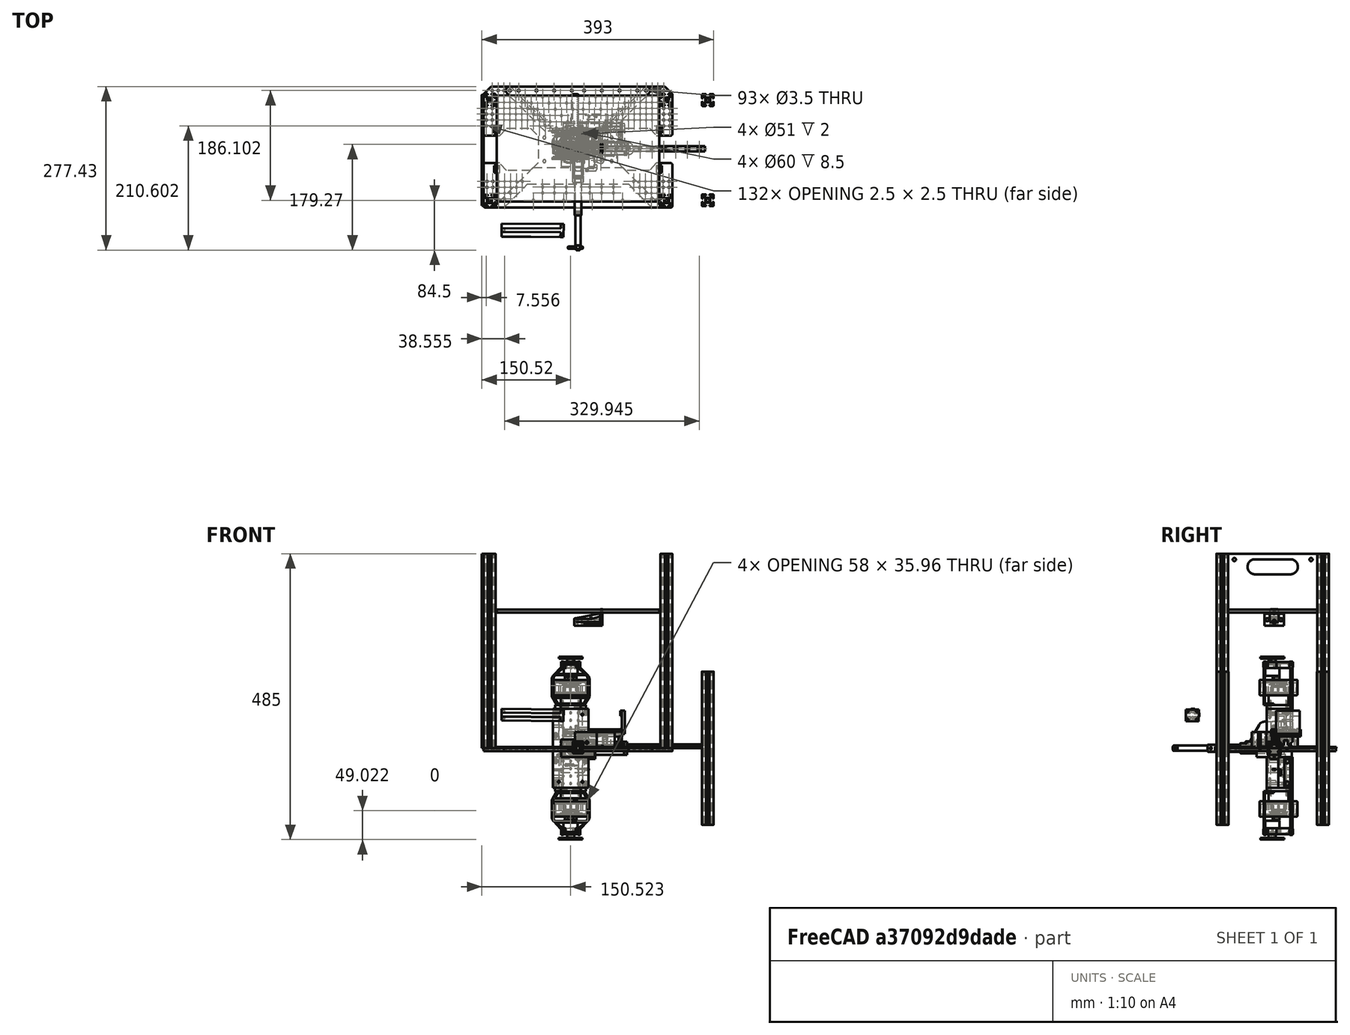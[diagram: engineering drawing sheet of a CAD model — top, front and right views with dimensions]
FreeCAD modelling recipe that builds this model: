
FCSTD DOCUMENT  (FreeCAD 1.0R39319 (Git))
Label: NutSorter
License: All rights reserved
LicenseURL: https://en.wikipedia.org/wiki/All_rights_reserved
objects: Sketcher::SketchObject×84, Part::Feature×80, PartDesign::Pocket×42, PartDesign::Pad×39, App::Part×34, PartDesign::Body×28, App::FeaturePython×27, Part::FeaturePython×11, App::Link×7, PartDesign::Mirrored×6, Assembly::JointGroup×4, PartDesign::FeatureBase×4, Assembly::AssemblyObject×4, PartDesign::Revolution×3, PartDesign::PolarPattern×3, PartDesign::Chamfer×2, PartDesign::LinearPattern×1, Spreadsheet::Sheet×1, PartDesign::MultiTransform×1, PartDesign::AdditiveLoft×1, +2 more types
note: 581 computed .brp shape members not serialized (recipe doc carries the construction recipe); baked Part::Feature solids carry a one-line shape summary decoded from their .brp

FEATURE [Part::FeaturePython] InvoluteRack  # WARN: FeaturePython — macro-defined, semantics opaque (R4)
  AttacherType = Attacher::AttachEngine3D
  add_endings = true
  clearance = 0.25
  double_helix = false
  head = 0
  head_fillet = 0
  height = 3
  helix_angle = 0
  module = 1
  num_teeth = 30
  pressure_angle = 20
  properties_from_tool = false
  root_fillet = 0
  simplified = false
  thickness = 9.5
  transverse_pitch = 3.14159
  version = 1.3.0
FEATURE [Part::FeaturePython] InvoluteGear  # WARN: FeaturePython — macro-defined, semantics opaque (R4)
  AttacherType = Attacher::AttachEngine3D
  addendum_diameter = 26
  angular_backlash = 0
  axle_hole = false
  axle_holesize = 10
  backlash = 0
  clearance = 0.25
  double_helix = false
  head = 0
  head_fillet = 0
  height = 5.5
  helix_angle = 0
  module = 1
  num_teeth = 24
  numpoints = 20
  offset_hole = false
  offset_holeoffset = 10
  offset_holesize = 10
  pitch_diameter = 24
  pressure_angle = 20
  properties_from_tool = false
  reversed_backlash = false
  root_diameter = 21.5
  root_fillet = 0
  shift = 0
  simple = false
  transverse_pitch = 3.14159
  traverse_module = 1
  undercut = false
  version = 1.3.0
  expr: angular_backlash = backlash / pitch_diameter * 360 ° / pi
FEATURE [Part::Feature] Part__Feature008002002006397  label="chariot_MGN9-H"
  Placement = pos=(0,0,0) rot=(0.707107,0.707107,0;3.14159rad)
  shape: bbox 8.005 x 20.01 x 40.67 mm, 245 faces, 9 solids (baked)
FEATURE [Sketcher::SketchObject] Sketch031
  ArcFitTolerance = 0
  AttachmentSupport = -> [YZ_Plane013]
  FullyConstrained = true
  MakeInternals = false
  MapMode = 5
  Placement = pos=(0,0,0) rot=(0.57735,0.57735,0.57735;2.0944rad)
  sketch-geometry (4):
    g0: LineSegment StartX=-4.5 StartY=0 StartZ=0 EndX=4.5 EndY=0 EndZ=0
    g1: LineSegment StartX=4.5 StartY=0 StartZ=0 EndX=4.5 EndY=6.5 EndZ=0
    g2: LineSegment StartX=4.5 StartY=6.5 StartZ=0 EndX=-4.5 EndY=6.5 EndZ=0
    g3: LineSegment StartX=-4.5 StartY=6.5 StartZ=0 EndX=-4.5 EndY=0 EndZ=0
  constraints (11):
    c: Coincident(g0,g1)
    c: Coincident(g1,g2)
    c: Coincident(g2,g3)
    c: Coincident(g3,g0)
    c: Horizontal(g0)
    c: Horizontal(g2)
    c: Vertical(g1)
    c: Vertical(g3)
    c: Symmetric(g0,g0,g-1)
    c: DistanceX(g0,g0) = 9  'width'
    c: DistanceY(g1,g1) = 6.5  'height'
FEATURE [PartDesign::Pad] Pad012
  Direction = (1,0,0)
  Length = 215
  Length2 = 10
  Placement = pos=(0,0,0) rot=(0.57735,0.57735,0.57735;2.0944rad)
  Profile = -> Sketch031
  ReferenceAxis = -> Sketch031 [N_Axis]
  Suppressed = false
  Type = 0
  expr: Length = Spreadsheet001.length
FEATURE [Sketcher::SketchObject] Sketch032
  ArcFitTolerance = 0
  AttachmentSupport = -> [YZ_Plane013]
  FullyConstrained = true
  MakeInternals = false
  MapMode = 5
  Placement = pos=(0,0,0) rot=(0.57735,-0.57735,-0.57735;2.0944rad)
  expr: Constraints[13] = 6.5 - 1.8
  expr: Constraints[14] = <<Sketch031>>.Constraints.width / 2 + 0.1 mm
  sketch-geometry (10):
    g0: ArcOfCircle CenterX=-4.6 CenterY=4.7 CenterZ=0 NormalX=0 NormalY=0 NormalZ=1 AngleXU=0 Radius=1 StartAngle=0.25268 EndAngle=6.03051
    g1: LineSegment StartX=-3.63175 StartY=4.95 StartZ=0 EndX=-3.13175 EndY=4.95 EndZ=0
    g2: LineSegment StartX=-3.13175 StartY=4.95 StartZ=0 EndX=-3.13175 EndY=4.45 EndZ=0
    g3: LineSegment StartX=-3.13175 StartY=4.45 StartZ=0 EndX=-3.63175 EndY=4.45 EndZ=0
    g4: LineSegment [constr] StartX=-4.6 StartY=4.7 StartZ=0 EndX=-3.13175 EndY=4.7 EndZ=0
    g5: ArcOfCircle CenterX=4.6 CenterY=4.7 CenterZ=0 NormalX=0 NormalY=0 NormalZ=1 AngleXU=0 Radius=1 StartAngle=3.39427 EndAngle=9.1721
    g6: LineSegment StartX=3.63175 StartY=4.95 StartZ=0 EndX=3.13175 EndY=4.95 EndZ=0
    g7: LineSegment StartX=3.13175 StartY=4.95 StartZ=0 EndX=3.13175 EndY=4.45 EndZ=0
    g8: LineSegment StartX=3.13175 StartY=4.45 StartZ=0 EndX=3.63175 EndY=4.45 EndZ=0
    g9: LineSegment [constr] StartX=4.6 StartY=4.7 StartZ=0 EndX=3.13175 EndY=4.7 EndZ=0
  constraints (29):
    c: Horizontal(g1)
    c: Coincident(g2,g1)
    c: Vertical(g2)
    c: Coincident(g3,g2)
    c: Horizontal(g3)
    c: Coincident(g4,g0)
    c: Horizontal(g4)
    c: Symmetric(g2,g1,g4)
    c: Coincident(g0,g3)
    c: Coincident(g0,g1)
    c: DistanceY(g2,g2) = 0.5
    c: DistanceX(g1,g1) = 0.5
    c: Diameter(g0) = 2
    c: DistanceY(g-1,g0) = 4.7
    c: DistanceX(g0,g-1) = 4.6
    c: Horizontal(g6)
    c: Coincident(g7,g6)
    c: Vertical(g7)
    c: Coincident(g8,g7)
    c: Horizontal(g8)
    c: Coincident(g9,g5)
    c: Horizontal(g9)
    c: Symmetric(g7,g6,g9)
    c: Coincident(g5,g8)
    c: Coincident(g5,g6)
    c: Diameter(g5) = 2
    c: Symmetric(g4,g9,g-2)
    c: Equal(g2,g7)
    c: Equal(g1,g6)
FEATURE [PartDesign::Pocket] Pocket015  label="Balls cut"
  BaseFeature = -> Pad012
  Direction = (1,0,0)
  Length = 5
  Length2 = 5
  Placement = pos=(0,0,0) rot=(0.57735,0.57735,0.57735;2.0944rad)
  Profile = -> Sketch032
  ReferenceAxis = -> Sketch032 [N_Axis]
  Suppressed = false
  Type = 1
FEATURE [Sketcher::SketchObject] Sketch033
  ArcFitTolerance = 0
  AttachmentOffset = pos=(5.5,0,0) rot=(0,0,1;1.5708rad)
  AttachmentSupport = -> [XY_Plane013]
  FullyConstrained = true
  MakeInternals = false
  MapMode = 5
  Placement = pos=(5.5,0,0) rot=(0,0,1;1.5708rad)
  expr: .AttachmentOffset.Base.x = Spreadsheet001.offset
  sketch-geometry (1):
    g0: Circle CenterX=0 CenterY=0 CenterZ=0 NormalX=0 NormalY=0 NormalZ=1 AngleXU=0 Radius=1.75
  constraints (2):
    c: Coincident(g0,g-1)
    c: Diameter(g0) = 3.5
FEATURE [PartDesign::Pocket] Pocket016  label="Screw hole"
  BaseFeature = -> Pocket015
  Direction = (0,0,-1)
  Length = 5
  Length2 = 5
  Midplane = true
  Placement = pos=(0,0,0) rot=(0.57735,0.57735,0.57735;2.0944rad)
  Profile = -> Sketch033
  ReferenceAxis = -> Sketch033 [N_Axis]
  Suppressed = false
  Type = 1
FEATURE [Sketcher::SketchObject] Sketch034
  ArcFitTolerance = 0
  AttachmentOffset = pos=(5.5,0,6.5) rot=(0,0,1;1.5708rad)
  AttachmentSupport = -> [XY_Plane013]
  FullyConstrained = true
  MakeInternals = false
  MapMode = 5
  Placement = pos=(5.5,0,6.5) rot=(0,0,1;1.5708rad)
  expr: .AttachmentOffset.Base.x = Spreadsheet001.offset
  expr: .AttachmentOffset.Base.z = Sketch031.Constraints.height
  sketch-geometry (1):
    g0: Circle CenterX=0 CenterY=0 CenterZ=0 NormalX=0 NormalY=0 NormalZ=1 AngleXU=0 Radius=3
  constraints (2):
    c: Coincident(g0,g-1)
    c: Diameter(g0) = 6
FEATURE [PartDesign::Pocket] Pocket017  label="Screw head cut"
  BaseFeature = -> Pocket016
  Direction = (0,0,-1)
  Length = 3.5
  Length2 = 5
  Placement = pos=(0,0,0) rot=(0.57735,0.57735,0.57735;2.0944rad)
  Profile = -> Sketch034
  ReferenceAxis = -> Sketch034 [N_Axis]
  Suppressed = false
  Type = 0
FEATURE [PartDesign::Chamfer] Chamfer001  label="Chamfer"
  Angle = 45
  Base = -> Pocket017 [Edge47]
  BaseFeature = -> Pocket017
  ChamferType = 0
  FlipDirection = false
  Placement = pos=(0,0,0) rot=(0.57735,0.57735,0.57735;2.0944rad)
  Size = 0.2
  Size2 = 1
  SupportTransform = false
  Suppressed = false
  UseAllEdges = false
FEATURE [PartDesign::LinearPattern] LinearPattern001  label="LinearPattern"
  BaseFeature = -> Chamfer001
  Direction = -> Sketch033 [V_Axis]
  Length = 200
  Mode = 0
  Occurrences = 11
  Offset = 20
  Originals = -> [Pocket016,Pocket017,Chamfer001]
  Placement = pos=(0,0,0) rot=(0.57735,0.57735,0.57735;2.0944rad)
  Reversed = true
  Suppressed = false
  TransformMode = 0
  expr: Length = Spreadsheet001.distance
  expr: Occurrences = Spreadsheet001.holes_number
FEATURE [PartDesign::Body] Body011  label="Hiwin rail MGN9R"
  AllowCompound = false
  Group = -> [Sketch031,Pad012,Sketch032,Pocket015,Sketch033,Pocket016,Sketch034,Pocket017,Chamfer001,LinearPattern001]
  Origin = -> Origin013
  Tip = -> LinearPattern001
FEATURE [Spreadsheet::Sheet] Spreadsheet001  label="Spreadsheet_MGN9"
  cells = A1='Length rail; B1='Длина рельсы, мм; C1(length)=215; A2='Holes distance; B2='Расстояние между отверстиями; C2(holes_distance)=20; A3='Holes number; B3='Количество отверстий; C3(holes_number)==floor((length - min_offset * 2) / holes_distance) + 2; A4='Distance end holes; B4='Расстояние между центрами крайних отверстий; C4(distance)==holes_distance * (holes_number - 1); A5='Offset 1st hole; B5='Позиция 1го отверстия; C5(offset)=5.5; A6='Min offset 1st hole; B6='Минимальное расстояние от края до центра 1го отверстия; C6(min_offset)=9
FEATURE [App::Part] Part002002  label="Hiwin MGN9"
  Group = -> [Body011,Spreadsheet001]
  Origin = -> Origin014
  Placement = pos=(0,0,220) rot=(0,1,0;1.5708rad)
FEATURE [Assembly::JointGroup] Joints001
FEATURE [Part::Feature] Part__Feature008002002006398  label="L16_50MM_BODY_A"
  Placement = pos=(0,-51,0) rot=(0,0,1;0rad)
  shape: bbox 20.08 x 117.7 x 20.17 mm, 719 faces (baked)
FEATURE [Part::Feature] Part__Feature008002002006399  label="L16_50MM_LIFT_A"
  Placement = pos=(0,-101,0) rot=(0,0,1;0rad)
  shape: bbox 10.2 x 71.63 x 9.971 mm, 40 faces (baked)
  expr: .Placement.Base.y = -51 mm - VarSet.Position_verrin
FEATURE [Sketcher::SketchObject] Sketch036
  ArcFitTolerance = 1e-06
  AttachmentSupport = -> [YZ_Plane017]
  FullyConstrained = true
  MakeInternals = false
  MapMode = 5
  Placement = pos=(0,0,0) rot=(0.57735,0.57735,0.57735;2.0944rad)
  sketch-geometry (4):
    g0: LineSegment StartX=-11 StartY=11 StartZ=0 EndX=-11 EndY=-11 EndZ=0
    g1: LineSegment StartX=-11 StartY=-11 StartZ=0 EndX=11 EndY=-11 EndZ=0
    g2: LineSegment StartX=11 StartY=-11 StartZ=0 EndX=11 EndY=11 EndZ=0
    g3: LineSegment StartX=11 StartY=11 StartZ=0 EndX=-11 EndY=11 EndZ=0
  constraints (11):
    c: Coincident(g0,g1)
    c: Coincident(g1,g2)
    c: Coincident(g2,g3)
    c: Coincident(g3,g0)
    c: Vertical(g0)
    c: Vertical(g2)
    c: Horizontal(g1)
    c: Horizontal(g3)
    c: Symmetric(g2,g0,g-1)
    c: DistanceX(g3,g3) = 22
    c: DistanceY(g0,g0) = 22
FEATURE [Sketcher::SketchObject] Sketch037
  ArcFitTolerance = 1e-06
  AttachmentOffset = pos=(0,0,74) rot=(0,0,1;0rad)
  AttachmentSupport = -> [YZ_Plane017]
  FullyConstrained = true
  MakeInternals = false
  MapMode = 5
  Placement = pos=(74,0,0) rot=(0.57735,0.57735,0.57735;2.0944rad)
  sketch-geometry (4):
    g0: LineSegment StartX=-4 StartY=11 StartZ=0 EndX=-4 EndY=-11 EndZ=0
    g1: LineSegment StartX=-4 StartY=-11 StartZ=0 EndX=4 EndY=-11 EndZ=0
    g2: LineSegment StartX=4 StartY=-11 StartZ=0 EndX=4 EndY=11 EndZ=0
    g3: LineSegment StartX=4 StartY=11 StartZ=0 EndX=-4 EndY=11 EndZ=0
  constraints (11):
    c: Coincident(g0,g1)
    c: Coincident(g1,g2)
    c: Coincident(g2,g3)
    c: Coincident(g3,g0)
    c: Vertical(g0)
    c: Vertical(g2)
    c: Horizontal(g1)
    c: Horizontal(g3)
    c: Symmetric(g2,g0,g-1)
    c: DistanceY(g2,g2) = 22
    c: Distance(g1,g1) = 8
FEATURE [Sketcher::SketchObject] Sketch038
  ArcFitTolerance = 1e-06
  AttachmentSupport = -> [YZ_Plane017]
  FullyConstrained = true
  MakeInternals = false
  MapMode = 5
  Placement = pos=(0,0,0) rot=(0.57735,0.57735,0.57735;2.0944rad)
  sketch-geometry (1):
    g0: Circle CenterX=7.5 CenterY=-8 CenterZ=0 NormalX=0 NormalY=0 NormalZ=1 AngleXU=0 Radius=1.75
  constraints (3):
    c: Diameter(g0) = 3.5
    c: DistanceX(g-1,g0) = 7.5
    c: DistanceY(g0,g-1) = 8
FEATURE [PartDesign::Pad] Pad013
  Direction = (1,0,0)
  Length = 6.5
  Length2 = 10
  Placement = pos=(0,0,0) rot=(1,1,1;2.0944rad)
  Profile = -> Sketch036
  ReferenceAxis = -> Sketch036 [N_Axis]
  Suppressed = false
  Type = 0
FEATURE [PartDesign::Pocket] Pocket018
  BaseFeature = -> Pad013
  Direction = (-1,0,0)
  Length = 5
  Length2 = 5
  Midplane = true
  Placement = pos=(0,0,0) rot=(1,1,1;2.0944rad)
  Profile = -> Sketch038
  ReferenceAxis = -> Sketch038 [N_Axis]
  Suppressed = false
  Type = 1
FEATURE [PartDesign::Mirrored] Mirrored002
  MirrorPlane = -> Sketch038 [V_Axis]
  Placement = pos=(0,0,0) rot=(1,1,1;2.0944rad)
  Suppressed = false
  TransformMode = 0
FEATURE [PartDesign::Mirrored] Mirrored003
  MirrorPlane = -> Sketch038 [H_Axis]
  Placement = pos=(0,0,0) rot=(1,1,1;2.0944rad)
  Suppressed = false
  TransformMode = 0
FEATURE [PartDesign::MultiTransform] MultiTransform
  BaseFeature = -> Pocket018
  Originals = -> [Pocket018]
  Placement = pos=(0,0,0) rot=(1,1,1;2.0944rad)
  Suppressed = false
  TransformMode = 0
  Transformations = -> [Mirrored002,Mirrored003]
FEATURE [Sketcher::SketchObject] Sketch040
  ArcFitTolerance = 1e-06
  AttachmentOffset = pos=(0,0,6.5) rot=(0,0,1;0rad)
  AttachmentSupport = -> [YZ_Plane017]
  FullyConstrained = true
  MakeInternals = false
  MapMode = 5
  Placement = pos=(6.5,0,0) rot=(0.57735,0.57735,0.57735;2.0944rad)
  sketch-geometry (4):
    g0: LineSegment StartX=-4 StartY=11 StartZ=0 EndX=-4 EndY=-11 EndZ=0
    g1: LineSegment StartX=-4 StartY=-11 StartZ=0 EndX=4 EndY=-11 EndZ=0
    g2: LineSegment StartX=4 StartY=-11 StartZ=0 EndX=4 EndY=11 EndZ=0
    g3: LineSegment StartX=4 StartY=11 StartZ=0 EndX=-4 EndY=11 EndZ=0
  constraints (11):
    c: Coincident(g0,g1)
    c: Coincident(g1,g2)
    c: Coincident(g2,g3)
    c: Coincident(g3,g0)
    c: Vertical(g0)
    c: Vertical(g2)
    c: Horizontal(g1)
    c: Horizontal(g3)
    c: Symmetric(g2,g0,g-1)
    c: DistanceX(g3,g3) = 8
    c: DistanceY(g2,g2) = 22
FEATURE [PartDesign::AdditiveLoft] AdditiveLoft
  BaseFeature = -> MultiTransform
  Closed = false
  Placement = pos=(0,0,0) rot=(1,1,1;2.0944rad)
  Profile = -> Sketch037
  Ruled = false
  Sections = -> [Sketch040]
  Suppressed = false
FEATURE [Sketcher::SketchObject] Sketch041
  ArcFitTolerance = 1e-06
  AttachmentOffset = pos=(0,1,0) rot=(0,0,1;0rad)
  AttachmentSupport = -> [AdditiveLoft]
  FullyConstrained = true
  MakeInternals = false
  MapMode = 5
  Placement = pos=(74,0,1) rot=(0.57735,0.57735,0.57735;2.0944rad)
  sketch-geometry (8):
    g0: LineSegment StartX=-11 StartY=10 StartZ=0 EndX=-11 EndY=-10 EndZ=0
    g1: LineSegment StartX=-11 StartY=-10 StartZ=0 EndX=11 EndY=-10 EndZ=0
    g2: LineSegment StartX=11 StartY=-10 StartZ=0 EndX=11 EndY=10 EndZ=0
    g3: LineSegment StartX=11 StartY=10 StartZ=0 EndX=-11 EndY=10 EndZ=0
    g4: Circle CenterX=8 CenterY=-7 CenterZ=0 NormalX=0 NormalY=0 NormalZ=1 AngleXU=0 Radius=1.75
    g5: Circle CenterX=-8 CenterY=-7 CenterZ=0 NormalX=0 NormalY=0 NormalZ=1 AngleXU=0 Radius=1.75
    g6: Circle CenterX=8 CenterY=7 CenterZ=0 NormalX=0 NormalY=0 NormalZ=1 AngleXU=0 Radius=1.75
    g7: Circle CenterX=-8 CenterY=7 CenterZ=0 NormalX=0 NormalY=0 NormalZ=1 AngleXU=0 Radius=1.75
  constraints (21):
    c: Coincident(g0,g1)
    c: Coincident(g1,g2)
    c: Coincident(g2,g3)
    c: Coincident(g3,g0)
    c: Vertical(g0)
    c: Vertical(g2)
    c: Horizontal(g1)
    c: Distance(g1,g1) = 22
    c: Symmetric(g0,g1,g-1)
    c: Horizontal(g3)
    c: DistanceY(g2,g2) = 20
    c: Diameter(g4) = 3.5
    c: Diameter(g5) = 3.5
    c: Diameter(g6) = 3.5
    c: Diameter(g7) = 3.5
    c: Symmetric(g7,g4,g-1)
    c: Symmetric(g5,g6,g-1)
    c: Horizontal(g6,g7)
    c: Vertical(g7,g5)
    c: DistanceX(g7,g-1) = 8
    c: DistanceY(g-1,g7) = 7
FEATURE [PartDesign::Pad] Pad014
  BaseFeature = -> AdditiveLoft
  Direction = (1,0,0)
  Length = 5
  Length2 = 10
  Placement = pos=(0,0,0) rot=(1,1,1;2.0944rad)
  Profile = -> Sketch041
  ReferenceAxis = -> Sketch041 [N_Axis]
  Suppressed = false
  Type = 0
FEATURE [Sketcher::SketchObject] Sketch042
  ArcFitTolerance = 1e-06
  AttachmentSupport = -> [XY_Plane019]
  FullyConstrained = true
  MakeInternals = false
  MapMode = 5
  Placement = pos=(0,0,0) rot=(0,1,0;3.14159rad)
  expr: Constraints[36] = 20 mm + VarSet.jeu
  expr: Constraints[37] = 40 mm + VarSet.jeu
  expr: Constraints[72] = 18 mm + VarSet.jeu
  expr: Constraints[73] = 20 mm + VarSet.jeu
  expr: Constraints[86] = 9 mm + VarSet.jeu
  expr: Constraints[87] = 6.5 mm + VarSet.jeu
  sketch-geometry (52):
    g0: LineSegment StartX=-28.5 StartY=-38 StartZ=0 EndX=1.8 EndY=-38 EndZ=0
    g1: LineSegment StartX=4.8 StartY=-35 StartZ=0 EndX=4.8 EndY=10 EndZ=0
    g2: ArcOfCircle CenterX=1.8 CenterY=-35 CenterZ=0 NormalX=0 NormalY=0 NormalZ=1 AngleXU=0 Radius=3 StartAngle=4.71239 EndAngle=6.28319
    g3: ArcOfCircle CenterX=1.8 CenterY=10 CenterZ=0 NormalX=0 NormalY=0 NormalZ=1 AngleXU=0 Radius=3 StartAngle=0 EndAngle=1.5708
    g4: GeomPoint [constr] X=4.8 Y=-38 Z=0
    g5: LineSegment StartX=-59.5 StartY=-13 StartZ=0 EndX=-34.5 EndY=-13 EndZ=0
    g6: LineSegment StartX=1.8 StartY=13 StartZ=0 EndX=-59.5 EndY=13 EndZ=0
    g7: ArcOfCircle CenterX=-59.5 CenterY=10 CenterZ=0 NormalX=0 NormalY=0 NormalZ=1 AngleXU=0 Radius=3 StartAngle=1.5708 EndAngle=3.14159
    g8: ArcOfCircle CenterX=-59.5 CenterY=-10 CenterZ=0 NormalX=0 NormalY=0 NormalZ=1 AngleXU=0 Radius=3 StartAngle=3.14159 EndAngle=4.71239
    g9: LineSegment StartX=-54.575 StartY=-10.075 StartZ=0 EndX=-16.425 EndY=-10.075 EndZ=0
    g10: LineSegment StartX=-15.425 StartY=-9.075 StartZ=0 EndX=-15.425 EndY=9.075 EndZ=0
    g11: LineSegment StartX=-16.425 StartY=10.075 StartZ=0 EndX=-54.575 EndY=10.075 EndZ=0
    g12: ArcOfCircle CenterX=-54.575 CenterY=9.075 CenterZ=0 NormalX=0 NormalY=0 NormalZ=1 AngleXU=0 Radius=1 StartAngle=1.5708 EndAngle=3.14159
    g13: ArcOfCircle CenterX=-54.575 CenterY=-9.075 CenterZ=0 NormalX=0 NormalY=0 NormalZ=1 AngleXU=0 Radius=1 StartAngle=3.14159 EndAngle=4.71239
    g14: ArcOfCircle CenterX=-16.425 CenterY=-9.075 CenterZ=0 NormalX=0 NormalY=0 NormalZ=1 AngleXU=0 Radius=1 StartAngle=4.71239 EndAngle=6.28319
    g15: ArcOfCircle CenterX=-16.425 CenterY=9.075 CenterZ=0 NormalX=0 NormalY=0 NormalZ=1 AngleXU=0 Radius=1 StartAngle=0 EndAngle=1.5708
    g16: GeomPoint [constr] X=-55.575 Y=10.075 Z=0
    g17: GeomPoint [constr] X=-15.425 Y=-10.075 Z=0
    g18: GeomPoint X=-35.5 Y=0 Z=0
    g19: ArcOfCircle CenterX=-34.5 CenterY=-16 CenterZ=0 NormalX=0 NormalY=0 NormalZ=1 AngleXU=0 Radius=3 StartAngle=0 EndAngle=1.5708
    g20: LineSegment StartX=-31.5 StartY=-16 StartZ=0 EndX=-31.5 EndY=-22.5 EndZ=0
    g21: ArcOfCircle CenterX=-28.5 CenterY=-35 CenterZ=0 NormalX=0 NormalY=0 NormalZ=1 AngleXU=0 Radius=3 StartAngle=3.14159 EndAngle=4.71239
    g22: GeomPoint [constr] X=-31.5 Y=-38 Z=0
    g23: GeomPoint X=-16.5 Y=-25 Z=0
    g24: LineSegment StartX=-26.575 StartY=-17.125 StartZ=0 EndX=-26.575 EndY=-22.5 EndZ=0
    g25: LineSegment StartX=-25.375 StartY=-34.075 StartZ=0 EndX=-7.625 EndY=-34.075 EndZ=0
    g26: LineSegment StartX=-6.425 StartY=-32.875 StartZ=0 EndX=-6.425 EndY=-17.125 EndZ=0
    g27: LineSegment StartX=-7.625 StartY=-15.925 StartZ=0 EndX=-25.375 EndY=-15.925 EndZ=0
    g28: ArcOfCircle CenterX=-25.375 CenterY=-17.125 CenterZ=0 NormalX=0 NormalY=0 NormalZ=1 AngleXU=0 Radius=1.2 StartAngle=1.5708 EndAngle=3.14159
    g29: ArcOfCircle CenterX=-25.375 CenterY=-32.875 CenterZ=0 NormalX=0 NormalY=0 NormalZ=1 AngleXU=0 Radius=1.2 StartAngle=3.14159 EndAngle=4.71239
    g30: ArcOfCircle CenterX=-7.625 CenterY=-32.875 CenterZ=0 NormalX=0 NormalY=0 NormalZ=1 AngleXU=0 Radius=1.2 StartAngle=4.71239 EndAngle=6.28319
    g31: ArcOfCircle CenterX=-7.625 CenterY=-17.125 CenterZ=0 NormalX=0 NormalY=0 NormalZ=1 AngleXU=0 Radius=1.2 StartAngle=-9e-16 EndAngle=1.5708
    g32: GeomPoint [constr] X=-26.575 Y=-15.925 Z=0
    g33: GeomPoint [constr] X=-6.425 Y=-34.075 Z=0
    g34: LineSegment StartX=-6.575 StartY=4.575 StartZ=0 EndX=-6.575 EndY=-4.575 EndZ=0
    g35: LineSegment StartX=-6.575 StartY=-4.575 StartZ=0 EndX=0.075 EndY=-4.575 EndZ=0
    g36: LineSegment StartX=0.075 StartY=-4.575 StartZ=0 EndX=0.075 EndY=4.575 EndZ=0
    g37: LineSegment StartX=0.075 StartY=4.575 StartZ=0 EndX=-6.575 EndY=4.575 EndZ=0
    g38: GeomPoint X=-3.25 Y=0 Z=0
    g39: LineSegment StartX=-26.575 StartY=-22.5 StartZ=0 EndX=-31.5 EndY=-22.5 EndZ=0
    g40: LineSegment StartX=-31.5 StartY=-27.5 StartZ=0 EndX=-26.575 EndY=-27.5 EndZ=0
    g41: LineSegment StartX=-26.575 StartY=-27.5 StartZ=0 EndX=-26.575 EndY=-32.875 EndZ=0
    g42: LineSegment StartX=-31.5 StartY=-27.5 StartZ=0 EndX=-31.5 EndY=-35 EndZ=0
    g43: LineSegment [constr] StartX=-16.5 StartY=-25 StartZ=0 EndX=-31.5 EndY=-25 EndZ=0
    g44: LineSegment StartX=-62.5 StartY=4 StartZ=0 EndX=-55.575 EndY=4 EndZ=0
    g45: LineSegment StartX=-62.5 StartY=-4 StartZ=0 EndX=-55.575 EndY=-4 EndZ=0
    g46: LineSegment StartX=-55.575 StartY=-4 StartZ=0 EndX=-55.575 EndY=-9.075 EndZ=0
    g47: LineSegment StartX=-62.5 StartY=-4 StartZ=0 EndX=-62.5 EndY=-10 EndZ=0
    g48: LineSegment StartX=-62.5 StartY=10 StartZ=0 EndX=-62.5 EndY=4 EndZ=0
    g49: LineSegment StartX=-55.575 StartY=9.075 StartZ=0 EndX=-55.575 EndY=4 EndZ=0
    g50: Circle CenterX=-10.5 CenterY=6 CenterZ=0 NormalX=0 NormalY=0 NormalZ=1 AngleXU=0 Radius=1.75
    g51: Circle CenterX=-10.5 CenterY=-6 CenterZ=0 NormalX=0 NormalY=0 NormalZ=1 AngleXU=0 Radius=1.75
  constraints (130):
    c: Tangent(g0,g2) = -1.5708
    c: Tangent(g1,g2) = -1.5708
    c: Tangent(g1,g3) = -1.5708
    c: Vertical(g1)
    c: Horizontal(g0)
    c: Equal(g2,g3)
    c: PointOnObject(g4,g0)
    c: PointOnObject(g4,g1)
    c: DistanceX(g-1,g1) = 4.8
    c: Tangent(g5,g8) = -1.5708
    c: Tangent(g6,g7) = -1.5708
    c: Horizontal(g5)
    c: Horizontal(g6)
    c: Equal(g7,g8)
    c: DistanceY(g5,g6) = 26
    c: Symmetric(g7,g47,g-1)
    c: Radius(g7) = 3
    c: Tangent(g3,g6) = -1.5708
    c: Tangent(g9,g13) = -1.5708
    c: Tangent(g9,g14) = -1.5708
    c: Tangent(g10,g14) = -1.5708
    c: Tangent(g10,g15) = -1.5708
    c: Tangent(g11,g15) = -1.5708
    c: Tangent(g11,g12) = -1.5708
    c: Vertical(g10)
    c: Horizontal(g9)
    c: Horizontal(g11)
    c: Equal(g12,g13)
    c: Equal(g13,g14)
    c: Equal(g14,g15)
    c: PointOnObject(g16,g11)
    c: PointOnObject(g17,g9)
    c: PointOnObject(g17,g10)
    c: Radius(g13) = 1
    c: PointOnObject(g18,g-1)
    c: Symmetric(g16,g17,g18)
    c: DistanceY(g9,g11) = 20.15
    c: DistanceX(g12,g10) = 40.15
    c: DistanceX(g18,g-1) = 35.5
    c: DistanceX(g7,g18) = 27
    c: Vertical(g20)
    c: PointOnObject(g22,g42)
    c: PointOnObject(g22,g0)
    c: Tangent(g0,g21) = -1.5708
    c: Tangent(g19,g5) = 1.5708
    c: Tangent(g20,g19) = 1.5708
    c: DistanceY(g23,g-1) = 25
    c: DistanceX(g23,g-1) = 16.5
    c: DistanceX(g19,g23) = 15
    c: DistanceY(g0,g23) = 13
    c: Equal(g21,g19)
    c: Equal(g19,g2)
    c: Equal(g3,g7)
    c: Tangent(g24,g28) = -1.5708
    c: Tangent(g25,g29) = -1.5708
    c: Tangent(g25,g30) = -1.5708
    c: Tangent(g26,g30) = -1.5708
    c: Tangent(g26,g31) = -1.5708
    c: Tangent(g27,g31) = -1.5708
    c: Tangent(g27,g28) = -1.5708
    c: Vertical(g24)
    c: Vertical(g26)
    c: Horizontal(g25)
    c: Horizontal(g27)
    c: Equal(g28,g29)
    c: Equal(g29,g30)
    c: Equal(g30,g31)
    c: PointOnObject(g32,g24)
    c: PointOnObject(g32,g27)
    c: PointOnObject(g33,g25)
    c: PointOnObject(g33,g26)
    c: Symmetric(g33,g32,g23)
    c: DistanceY(g25,g27) = 18.15
    c: DistanceX(g24,g26) = 20.15
    c: Radius(g31) = 1.2
    c: Coincident(g34,g35)
    c: Coincident(g35,g36)
    c: Coincident(g36,g37)
    c: Coincident(g37,g34)
    c: Vertical(g34)
    c: Vertical(g36)
    c: Horizontal(g35)
    c: Horizontal(g37)
    c: PointOnObject(g38,g-1)
    c: Symmetric(g36,g34,g38)
    c: DistanceX(g38,g-1) = 3.25
    c: DistanceY(g34,g34) = 9.15
    c: DistanceX(g37,g37) = 6.65
    c: Horizontal(g39)
    c: Horizontal(g40)
    c: PointOnObject(g40,g41)
    c: PointOnObject(g40,g42)
    c: Coincident(g24,g39)
    c: PointOnObject(g41,g40)
    c: Coincident(g20,g39)
    c: PointOnObject(g42,g40)
    c: Coincident(g43,g23)
    c: Horizontal(g43)
    c: Symmetric(g20,g40,g43)
    c: Vertical(g24,g40)
    c: Vertical(g40,g20)
    c: DistanceY(g40,g24) = 5
    c: Vertical(g41)
    c: Tangent(g41,g29) = -1.5708
    c: Tangent(g42,g21) = -1.5708
    c: Vertical(g42)
    c: Horizontal(g44)
    c: PointOnObject(g45,g47)
    c: Horizontal(g45)
    c: PointOnObject(g45,g46)
    c: PointOnObject(g46,g45)
    c: PointOnObject(g47,g45)
    c: Coincident(g48,g44)
    c: Vertical(g48)
    c: Tangent(g7,g48) = -1.5708
    c: Tangent(g47,g8) = -1.5708
    c: Tangent(g46,g13) = -1.5708
    c: Vertical(g46)
    c: Vertical(g47)
    c: Coincident(g49,g44)
    c: Vertical(g49)
    c: Tangent(g49,g12) = -1.5708
    c: Symmetric(g44,g45,g-1)
    c: Vertical(g16,g12)
    c: DistanceY(g45,g44) = 8
    c: Symmetric(g50,g51,g-1)
    c: DistanceX(g18,g51) = 25
    c: DistanceY(g18,g50) = 6
    c: Equal(g50,g51)
    c: Diameter(g50) = 3.5
FEATURE [PartDesign::Pad] Pad015
  Direction = (0,0,-1)
  Length = 27.5
  Length2 = 10
  Profile = -> Sketch042
  ReferenceAxis = -> Sketch042 [N_Axis]
  Reversed = true
  Suppressed = false
  Type = 0
FEATURE [Sketcher::SketchObject] Sketch043
  ArcFitTolerance = 1e-06
  AttachmentSupport = -> [XZ_Plane017]
  FullyConstrained = true
  MakeInternals = false
  MapMode = 5
  Placement = pos=(0,0,0) rot=(1,0,0;1.5708rad)
  sketch-geometry (4):
    g0: ArcOfCircle CenterX=6.5 CenterY=0 CenterZ=0 NormalX=0 NormalY=0 NormalZ=1 AngleXU=0 Radius=5 StartAngle=4.71239 EndAngle=7.85398
    g1: LineSegment StartX=6.5 StartY=5 StartZ=0 EndX=0 EndY=5 EndZ=0
    g2: LineSegment StartX=0 StartY=5 StartZ=0 EndX=0 EndY=-5 EndZ=0
    g3: LineSegment StartX=0 StartY=-5 StartZ=0 EndX=6.5 EndY=-5 EndZ=0
  constraints (11):
    c: PointOnObject(g0,g-1)
    c: Coincident(g1,g2)
    c: Coincident(g2,g3)
    c: Horizontal(g1)
    c: Horizontal(g3)
    c: Vertical(g2)
    c: PointOnObject(g2,g-2)
    c: Tangent(g0,g3) = -1.5708
    c: Tangent(g1,g0) = -1.5708
    c: DistanceX(g1,g1) = 6.5
    c: DistanceY(g2,g2) = 10
FEATURE [PartDesign::Pad] Pad016
  BaseFeature = -> Pad014
  Direction = (0,-1,2e-16)
  Length = 22
  Length2 = 10
  Midplane = true
  Placement = pos=(0,0,0) rot=(1,1,1;2.0944rad)
  Profile = -> Sketch043
  ReferenceAxis = -> Sketch043 [N_Axis]
  Suppressed = false
  Type = 0
FEATURE [Part::FeaturePython] ThreadedRod  label="M4x25-Tige filetée"  # WARN: FeaturePython — macro-defined, semantics opaque (R4)
  Diameter = 6
  DiameterCustom = 6
  Invert = false
  LeftHanded = false
  Length = 25
  MatchOuter = false
  OffsetAngle = 0
  PitchCustom = 1
  Placement = pos=(8,-168,0) rot=(0,1,0;1.5708rad)
  Thread = false
  Type = 4
  expr: .Placement.Base.y = -118 mm - VarSet.Position_verrin
FEATURE [App::Part] L16_50MM_SW_ASM
  Group = -> [Part__Feature008002002006398,Part__Feature008002002006399,ThreadedRod]
  Origin = -> Origin018
  Placement = pos=(15,-25,9.5) rot=(0.57735,-0.57735,0.57735;4.18879rad)
FEATURE [Sketcher::SketchObject] Sketch044
  ArcFitTolerance = 1e-06
  AttachmentSupport = -> [XZ_Plane017]
  FullyConstrained = true
  MakeInternals = false
  MapMode = 5
  Placement = pos=(0,0,0) rot=(1,0,0;1.5708rad)
  sketch-geometry (1):
    g0: Circle CenterX=5 CenterY=0 CenterZ=0 NormalX=0 NormalY=0 NormalZ=1 AngleXU=0 Radius=2.25
  constraints (3):
    c: Diameter(g0) = 4.5
    c: PointOnObject(g0,g-1)
    c: Distance(g0,g-2) = 5
FEATURE [PartDesign::Pocket] Pocket019
  BaseFeature = -> Pad016
  Direction = (0,1,-2e-16)
  Length = 5
  Length2 = 5
  Midplane = true
  Placement = pos=(0,0,0) rot=(1,1,1;2.0944rad)
  Profile = -> Sketch044
  ReferenceAxis = -> Sketch044 [N_Axis]
  Suppressed = false
  Type = 1
FEATURE [Part::FeaturePython] Screw001  label="M3x10-Vis"  # WARN: FeaturePython — macro-defined, semantics opaque (R4)
  Diameter = 4
  Invert = false
  LeftHanded = false
  Length = 10
  LengthCustom = 10
  MatchOuter = false
  OffsetAngle = 0
  Placement = pos=(11,-7.5,8) rot=(0,-1,0;4.71239rad)
  Thread = false
  Type = 75
FEATURE [PartDesign::Pad] Pad018
  BaseFeature = -> Pocket019
  Direction = (3e-16,-1e-15,-1)
  Length = 2
  Length2 = 10
  Placement = pos=(0,0,0) rot=(1,1,1;2.0944rad)
  Profile = -> Pocket019 [Face32]
  Suppressed = false
  Type = 0
FEATURE [Sketcher::SketchObject] Sketch045
  ArcFitTolerance = 1e-06
  AttachmentSupport = -> [XZ_Plane017]
  ExternalGeometry = -> [Sketch041,Pad018]
  FullyConstrained = true
  MakeInternals = false
  MapMode = 5
  Placement = pos=(0,0,0) rot=(1,0,0;1.5708rad)
  sketch-geometry (4):
    g0: LineSegment StartX=9 StartY=2.5 StartZ=0 EndX=9 EndY=-2.5 EndZ=0
    g1: LineSegment StartX=9 StartY=-2.5 StartZ=0 EndX=74 EndY=-2.5 EndZ=0
    g2: LineSegment StartX=74 StartY=-2.5 StartZ=0 EndX=74 EndY=2.5 EndZ=0
    g3: LineSegment StartX=74 StartY=2.5 StartZ=0 EndX=9 EndY=2.5 EndZ=0
  constraints (11):
    c: Coincident(g0,g1)
    c: Coincident(g1,g2)
    c: Coincident(g2,g3)
    c: Coincident(g3,g0)
    c: Vertical(g0)
    c: Horizontal(g1)
    c: Horizontal(g3)
    c: Vertical(g2,g-3)
    c: Symmetric(g2,g1,g-1)
    c: DistanceY(g0,g0) = 5
    c: DistanceX(g-1,g0) = 9
FEATURE [PartDesign::Pad] Pad017
  BaseFeature = -> Pad018
  Direction = (0,-1,2e-16)
  Length = 22
  Length2 = 10
  Midplane = true
  Placement = pos=(0,0,0) rot=(1,1,1;2.0944rad)
  Profile = -> Sketch045
  ReferenceAxis = -> Sketch045 [N_Axis]
  Suppressed = false
  Type = 0
FEATURE [App::VarSet] VarSet
  Position_verrin = 50
  jeu = 0.15
FEATURE [Part::Feature] Part__Feature008002002006400  label="Lever 25T001"
  Placement = pos=(0,0,0) rot=(-1,0,0;1.5708rad)
  shape: bbox 18.84 x 33.03 x 6.019 mm, 125 faces (baked)
FEATURE [Part::Feature] Part__Feature008002002006401  label="Axis Servo001"
  Placement = pos=(0,0,0) rot=(-1,0,0;1.5708rad)
  shape: bbox 5 x 5 x 8 mm, 5 faces (baked)
FEATURE [Part::Feature] Part__Feature008002002006402  label="Servo DS3218MG001"
  Placement = pos=(0,0,0) rot=(-1,0,0;1.5708rad)
  shape: bbox 55 x 20 x 41 mm, 772 faces (baked)
FEATURE [Part::FeaturePython] Screw004  label="M2x5-Vis"  # WARN: FeaturePython — macro-defined, semantics opaque (R4)
  BaseObject = -> Body014 [Edge6]
  Diameter = 2
  Invert = true
  LeftHanded = false
  Length = 10
  LengthCustom = 5
  MatchOuter = false
  OffsetAngle = 0
  Placement = pos=(0,1e-15,4.8) rot=(0,0,1;0rad)
  Thread = false
  Type = 76
FEATURE [Sketcher::SketchObject] Sketch048
  ArcFitTolerance = 0
  AttachmentSupport = -> [XZ_Plane021]
  FullyConstrained = true
  MakeInternals = false
  MapMode = 5
  Placement = pos=(0,0,0) rot=(1,0,0;1.5708rad)
  expr: Constraints[19] = 19.8 / 2
  sketch-geometry (8):
    g0: LineSegment StartX=2.5 StartY=3.4 StartZ=0 EndX=2.5 EndY=0 EndZ=0
    g1: LineSegment StartX=2.5 StartY=0 StartZ=0 EndX=4.2 EndY=0 EndZ=0
    g2: LineSegment StartX=4.2 StartY=0 StartZ=0 EndX=4.2 EndY=2 EndZ=0
    g3: LineSegment StartX=4.2 StartY=2 StartZ=0 EndX=9.9 EndY=2 EndZ=0
    g4: LineSegment StartX=9.9 StartY=2 StartZ=0 EndX=9.9 EndY=4.4 EndZ=0
    g5: LineSegment StartX=9.9 StartY=4.4 StartZ=0 EndX=1.5 EndY=4.4 EndZ=0
    g6: LineSegment StartX=1.5 StartY=4.4 StartZ=0 EndX=1.5 EndY=3.4 EndZ=0
    g7: LineSegment StartX=1.5 StartY=3.4 StartZ=0 EndX=2.5 EndY=3.4 EndZ=0
  constraints (24):
    c: PointOnObject(g0,g-1)
    c: Vertical(g0)
    c: Coincident(g1,g0)
    c: PointOnObject(g1,g-1)
    c: Coincident(g2,g1)
    c: Vertical(g2)
    c: Coincident(g3,g2)
    c: Horizontal(g3)
    c: Coincident(g4,g3)
    c: Vertical(g4)
    c: Coincident(g5,g4)
    c: Horizontal(g5)
    c: Coincident(g6,g5)
    c: Coincident(g7,g6)
    c: Coincident(g7,g0)
    c: Horizontal(g7)
    c: Vertical(g6)
    c: DistanceY(g4,g4) = 2.4
    c: DistanceY(g2,g2) = 2
    c: DistanceX(g-1,g4) = 9.9
    c: DistanceX(g-1,g6) = 1.5
    c: DistanceY(g0,g0) = 3.4
    c: DistanceX(g-1,g0) = 2.5
    c: DistanceX(g1,g1) = 1.7
FEATURE [PartDesign::Revolution] Revolution001
  Angle = 360
  Angle2 = 60
  Axis = (0,2e-16,1)
  Base = (0,0,0)
  Placement = pos=(0,0,0) rot=(1,0,0;1.5708rad)
  Profile = -> Sketch048
  ReferenceAxis = -> Sketch048 [V_Axis]
  Reversed = true
  Suppressed = false
  Type = 0
FEATURE [Sketcher::SketchObject] Sketch049
  ArcFitTolerance = 0
  AttachmentSupport = -> [XY_Plane021]
  FullyConstrained = true
  MakeInternals = false
  MapMode = 5
  sketch-geometry (1):
    g0: Circle CenterX=-7 CenterY=0 CenterZ=0 NormalX=0 NormalY=0 NormalZ=1 AngleXU=0 Radius=1.2
  constraints (3):
    c: PointOnObject(g0,g-1)
    c: Diameter(g0) = 2.4
    c: DistanceX(g0,g-1) = 7
FEATURE [PartDesign::Pocket] Pocket025
  BaseFeature = -> Revolution001
  Direction = (0,0,-1)
  Length = 5
  Length2 = 5
  Midplane = true
  Placement = pos=(0,0,0) rot=(1,0,0;1.5708rad)
  Profile = -> Sketch049
  ReferenceAxis = -> Sketch049 [N_Axis]
  Suppressed = false
  Type = 1
FEATURE [PartDesign::PolarPattern] PolarPattern003
  Angle = 360
  Axis = -> Sketch049 [N_Axis]
  BaseFeature = -> Pocket025
  Mode = 0
  Occurrences = 4
  Offset = 120
  Originals = -> [Pocket025]
  Placement = pos=(0,0,0) rot=(1,0,0;1.5708rad)
  Suppressed = false
  TransformMode = 0
FEATURE [PartDesign::Body] Body014  label="Corps001"
  AllowCompound = false
  Group = -> [Sketch048,Revolution001,Sketch049,Pocket025,PolarPattern003]
  Origin = -> Origin021
  Placement = pos=(0,0,0.4) rot=(0,0,1;0rad)
  Tip = -> PolarPattern003
FEATURE [App::Part] Part007  label="servo_DS3218MG002"
  Group = -> [Part__Feature008002002006400,Part__Feature008002002006401,Part__Feature008002002006402,Body014,Screw004]
  Origin = -> Origin020
FEATURE [Sketcher::SketchObject] Sketch055
  ArcFitTolerance = 1e-06
  AttachmentSupport = -> [XY_Plane019]
  ExternalGeometry = -> [Pad015]
  FullyConstrained = true
  MakeInternals = false
  MapMode = 5
  Placement = pos=(0,0,0) rot=(0,1,0;3.14159rad)
  sketch-geometry (8):
    g0: LineSegment StartX=-6.575 StartY=4.575 StartZ=0 EndX=-6.575 EndY=-4.575 EndZ=0
    g1: LineSegment StartX=-6.575 StartY=-4.575 StartZ=0 EndX=0.075 EndY=-4.575 EndZ=0
    g2: LineSegment StartX=0.075 StartY=-4.575 StartZ=0 EndX=0.075 EndY=4.575 EndZ=0
    g3: LineSegment StartX=0.075 StartY=4.575 StartZ=0 EndX=-6.575 EndY=4.575 EndZ=0
    g4: LineSegment StartX=-18.425 StartY=-15.925 StartZ=0 EndX=-18.425 EndY=-34.075 EndZ=0
    g5: LineSegment StartX=-18.425 StartY=-34.075 StartZ=0 EndX=-6.425 EndY=-34.075 EndZ=0
    g6: LineSegment StartX=-6.425 StartY=-34.075 StartZ=0 EndX=-6.425 EndY=-15.925 EndZ=0
    g7: LineSegment StartX=-6.425 StartY=-15.925 StartZ=0 EndX=-18.425 EndY=-15.925 EndZ=0
  constraints (22):
    c: Coincident(g0,g1)
    c: Coincident(g1,g2)
    c: Coincident(g2,g3)
    c: Coincident(g3,g0)
    c: Vertical(g0)
    c: Vertical(g2)
    c: Horizontal(g1)
    c: Horizontal(g3)
    c: Coincident(g4,g5)
    c: Coincident(g5,g6)
    c: Coincident(g6,g7)
    c: Coincident(g7,g4)
    c: Vertical(g4)
    c: Vertical(g6)
    c: Horizontal(g5)
    c: Horizontal(g7)
    c: PointOnObject(g4,g-5)
    c: PointOnObject(g6,g-6)
    c: PointOnObject(g5,g-7)
    c: DistanceX(g7,g7) = 12
    c: Coincident(g0,g-3)
    c: Coincident(g1,g-4)
FEATURE [PartDesign::Pad] Pad023
  BaseFeature = -> Pad015
  Direction = (0,0,-1)
  Length = 5
  Length2 = 10
  Profile = -> Sketch055
  ReferenceAxis = -> Sketch055 [N_Axis]
  Reversed = true
  Suppressed = false
  Type = 0
FEATURE [Sketcher::SketchObject] Sketch056
  ArcFitTolerance = 1e-06
  AttachmentOffset = pos=(0,0,-0.25) rot=(0,0,1;0rad)
  AttachmentSupport = -> [YZ_Plane019]
  ExternalGeometry = -> [Pad023]
  FullyConstrained = true
  MakeInternals = false
  MapMode = 5
  Placement = pos=(-0.25,0,0) rot=(0.57735,0.57735,0.57735;2.0944rad)
  sketch-geometry (7):
    g0: LineSegment StartX=-8.575 StartY=27.5 StartZ=0 EndX=8.575 EndY=27.5 EndZ=0
    g1: LineSegment StartX=4.575 StartY=31.5 StartZ=0 EndX=4.575 EndY=34.5 EndZ=0
    g2: LineSegment StartX=-4.575 StartY=34.5 StartZ=0 EndX=-4.575 EndY=31.5 EndZ=0
    g3: ArcOfCircle CenterX=0 CenterY=34.5 CenterZ=0 NormalX=0 NormalY=0 NormalZ=1 AngleXU=0 Radius=4.575 StartAngle=0 EndAngle=3.14159
    g4: Circle CenterX=0 CenterY=34.5 CenterZ=0 NormalX=0 NormalY=0 NormalZ=1 AngleXU=0 Radius=1.75
    g5: ArcOfCircle CenterX=-8.575 CenterY=31.5 CenterZ=0 NormalX=0 NormalY=0 NormalZ=1 AngleXU=0 Radius=4 StartAngle=4.71239 EndAngle=6.28319
    g6: ArcOfCircle CenterX=8.575 CenterY=31.5 CenterZ=0 NormalX=0 NormalY=0 NormalZ=1 AngleXU=0 Radius=4 StartAngle=3.14159 EndAngle=4.71239
  constraints (17):
    c: Vertical(g1)
    c: Vertical(g2)
    c: PointOnObject(g3,g-2)
    c: DistanceY(g-1,g3) = 34.5
    c: Tangent(g3,g1) = -1.5708
    c: Coincident(g4,g3)
    c: Diameter(g4) = 3.5
    c: Tangent(g3,g2) = -1.5708
    c: Tangent(g2,g5) = 1.5708
    c: Tangent(g0,g5) = -1.5708
    c: Horizontal(g0,g-3)
    c: Vertical(g2,g-3)
    c: Horizontal(g0,g-3)
    c: Tangent(g6,g1) = 1.5708
    c: Tangent(g0,g6) = -1.5708
    c: Equal(g1,g2)
    c: Radius(g6) = 4
FEATURE [PartDesign::Pad] Pad024
  BaseFeature = -> Pad023
  Direction = (1,0,0)
  Length = 4
  Length2 = 10
  Profile = -> Sketch056
  ReferenceAxis = -> Sketch056 [N_Axis]
  Reversed = true
  Suppressed = false
  Type = 0
FEATURE [Sketcher::SketchObject] Sketch057
  ArcFitTolerance = 1e-06
  AttachmentSupport = -> [XY_Plane019]
  ExternalGeometry = -> [Pad024]
  FullyConstrained = true
  MakeInternals = false
  MapMode = 5
  sketch-geometry (14):
    g0: ArcOfCircle CenterX=34.5 CenterY=-16 CenterZ=0 NormalX=0 NormalY=0 NormalZ=1 AngleXU=0 Radius=3 StartAngle=1.5708 EndAngle=3.14159
    g1: ArcOfCircle CenterX=39 CenterY=-20 CenterZ=0 NormalX=0 NormalY=0 NormalZ=1 AngleXU=0 Radius=5 StartAngle=4.34942 EndAngle=6.76197
    g2: LineSegment StartX=31.5 StartY=-16 StartZ=0 EndX=31.5 EndY=-22.5 EndZ=0
    g3: LineSegment StartX=34.5 StartY=-13 StartZ=0 EndX=41 EndY=-13 EndZ=0
    g4: Circle CenterX=39 CenterY=-20 CenterZ=0 NormalX=0 NormalY=0 NormalZ=1 AngleXU=0 Radius=1.75
    g5: LineSegment StartX=31.5 StartY=-22.5 StartZ=0 EndX=37.2247 EndY=-24.6742 EndZ=0
    g6: LineSegment StartX=43.4378 StartY=-17.6965 StartZ=0 EndX=41 EndY=-13 EndZ=0
    g7: Circle CenterX=29.2 CenterY=20 CenterZ=0 NormalX=0 NormalY=0 NormalZ=1 AngleXU=0 Radius=1.75
    g8: LineSegment StartX=20.2 StartY=13 StartZ=0 EndX=38.2 EndY=13 EndZ=0
    g9: LineSegment StartX=34.2 StartY=17 StartZ=0 EndX=34.2 EndY=20 EndZ=0
    g10: LineSegment StartX=24.2 StartY=17 StartZ=0 EndX=24.2 EndY=20 EndZ=0
    g11: ArcOfCircle CenterX=29.2 CenterY=20 CenterZ=0 NormalX=0 NormalY=0 NormalZ=1 AngleXU=0 Radius=5 StartAngle=0 EndAngle=3.14159
    g12: ArcOfCircle CenterX=20.2 CenterY=17 CenterZ=0 NormalX=0 NormalY=0 NormalZ=1 AngleXU=0 Radius=4 StartAngle=4.71239 EndAngle=6.28319
    g13: ArcOfCircle CenterX=38.2 CenterY=17 CenterZ=0 NormalX=0 NormalY=0 NormalZ=1 AngleXU=0 Radius=4 StartAngle=3.14159 EndAngle=4.71239
  constraints (34):
    c: Coincident(g0,g-3)
    c: Coincident(g3,g0)
    c: Horizontal(g3)
    c: Vertical(g2)
    c: Tangent(g2,g0) = -1.5708
    c: Coincident(g0,g-3)
    c: Coincident(g4,g1)
    c: Diameter(g4) = 3.5
    c: Radius(g1) = 5
    c: Coincident(g2,g5)
    c: Tangent(g5,g1) = -1.5708
    c: Coincident(g6,g3)
    c: Tangent(g6,g1) = -1.5708
    c: Equal(g3,g2)
    c: DistanceX(g3,g3) = 6.5
    c: Horizontal(g8)
    c: Vertical(g9)
    c: Vertical(g10)
    c: PointOnObject(g8,g-4)
    c: Coincident(g7,g11)
    c: Tangent(g11,g9) = -1.5708
    c: Tangent(g11,g10) = 1.5708
    c: Tangent(g10,g12) = -1.5708
    c: Tangent(g8,g12) = -1.5708
    c: Tangent(g13,g9) = 1.5708
    c: Tangent(g13,g8) = -1.5708
    c: Diameter(g7) = 3.5
    c: Equal(g11,g1)
    c: Equal(g10,g9)
    c: Radius(g13) = 4
    c: DistanceY(g-1,g7) = 20
    c: DistanceX(g-1,g7) = 29.2
    c: DistanceY(g1,g-1) = 20
    c: DistanceX(g-1,g1) = 39
FEATURE [PartDesign::Pad] Pad025
  BaseFeature = -> Pad024
  Direction = (0,0,1)
  Length = 3
  Length2 = 10
  Profile = -> Sketch057
  ReferenceAxis = -> Sketch057 [N_Axis]
  Suppressed = false
  Type = 0
FEATURE [Sketcher::SketchObject] Sketch058
  ArcFitTolerance = 1e-06
  AttachmentOffset = pos=(15,9.6,25) rot=(0,0,1;0rad)
  AttachmentSupport = -> [XZ_Plane019]
  FullyConstrained = true
  MakeInternals = false
  MapMode = 5
  Placement = pos=(15,-25,9.6) rot=(1,0,0;1.5708rad)
  sketch-geometry (2):
    g0: ArcOfCircle CenterX=0 CenterY=0 CenterZ=0 NormalX=0 NormalY=0 NormalZ=1 AngleXU=0 Radius=2.25 StartAngle=1.99427 EndAngle=7.43051
    g1: ArcOfCircle CenterX=0 CenterY=1 CenterZ=0 NormalX=0 NormalY=0 NormalZ=1 AngleXU=0 Radius=1.4 StartAngle=0.849413 EndAngle=2.29218
  constraints (7):
    c: Coincident(g0,g-1)
    c: Diameter(g0) = 4.5
    c: Coincident(g1,g0)
    c: Coincident(g1,g0)
    c: PointOnObject(g1,g-2)
    c: DistanceY(g0,g1) = 1
    c: Radius(g1) = 1.4
FEATURE [PartDesign::Pocket] Pocket028
  BaseFeature = -> Pad025
  Direction = (0,1,-2e-16)
  Length = 27
  Length2 = 5
  Midplane = true
  Profile = -> Sketch058
  ReferenceAxis = -> Sketch058 [N_Axis]
  Suppressed = false
  Type = 0
FEATURE [Sketcher::SketchObject] Sketch059
  ArcFitTolerance = 1e-06
  AttachmentSupport = -> [Pocket028]
  ExternalGeometry = -> [Pocket028]
  FullyConstrained = true
  MakeInternals = false
  MapMode = 5
  Placement = pos=(0,0,27.5) rot=(0,0,1;0rad)
  sketch-geometry (2):
    g0: Circle CenterX=10.5 CenterY=6 CenterZ=0 NormalX=0 NormalY=0 NormalZ=1 AngleXU=0 Radius=2.1
    g1: Circle CenterX=10.5 CenterY=-6 CenterZ=0 NormalX=0 NormalY=0 NormalZ=1 AngleXU=0 Radius=2.1
  constraints (4):
    c: Coincident(g0,g-3)
    c: Coincident(g1,g-4)
    c: Equal(g0,g1)
    c: Diameter(g0) = 4.2
FEATURE [PartDesign::Pocket] Pocket029
  BaseFeature = -> Pocket028
  Direction = (0,0,-1)
  Length = 1.5
  Length2 = 5
  Profile = -> Sketch059
  ReferenceAxis = -> Sketch059 [N_Axis]
  Suppressed = false
  Type = 0
FEATURE [Sketcher::SketchObject] Sketch060
  ArcFitTolerance = 1e-06
  AttachmentSupport = -> [XZ_Plane023]
  FullyConstrained = true
  MakeInternals = false
  MapMode = 5
  Placement = pos=(0,0,0) rot=(0,0.707107,0.707107;3.14159rad)
  sketch-geometry (6):
    g0: ArcOfCircle CenterX=0 CenterY=0 CenterZ=0 NormalX=0 NormalY=0 NormalZ=1 AngleXU=0 Radius=5 StartAngle=3.14159 EndAngle=6.28319
    g1: ArcOfCircle CenterX=-1.246e-13 CenterY=21 CenterZ=0 NormalX=0 NormalY=0 NormalZ=1 AngleXU=0 Radius=5 StartAngle=-7.64e-14 EndAngle=3.14159
    g2: LineSegment StartX=-5 StartY=9.017e-13 StartZ=0 EndX=-5 EndY=21 EndZ=0
    g3: LineSegment StartX=5 StartY=6.3e-15 StartZ=0 EndX=5 EndY=21 EndZ=0
    g4: Circle CenterX=0 CenterY=0 CenterZ=0 NormalX=0 NormalY=0 NormalZ=1 AngleXU=0 Radius=2.25
    g5: Circle CenterX=-1.246e-13 CenterY=21 CenterZ=0 NormalX=0 NormalY=0 NormalZ=1 AngleXU=0 Radius=2.25
  constraints (13):
    c: Tangent(g0,g2) = 1.5708
    c: Tangent(g0,g3) = -1.5708
    c: Tangent(g1,g2) = 1.5708
    c: Tangent(g1,g3) = -1.5708
    c: Equal(g0,g1)
    c: Vertical(g3)
    c: Coincident(g0,g-1)
    c: DistanceY(g0,g1) = 21  'longueur_extention'
    c: Radius(g0) = 5
    c: Diameter(g4) = 4.5
    c: Coincident(g4,g0)
    c: Diameter(g5) = 4.5
    c: Coincident(g5,g1)
FEATURE [PartDesign::Pad] Pad026
  Direction = (0,1,-2e-16)
  Length = 5
  Length2 = 10
  Placement = pos=(0,0,0) rot=(1,0,0;1.5708rad)
  Profile = -> Sketch060
  ReferenceAxis = -> Sketch060 [N_Axis]
  Suppressed = false
  Type = 0
FEATURE [Sketcher::SketchObject] Sketch061
  ArcFitTolerance = 1e-06
  AttachmentSupport = -> [XZ_Plane023]
  ExternalGeometry = -> [Pad026]
  FullyConstrained = false
  MakeInternals = false
  MapMode = 5
  Placement = pos=(0,0,0) rot=(1,0,0;1.5708rad)
  sketch-geometry (6):
    g0: LineSegment StartX=-5 StartY=1 StartZ=0 EndX=-5 EndY=-1.6e-15 EndZ=0
    g1: LineSegment StartX=-4.89898 StartY=-1 StartZ=0 EndX=-2.01556 EndY=-1 EndZ=0
    g2: LineSegment StartX=-2.01556 StartY=1 StartZ=0 EndX=-5 EndY=1 EndZ=0
    g3: ArcOfCircle CenterX=0 CenterY=0 CenterZ=0 NormalX=0 NormalY=0 NormalZ=1 AngleXU=0 Radius=5 StartAngle=3.14159 EndAngle=3.34295
    g4: ArcOfCircle CenterX=0 CenterY=0 CenterZ=0 NormalX=0 NormalY=0 NormalZ=1 AngleXU=0 Radius=2.25 StartAngle=2.68104 EndAngle=3.60215
    g5: LineSegment [constr] StartX=-4.17111 StartY=1 StartZ=0 EndX=-4.17111 EndY=-1 EndZ=0
  constraints (16):
    c: Coincident(g2,g0)
    c: Vertical(g0)
    c: Horizontal(g1)
    c: Horizontal(g2)
    c: PointOnObject(g1,g-4)
    c: Coincident(g3,g-1)
    c: Coincident(g3,g-3)
    c: Coincident(g4,g3)
    c: Coincident(g4,g1)
    c: Coincident(g0,g3)
    c: Coincident(g2,g4)
    c: Coincident(g1,g3)
    c: PointOnObject(g5,g2)
    c: PointOnObject(g5,g1)
    c: Symmetric(g5,g5,g-1)
    c: DistanceY(g5,g5) = 2
FEATURE [PartDesign::Pad] Pad027
  BaseFeature = -> Pad026
  Direction = (0,-1,2e-16)
  Length = 2
  Length2 = 10
  Placement = pos=(0,0,0) rot=(1,0,0;1.5708rad)
  Profile = -> Sketch061
  ReferenceAxis = -> Sketch061 [N_Axis]
  Suppressed = false
  Type = 0
FEATURE [PartDesign::Mirrored] Mirrored004
  BaseFeature = -> Pad027
  MirrorPlane = -> Sketch061 [V_Axis]
  Originals = -> [Pad027]
  Placement = pos=(0,0,0) rot=(1,0,0;1.5708rad)
  Suppressed = false
  TransformMode = 0
FEATURE [PartDesign::Body] Body016  label="extention_verrin"
  AllowCompound = false
  Group = -> [Sketch060,Pad026,Sketch061,Pad027,Mirrored004]
  Origin = -> Origin023
  Placement = pos=(9,13,0) rot=(0,0,1;0rad)
  Tip = -> Mirrored004
FEATURE [PartDesign::Pad] Pad028
  BaseFeature = -> Pad017
  Direction = (1.6e-15,1,-7e-16)
  Length = 2
  Length2 = 10
  Placement = pos=(0,0,0) rot=(1,1,1;2.0944rad)
  Profile = -> Pad017 [Face17,Face23,Face38]
  Suppressed = false
  Type = 0
FEATURE [Sketcher::SketchObject] Sketch062
  ArcFitTolerance = 1e-06
  AttachmentOffset = pos=(0,5,0) rot=(0,0,1;0rad)
  AttachmentSupport = -> [Pad028]
  ExternalGeometry = -> [Pad028]
  FullyConstrained = true
  MakeInternals = false
  MapMode = 5
  Placement = pos=(5,13,0) rot=(0.57735,0.57735,0.57735;4.18879rad)
  sketch-geometry (4):
    g0: LineSegment StartX=-1.15 StartY=0 StartZ=0 EndX=1.15 EndY=0 EndZ=0
    g1: LineSegment StartX=1.15 StartY=0 StartZ=0 EndX=1.15 EndY=6.5 EndZ=0
    g2: LineSegment StartX=1.15 StartY=6.5 StartZ=0 EndX=-1.15 EndY=6.5 EndZ=0
    g3: LineSegment StartX=-1.15 StartY=6.5 StartZ=0 EndX=-1.15 EndY=0 EndZ=0
  constraints (11):
    c: Coincident(g0,g1)
    c: Coincident(g1,g2)
    c: Coincident(g2,g3)
    c: Coincident(g3,g0)
    c: Horizontal(g2)
    c: Vertical(g1)
    c: Vertical(g3)
    c: PointOnObject(g-4,g2)
    c: DistanceX(g2,g2) = 2.3
    c: Symmetric(g0,g0,g-2)
    c: PointOnObject(g-1,g0)
FEATURE [PartDesign::Pocket] Pocket030
  BaseFeature = -> Pad028
  Direction = (1e-16,-1,1.4e-15)
  Length = 2
  Length2 = 5
  Placement = pos=(0,0,0) rot=(1,1,1;2.0944rad)
  Profile = -> Sketch062
  ReferenceAxis = -> Sketch062 [N_Axis]
  Suppressed = false
  Type = 0
FEATURE [PartDesign::Mirrored] Mirrored005
  BaseFeature = -> Pocket030
  MirrorPlane = -> Sketch062 [H_Axis]
  Originals = -> [Pocket030]
  Placement = pos=(0,0,0) rot=(1,1,1;2.0944rad)
  Suppressed = false
  TransformMode = 0
FEATURE [PartDesign::Fillet] Fillet
  Base = -> Pocket029 [Edge169,Edge108]
  BaseFeature = -> Pocket029
  Radius = 3
  SupportTransform = false
  Suppressed = false
  UseAllEdges = false
FEATURE [PartDesign::Body] Body013  label="support_pince_planche_bas"
  AllowCompound = false
  Group = -> [Sketch042,Pad015,Sketch055,Pad023,Sketch056,Pad024,Sketch057,Pad025,Sketch058,Pocket028,Sketch059,Pocket029,Fillet]
  Origin = -> Origin019
  Tip = -> Fillet
FEATURE [Sketcher::SketchObject] Sketch240
  ArcFitTolerance = 1e-06
  AttachmentSupport = -> [XZ_Plane017]
  ExternalGeometry = -> [Mirrored005]
  FullyConstrained = true
  MakeInternals = false
  MapMode = 5
  Placement = pos=(0,0,0) rot=(1,0,0;1.5708rad)
  sketch-geometry (4):
    g0: ArcOfCircle CenterX=13.25 CenterY=20 CenterZ=0 NormalX=0 NormalY=0 NormalZ=1 AngleXU=0 Radius=11.25 StartAngle=3.14159 EndAngle=4.06889
    g1: LineSegment StartX=2 StartY=20 StartZ=0 EndX=0 EndY=20 EndZ=0
    g2: LineSegment StartX=0 StartY=20 StartZ=0 EndX=0 EndY=11 EndZ=0
    g3: LineSegment StartX=0 StartY=11 StartZ=0 EndX=6.5 EndY=11 EndZ=0
  constraints (11):
    c: Coincident(g0,g1)
    c: PointOnObject(g1,g-2)
    c: Coincident(g1,g2)
    c: Coincident(g2,g-3)
    c: Coincident(g2,g3)
    c: Coincident(g3,g-3)
    c: Horizontal(g1)
    c: Coincident(g0,g3)
    c: Horizontal(g0,g0)
    c: Distance(g1,g1) = 2
    c: DistanceY(g2,g2) = 9
FEATURE [PartDesign::Pad] Pad116
  BaseFeature = -> Mirrored005
  Direction = (0,-1,2e-16)
  Length = 22
  Length2 = 10
  Midplane = true
  Placement = pos=(0,0,0) rot=(1,1,1;2.0944rad)
  Profile = -> Sketch240
  ReferenceAxis = -> Sketch240 [N_Axis]
  Suppressed = false
  Type = 0
FEATURE [PartDesign::Body] Body012  label="jonction_rail_pince"
  AllowCompound = false
  Group = -> [Sketch036,Sketch037,Sketch038,Pad013,Pocket018,MultiTransform,Mirrored002,Mirrored003,Sketch040,AdditiveLoft,Sketch041,Pad014,Sketch043,Pad016,Sketch044,Pocket019,Sketch045,Pad018,Pad017,Pad028,Sketch062,Pocket030,Mirrored005,Sketch240,Pad116]
  Origin = -> Origin017
  Placement = pos=(4,0,0) rot=(0,0,1;0rad)
  Tip = -> Pad116
FEATURE [App::Part] Part
  Group = -> [Part__Feature008002002006397,Body012,Screw001,Body016]
  Origin = -> Origin016
  Placement = pos=(6,0,142.5) rot=(1,0,0;3.14159rad)
FEATURE [Part::FeaturePython] InvoluteGear001  label="InvoluteGear_11_77"  # WARN: FeaturePython — macro-defined, semantics opaque (R4)
  AttacherType = Attacher::AttachEngine3D
  addendum_diameter = 26
  angular_backlash = 0
  axle_hole = false
  axle_holesize = 10
  backlash = 0
  clearance = 0.25
  double_helix = false
  head = 0
  head_fillet = 0
  height = 5.5
  helix_angle = 0
  module = 1
  num_teeth = 24
  numpoints = 20
  offset_hole = false
  offset_holeoffset = 10
  offset_holesize = 10
  pitch_diameter = 24
  pressure_angle = 20
  properties_from_tool = false
  reversed_backlash = false
  root_diameter = 21.5
  root_fillet = 0
  shift = 0
  simple = false
  transverse_pitch = 3.14159
  traverse_module = 1
  undercut = false
  version = 1.3.0
  expr: angular_backlash = backlash / pitch_diameter * 360 ° / pi
FEATURE [PartDesign::FeatureBase] BaseFeature003
  BaseFeature = -> InvoluteGear001
  Suppressed = false
FEATURE [Part::FeaturePython] InvoluteRack001  label="InvoluteRack_11_77"  # WARN: FeaturePython — macro-defined, semantics opaque (R4)
  AttacherType = Attacher::AttachEngine3D
  add_endings = true
  clearance = 0.25
  double_helix = false
  head = 0
  head_fillet = 0
  height = 3
  helix_angle = 0
  module = 1
  num_teeth = 30
  pressure_angle = 20
  properties_from_tool = false
  root_fillet = 0
  simplified = false
  thickness = 9.5
  transverse_pitch = 3.14159
  version = 1.3.0
FEATURE [PartDesign::FeatureBase] BaseFeature002
  BaseFeature = -> InvoluteRack001
  Suppressed = false
FEATURE [App::FeaturePython] Joint001  label="Fixe001"  # Assembly joint (typed FeaturePython)
  Activated = true
  AngleMax = 0
  AngleMin = 0
  Detach1 = false
  Detach2 = false
  Distance = 0
  Distance2 = 0
  EnableAngleMax = false
  EnableAngleMin = false
  EnableLengthMax = false
  EnableLengthMin = false
  JointType = 0 (Fixed)
  LengthMax = 0
  LengthMin = 0
  Placement1 = pos=(4,36,20) rot=(0,0,1;0rad)
  Placement2 = pos=(29,41,0) rot=(0,0,1;0rad)
  Reference1 = -> Assembly002 [Body085.Edge130,Body085.Edge130]
  Reference2 = -> Assembly002 [Body087.Edge42,Body087.Edge42]
FEATURE [App::FeaturePython] Joint002  label="Fixe002"  # Assembly joint (typed FeaturePython)
  Activated = true
  AngleMax = 0
  AngleMin = 0
  Detach1 = false
  Detach2 = false
  Distance = 0
  Distance2 = 0
  EnableAngleMax = false
  EnableAngleMin = false
  EnableLengthMax = false
  EnableLengthMin = false
  JointType = 0 (Fixed)
  LengthMax = 0
  LengthMin = 0
  Placement1 = pos=(3.5,16.75,0) rot=(0,0,1;0rad)
  Placement2 = pos=(3.5,16.75,8) rot=(0,0,1;0rad)
  Reference1 = -> Assembly002 [Body083.Edge25,Body083.Edge25]
  Reference2 = -> Assembly002 [Body087.Edge56,Body087.Edge56]
FEATURE [App::FeaturePython] Joint003  label="Fixe003"  # Assembly joint (typed FeaturePython)
  Activated = true
  AngleMax = 0
  AngleMin = 0
  Detach1 = false
  Detach2 = false
  Distance = 0
  Distance2 = 0
  EnableAngleMax = false
  EnableAngleMin = false
  EnableLengthMax = false
  EnableLengthMin = false
  JointType = 0 (Fixed)
  LengthMax = 0
  LengthMin = 0
  Placement1 = pos=(-34.5,13.9,6) rot=(0.57735,0.57735,0.57735;4.18879rad)
  Placement2 = pos=(31,54.5,2) rot=(0,0,1;0rad)
  Reference1 = -> Assembly002 [Part002004.Part__Feature005.Edge1102,Part002004.Part__Feature005.Edge1102]
  Reference2 = -> Assembly002 [Body085.Edge46,Body085.Edge46]
FEATURE [App::FeaturePython] Joint004  label="Glissière"  # Assembly joint (typed FeaturePython)
  Activated = true
  AngleMax = 0
  AngleMin = 0
  Detach1 = false
  Detach2 = false
  Distance = 0
  Distance2 = 0
  EnableAngleMax = false
  EnableAngleMin = false
  EnableLengthMax = false
  EnableLengthMin = false
  JointType = 3 (Slider)
  LengthMax = 0
  LengthMin = 0
  Placement1 = pos=(0,2,4) rot=(0.707107,0,0.707107;3.14159rad)
  Placement2 = pos=(-10.75,48.0531,0) rot=(0.57735,0.57735,0.57735;4.18879rad)
  Reference1 = -> Assembly002 [Body087.Edge64,Body087.Vertex12]
  Reference2 = -> Assembly002 [Link004.Edge14,Link004.Edge14]
FEATURE [App::FeaturePython] Joint005  label="Pivot"  # Assembly joint (typed FeaturePython)
  Activated = true
  AngleMax = 0
  AngleMin = -71
  Detach1 = false
  Detach2 = false
  Distance = 0
  Distance2 = 0
  EnableAngleMax = false
  EnableAngleMin = false
  EnableLengthMax = false
  EnableLengthMin = false
  JointType = 1 (Revolute)
  LengthMax = 0
  LengthMin = 0
  Placement1 = pos=(0,0,5.5) rot=(0,0,1;0rad)
  Placement2 = pos=(0,0,0.897999) rot=(0,0,1;0rad)
  Reference1 = -> Assembly002 [Body086.Edge300,Body086.Edge300]
  Reference2 = -> Assembly002 [Part002004.Screw005.Edge22,Part002004.Screw005.Edge22]
FEATURE [App::FeaturePython] Joint006  label="Glissière001"  # Assembly joint (typed FeaturePython)
  Activated = true
  AngleMax = 0
  AngleMin = 0
  Detach1 = false
  Detach2 = false
  Distance = 0
  Distance2 = 0
  EnableAngleMax = false
  EnableAngleMin = false
  EnableLengthMax = false
  EnableLengthMin = false
  JointType = 3 (Slider)
  LengthMax = 0
  LengthMin = 0
  Placement1 = pos=(-10.75,48.0531,0) rot=(0.57735,0.57735,0.57735;4.18879rad)
  Placement2 = pos=(50,48,4) rot=(0.707107,0,0.707107;3.14159rad)
  Reference1 = -> Assembly002 [Body084.Edge14,Body084.Edge14]
  Reference2 = -> Assembly002 [Body087.Edge46,Body087.Edge46]
FEATURE [App::FeaturePython] Joint007  label="Fixe004"  # Assembly joint (typed FeaturePython)
  Activated = true
  AngleMax = 0
  AngleMin = 0
  Detach1 = false
  Detach2 = false
  Distance = 0
  Distance2 = 0
  EnableAngleMax = false
  EnableAngleMin = false
  EnableLengthMax = false
  EnableLengthMin = false
  JointType = 0 (Fixed)
  LengthMax = 0
  LengthMin = 0
  Offset2 = pos=(0,0,0) rot=(0,0,1;1.5708rad)
  Placement1 = pos=(9.25,92.677,40) rot=(0.707107,0,0.707107;3.14159rad)
  Placement2 = pos=(4.5,7.1e-15,3) rot=(-1,0,0;4.71239rad)
  Reference1 = -> Assembly002 [Body084.Edge263,Body084.Edge263]
  Reference2 = -> Assembly002 [Body088.Edge5,Body088.Edge5]
FEATURE [App::FeaturePython] Joint008  label="Fixe005"  # Assembly joint (typed FeaturePython)
  Activated = true
  AngleMax = 0
  AngleMin = 0
  Detach1 = false
  Detach2 = false
  Distance = 0
  Distance2 = 0
  EnableAngleMax = false
  EnableAngleMin = false
  EnableLengthMax = false
  EnableLengthMin = false
  JointType = 0 (Fixed)
  LengthMax = 0
  LengthMin = 0
  Offset2 = pos=(0,0,0) rot=(0,0,1;1.5708rad)
  Placement1 = pos=(4.5,0,3) rot=(-0.57735,-0.57735,0.57735;4.18879rad)
  Placement2 = pos=(9.25,92.677,40) rot=(0.57735,-0.57735,0.57735;4.18879rad)
  Reference1 = -> Assembly002 [Link005.Edge5,Link005.Edge5]
  Reference2 = -> Assembly002 [Link004.Edge263,Link004.Edge263]
FEATURE [App::FeaturePython] Joint009  label="Crémaillère"  # Assembly joint (typed FeaturePython)
  Activated = true
  AngleMax = 0
  AngleMin = 0
  Detach1 = false
  Detach2 = false
  Distance = 11.77
  Distance2 = 0
  EnableAngleMax = false
  EnableAngleMin = false
  EnableLengthMax = false
  EnableLengthMin = false
  JointType = 9 (RackPinion)
  LengthMax = 0
  LengthMin = 0
  Placement1 = pos=(-10.75,33.0531,3) rot=(0.57735,0.57735,0.57735;4.18879rad)
  Reference1 = -> Assembly002 [Body084.Edge8,Body084.Edge8]
  Reference2 = -> Assembly002 [Body086.Edge154,Body086.Edge154]
FEATURE [App::FeaturePython] Joint010  label="Crémaillère001"  # Assembly joint (typed FeaturePython)
  Activated = true
  AngleMax = 0
  AngleMin = 0
  Detach1 = false
  Detach2 = false
  Distance = 11.77
  Distance2 = 0
  EnableAngleMax = false
  EnableAngleMin = false
  EnableLengthMax = false
  EnableLengthMin = false
  JointType = 9 (RackPinion)
  LengthMax = 0
  LengthMin = 0
  Placement1 = pos=(-10.75,33.0531,3) rot=(0.57735,0.57735,0.57735;4.18879rad)
  Reference1 = -> Assembly002 [Link004.Edge8,Link004.Edge8]
  Reference2 = -> Assembly002 [Body086.Edge154,Body086.Edge154]
FEATURE [App::Link] Link004  label="pince_cremaillere_bras003"
  LinkPlacement = pos=(67.1598,7.75,24) rot=(0,0,1;1.5708rad)
  LinkedObject = -> Body084
  Placement = pos=(67.1598,7.75,24) rot=(0,0,1;1.5708rad)
FEATURE [App::Link] Link005  label="mousse003"
  LinkPlacement = pos=(-22.5171,17,59.5) rot=(0,-1,0;1.5708rad)
  LinkedObject = -> Body088
  Placement = pos=(-22.5171,17,59.5) rot=(0,-1,0;1.5708rad)
FEATURE [Part::Feature] Part__Feature003  label="Lever 25T002"
  Placement = pos=(0,0,0) rot=(-1,0,0;1.5708rad)
  shape: bbox 18.84 x 33.03 x 6.019 mm, 125 faces (baked)
FEATURE [Part::Feature] Part__Feature004  label="Axis Servo002"
  Placement = pos=(0,0,0) rot=(-1,0,0;1.5708rad)
  shape: bbox 5 x 5 x 8 mm, 5 faces (baked)
FEATURE [Part::Feature] Part__Feature005  label="Servo DS3218MG002"
  Placement = pos=(0,0,0) rot=(-1,0,0;1.5708rad)
  shape: bbox 55 x 20 x 41 mm, 772 faces (baked)
FEATURE [Part::FeaturePython] Screw005  label="M2x5-Vis001"  # WARN: FeaturePython — macro-defined, semantics opaque (R4)
  BaseObject = -> Body010 [Edge6]
  Diameter = 2
  Invert = true
  LeftHanded = false
  Length = 10
  LengthCustom = 5
  MatchOuter = false
  OffsetAngle = 0
  Placement = pos=(0,1e-15,4.8) rot=(0,0,1;0rad)
  Thread = false
  Type = 76
FEATURE [Sketcher::SketchObject] Sketch242
  ArcFitTolerance = 0
  AttachmentSupport = -> [XY_Plane281]
  FullyConstrained = true
  MakeInternals = false
  MapMode = 2
  sketch-geometry (31):
    g0: LineSegment StartX=0 StartY=50 StartZ=0 EndX=100 EndY=50 EndZ=0
    g1: LineSegment StartX=100 StartY=50 StartZ=0 EndX=100 EndY=48 EndZ=0
    g2: LineSegment StartX=100 StartY=0 StartZ=0 EndX=0 EndY=0 EndZ=0
    g3: LineSegment StartX=0 StartY=0 StartZ=0 EndX=0 EndY=2 EndZ=0
    g4: Circle CenterX=50 CenterY=25 CenterZ=0 NormalX=0 NormalY=0 NormalZ=1 AngleXU=0 Radius=14
    g5: LineSegment [constr] StartX=0 StartY=50 StartZ=0 EndX=100 EndY=0 EndZ=0
    g6: LineSegment [constr] StartX=0 StartY=0 StartZ=0 EndX=100 EndY=50 EndZ=0
    g7: LineSegment [constr] StartX=0 StartY=25 StartZ=0 EndX=100 EndY=25 EndZ=0
    g8: LineSegment [constr] StartX=50 StartY=50 StartZ=0 EndX=50 EndY=0 EndZ=0
    g9: LineSegment [constr] StartX=3.5 StartY=33.25 StartZ=0 EndX=96.5 EndY=33.25 EndZ=0
    g10: LineSegment [constr] StartX=96.5 StartY=33.25 StartZ=0 EndX=96.5 EndY=16.75 EndZ=0
    g11: LineSegment [constr] StartX=96.5 StartY=16.75 StartZ=0 EndX=3.5 EndY=16.75 EndZ=0
    g12: LineSegment [constr] StartX=3.5 StartY=16.75 StartZ=0 EndX=3.5 EndY=33.25 EndZ=0
    g13: Circle CenterX=96.5 CenterY=33.25 CenterZ=0 NormalX=0 NormalY=0 NormalZ=1 AngleXU=0 Radius=1.65
    g14: Circle CenterX=3.5 CenterY=33.25 CenterZ=0 NormalX=0 NormalY=0 NormalZ=1 AngleXU=0 Radius=1.65
    g15: Circle CenterX=3.5 CenterY=16.75 CenterZ=0 NormalX=0 NormalY=0 NormalZ=1 AngleXU=0 Radius=1.65
    g16: Circle CenterX=96.5 CenterY=16.75 CenterZ=0 NormalX=0 NormalY=0 NormalZ=1 AngleXU=0 Radius=1.65
    g17: LineSegment StartX=0 StartY=2 StartZ=0 EndX=30 EndY=2 EndZ=0
    g18: LineSegment StartX=30 StartY=2 StartZ=0 EndX=30 EndY=7.5 EndZ=0
    g19: LineSegment StartX=30 StartY=7.5 StartZ=0 EndX=2.5 EndY=7.5 EndZ=0
    g20: LineSegment StartX=0 StartY=10 StartZ=0 EndX=0 EndY=50 EndZ=0
    g21: LineSegment StartX=100 StartY=48 StartZ=0 EndX=67.5 EndY=48 EndZ=0
    g22: LineSegment StartX=67.5 StartY=48 StartZ=0 EndX=67.5 EndY=42.5 EndZ=0
    g23: LineSegment StartX=67.5 StartY=42.5 StartZ=0 EndX=97.5 EndY=42.5 EndZ=0
    g24: LineSegment StartX=100 StartY=40 StartZ=0 EndX=100 EndY=0 EndZ=0
    g25: ArcOfCircle [constr] CenterX=97.5 CenterY=40 CenterZ=0 NormalX=0 NormalY=0 NormalZ=1 AngleXU=0 Radius=2.5 StartAngle=0 EndAngle=1.5708
    g26: GeomPoint [constr] X=100 Y=42.5 Z=0
    g27: LineSegment StartX=100 StartY=40 StartZ=0 EndX=97.5 EndY=42.5 EndZ=0
    g28: ArcOfCircle [constr] CenterX=2.5 CenterY=10 CenterZ=0 NormalX=0 NormalY=0 NormalZ=1 AngleXU=0 Radius=2.5 StartAngle=3.14159 EndAngle=4.71239
    g29: GeomPoint [constr] X=0 Y=7.5 Z=0
    g30: LineSegment StartX=0 StartY=10 StartZ=0 EndX=2.5 EndY=7.5 EndZ=0
  constraints (78):
    c: Coincident(g0,g1)
    c: Coincident(g24,g2)
    c: Coincident(g2,g3)
    c: Coincident(g20,g0)
    c: Horizontal(g0)
    c: Horizontal(g2)
    c: Vertical(g1)
    c: Vertical(g3)
    c: Coincident(g2,g-1)
    c: Coincident(g5,g0)
    c: Coincident(g2,g6)
    c: Coincident(g0,g6)
    c: Coincident(g24,g5)
    c: PointOnObject(g4,g6)
    c: PointOnObject(g4,g5)
    c: Diameter(g4) = 28
    c: DistanceY(g3,g20) = 50
    c: DistanceX(g2,g2) = 100
    c: PointOnObject(g8,g0)
    c: PointOnObject(g7,g24)
    c: PointOnObject(g7,g20)
    c: PointOnObject(g8,g2)
    c: Symmetric(g0,g0,g8)
    c: Symmetric(g0,g2,g7)
    c: Coincident(g9,g10)
    c: Coincident(g10,g11)
    c: Coincident(g11,g12)
    c: Coincident(g12,g9)
    c: Horizontal(g11)
    c: Vertical(g12)
    c: Symmetric(g9,g10,g7)
    c: Symmetric(g9,g9,g8)
    c: Distance(g12) = 16.5
    c: DistanceX(g0,g9) = 3.5
    c: Coincident(g16,g10)
    c: Coincident(g13,g9)
    c: Coincident(g9,g14)
    c: Coincident(g11,g15)
    c: Equal(g14,g15)
    c: Equal(g14,g13)
    c: Equal(g14,g16)
    c: Diameter(g14) = 3.3
    c: Coincident(g17,g18)
    c: Coincident(g18,g19)
    c: Horizontal(g17)
    c: Horizontal(g19)
    c: Vertical(g18)
    c: Vertical(g20)
    c: DistanceX(g29,g19) = 30
    c: Coincident(g21,g22)
    c: Coincident(g22,g23)
    c: Horizontal(g21)
    c: Horizontal(g23)
    c: Vertical(g22)
    c: Vertical(g24)
    c: Equal(g18,g22)
    c: PointOnObject(g26,g23)
    c: PointOnObject(g26,g24)
    c: Tangent(g23,g25) = 1.5708
    c: Tangent(g24,g25) = 1.5708
    c: Coincident(g27,g23)
    c: Coincident(g27,g24)
    c: PointOnObject(g29,g20)
    c: PointOnObject(g29,g19)
    c: Tangent(g20,g28) = 1.5708
    c: Tangent(g19,g28) = 1.5708
    c: Coincident(g30,g20)
    c: Coincident(g30,g19)
    c: Equal(g1,g3)
    c: Equal(g23,g17)
    c: Coincident(g3,g17)
    c: DistanceY(g3,g3) = 2
    c: Coincident(g1,g21)
    c: Vertical(g1,g24)
    c: Vertical(g29,g3)
    c: DistanceY(g18,g18) = 5.5
    c: Radius(g28) = 2.5
    c: Equal(g25,g28)
FEATURE [PartDesign::Pad] Pad118
  AlongSketchNormal = false
  Direction = (0,0,1)
  Length = 4
  Length2 = 100
  Profile = -> Sketch242
  ReferenceAxis = -> Sketch242 [N_Axis]
  Suppressed = false
  Type = 0
FEATURE [Sketcher::SketchObject] Sketch243
  ArcFitTolerance = 1e-06
  AttachmentOffset = pos=(0,0,4) rot=(0,0,1;0rad)
  AttachmentSupport = -> [XY_Plane281]
  ExternalGeometry = -> [Pad118]
  FullyConstrained = true
  MakeInternals = false
  MapMode = 5
  Placement = pos=(0,0,4) rot=(0,0,1;0rad)
  sketch-geometry (4):
    g0: Circle CenterX=3.5 CenterY=33.25 CenterZ=0 NormalX=0 NormalY=0 NormalZ=1 AngleXU=0 Radius=3.25
    g1: Circle CenterX=3.5 CenterY=16.75 CenterZ=0 NormalX=0 NormalY=0 NormalZ=1 AngleXU=0 Radius=3.25
    g2: Circle CenterX=96.5 CenterY=33.25 CenterZ=0 NormalX=0 NormalY=0 NormalZ=1 AngleXU=0 Radius=3.25
    g3: Circle CenterX=96.5 CenterY=16.75 CenterZ=0 NormalX=0 NormalY=0 NormalZ=1 AngleXU=0 Radius=3.25
  constraints (10):
    c: Coincident(g0,g-3)
    c: Coincident(g1,g-4)
    c: Equal(g0,g1)
    c: Equal(g1,g2)
    c: Equal(g2,g3)
    c: Diameter(g0) = 6.5
    c: Horizontal(g3,g1)
    c: Horizontal(g2,g0)
    c: Vertical(g2,g3)
    c: DistanceX(g1,g3) = 93
FEATURE [PartDesign::Pocket] Pocket099
  BaseFeature = -> Pad118
  Direction = (0,0,-1)
  Length = 2
  Length2 = 5
  Profile = -> Sketch243
  ReferenceAxis = -> Sketch243 [N_Axis]
  Refine = true
  Suppressed = false
  Type = 0
FEATURE [PartDesign::Body] Body083  label="pince_capot001"
  AllowCompound = false
  Group = -> [Sketch242,Pad118,Sketch243,Pocket099]
  Origin = -> Origin284
  Placement = pos=(-25,-5,28) rot=(0,0,1;0rad)
  Tip = -> Pocket099
FEATURE [Sketcher::SketchObject] Sketch244
  ArcFitTolerance = 1e-06
  AttachmentSupport = -> [BaseFeature002]
  FullyConstrained = true
  MakeInternals = false
  MapMode = 5
  Placement = pos=(0,92.677,0) rot=(0,0.707107,0.707107;3.14159rad)
  sketch-geometry (4):
    g0: LineSegment StartX=-29.25 StartY=0 StartZ=0 EndX=10.75 EndY=0 EndZ=0
    g1: LineSegment StartX=10.75 StartY=0 StartZ=0 EndX=10.75 EndY=40 EndZ=0
    g2: LineSegment StartX=10.75 StartY=40 StartZ=0 EndX=-29.25 EndY=40 EndZ=0
    g3: LineSegment StartX=-29.25 StartY=40 StartZ=0 EndX=-29.25 EndY=0 EndZ=0
  constraints (12):
    c: Coincident(g0,g1)
    c: Coincident(g1,g2)
    c: Coincident(g2,g3)
    c: Coincident(g3,g0)
    c: Horizontal(g0)
    c: Horizontal(g2)
    c: Vertical(g1)
    c: Vertical(g3)
    c: DistanceY(g3,g3) = 40
    c: DistanceX(g2,g2) = 40
    c: PointOnObject(g0,g-1)
    c: DistanceX(g-1,g0) = 10.75
FEATURE [PartDesign::Pad] Pad119
  BaseFeature = -> BaseFeature002
  Direction = (0,1,-2e-16)
  Length = 5
  Length2 = 10
  Profile = -> Sketch244
  ReferenceAxis = -> Sketch244 [N_Axis]
  Refine = true
  Suppressed = false
  Type = 0
FEATURE [Sketcher::SketchObject] Sketch245
  ArcFitTolerance = 0
  AttachmentOffset = pos=(0,0,-2) rot=(0,0,1;0rad)
  AttachmentSupport = -> [XY_Plane283]
  FullyConstrained = true
  MakeInternals = false
  MapMode = 2
  Placement = pos=(0,0,-2) rot=(0,0,1;0rad)
  sketch-geometry (18):
    g0: LineSegment StartX=14.5 StartY=50 StartZ=0 EndX=35.5 EndY=50 EndZ=0
    g1: LineSegment StartX=35.5 StartY=50 StartZ=0 EndX=35.5 EndY=9 EndZ=0
    g2: LineSegment StartX=35.5 StartY=9 StartZ=0 EndX=14.5 EndY=9 EndZ=0
    g3: LineSegment StartX=14.5 StartY=9 StartZ=0 EndX=14.5 EndY=50 EndZ=0
    g4: LineSegment StartX=0 StartY=59 StartZ=0 EndX=50 EndY=59 EndZ=0
    g5: LineSegment StartX=50 StartY=59 StartZ=0 EndX=50 EndY=0 EndZ=0
    g6: LineSegment StartX=50 StartY=0 StartZ=0 EndX=0 EndY=0 EndZ=0
    g7: LineSegment StartX=0 StartY=0 StartZ=0 EndX=0 EndY=59 EndZ=0
    g8: Circle CenterX=19 CenterY=54.5 CenterZ=0 NormalX=0 NormalY=0 NormalZ=1 AngleXU=0 Radius=1.65
    g9: Circle CenterX=31 CenterY=54.5 CenterZ=0 NormalX=0 NormalY=0 NormalZ=1 AngleXU=0 Radius=1.65
    g10: Circle CenterX=19 CenterY=4.5 CenterZ=0 NormalX=0 NormalY=0 NormalZ=1 AngleXU=0 Radius=1.65
    g11: Circle CenterX=31 CenterY=4.5 CenterZ=0 NormalX=0 NormalY=0 NormalZ=1 AngleXU=0 Radius=1.65
    g12: LineSegment [constr] StartX=19 StartY=54.5 StartZ=0 EndX=31 EndY=54.5 EndZ=0
    g13: LineSegment [constr] StartX=31 StartY=54.5 StartZ=0 EndX=31 EndY=4.5 EndZ=0
    g14: LineSegment [constr] StartX=31 StartY=4.5 StartZ=0 EndX=19 EndY=4.5 EndZ=0
    g15: LineSegment [constr] StartX=19 StartY=4.5 StartZ=0 EndX=19 EndY=54.5 EndZ=0
    g16: LineSegment [constr] StartX=14.5 StartY=29.5 StartZ=0 EndX=35.5 EndY=29.5 EndZ=0
    g17: LineSegment [constr] StartX=25 StartY=50 StartZ=0 EndX=25 EndY=9 EndZ=0
  constraints (46):
    c: Coincident(g0,g1)
    c: Coincident(g1,g2)
    c: Coincident(g2,g3)
    c: Coincident(g3,g0)
    c: Horizontal(g0)
    c: Horizontal(g2)
    c: Vertical(g1)
    c: Vertical(g3)
    c: Coincident(g4,g5)
    c: Coincident(g5,g6)
    c: Coincident(g6,g7)
    c: Coincident(g7,g4)
    c: Horizontal(g6)
    c: Vertical(g5)
    c: Coincident(g12,g13)
    c: Coincident(g13,g14)
    c: Coincident(g14,g15)
    c: Coincident(g15,g12)
    c: Horizontal(g14)
    c: Vertical(g15)
    c: Coincident(g10,g14)
    c: Coincident(g11,g13)
    c: Coincident(g8,g12)
    c: Coincident(g9,g12)
    c: PointOnObject(g17,g0)
    c: PointOnObject(g17,g2)
    c: PointOnObject(g16,g3)
    c: PointOnObject(g16,g1)
    c: Symmetric(g0,g0,g17)
    c: Symmetric(g2,g0,g16)
    c: Symmetric(g9,g8,g17)
    c: DistanceX(g2,g2) = 21
    c: DistanceY(g3,g3) = 41
    c: DistanceX(g14,g14) = 12
    c: DistanceY(g13,g13) = 50
    c: Equal(g9,g8)
    c: Equal(g9,g11)
    c: Equal(g9,g10)
    c: Diameter(g9) = 3.3
    c: Symmetric(g9,g11,g16)
    c: Coincident(g-1,g6)
    c: Symmetric(g4,g4,g17)
    c: DistanceX(g6,g2) = 14.5
    c: Vertical(g7)
    c: DistanceY(g5,g5) = 59
    c: DistanceY(g-1,g2) = 9
FEATURE [PartDesign::Pad] Pad120
  AlongSketchNormal = false
  Direction = (0,0,1)
  Length = 4
  Length2 = 100
  Profile = -> Sketch245
  ReferenceAxis = -> Sketch245 [N_Axis]
  Suppressed = false
  Type = 0
FEATURE [Sketcher::SketchObject] Sketch246
  ArcFitTolerance = 0
  AttachmentSupport = -> [Pad120]
  ExternalGeometry = -> [Pad120]
  FullyConstrained = true
  MakeInternals = false
  MapMode = 5
  Placement = pos=(0,0,2) rot=(0,0,1;0rad)
  sketch-geometry (10):
    g0: LineSegment StartX=0 StartY=40 StartZ=0 EndX=8 EndY=40 EndZ=0
    g1: LineSegment StartX=8 StartY=40 StartZ=0 EndX=8 EndY=0 EndZ=0
    g2: LineSegment StartX=8 StartY=0 StartZ=0 EndX=0 EndY=0 EndZ=0
    g3: LineSegment StartX=0 StartY=0 StartZ=0 EndX=0 EndY=40 EndZ=0
    g4: LineSegment StartX=42 StartY=40 StartZ=0 EndX=50 EndY=40 EndZ=0
    g5: LineSegment StartX=50 StartY=40 StartZ=0 EndX=50 EndY=0 EndZ=0
    g6: LineSegment StartX=50 StartY=0 StartZ=0 EndX=42 EndY=0 EndZ=0
    g7: LineSegment StartX=42 StartY=0 StartZ=0 EndX=42 EndY=40 EndZ=0
    g8: LineSegment [constr] StartX=25 StartY=59 StartZ=0 EndX=25 EndY=0 EndZ=0
    g9: LineSegment [constr] StartX=0 StartY=20 StartZ=0 EndX=50 EndY=20 EndZ=0
  constraints (28):
    c: Coincident(g0,g1)
    c: Coincident(g1,g2)
    c: Coincident(g2,g3)
    c: Coincident(g3,g0)
    c: Horizontal(g0)
    c: Horizontal(g2)
    c: Vertical(g3)
    c: Coincident(g4,g5)
    c: Coincident(g5,g6)
    c: Coincident(g6,g7)
    c: Coincident(g7,g4)
    c: Horizontal(g4)
    c: Horizontal(g6)
    c: Vertical(g5)
    c: PointOnObject(g4,g-4)
    c: PointOnObject(g8,g-5)
    c: PointOnObject(g8,g-6)
    c: Symmetric(g-5,g-5,g8)
    c: Symmetric(g0,g4,g8)
    c: DistanceX(g0,g0) = 8
    c: Vertical(g1)
    c: PointOnObject(g9,g3)
    c: PointOnObject(g9,g5)
    c: Symmetric(g0,g1,g9)
    c: Vertical(g7)
    c: PointOnObject(g5,g-1)
    c: DistanceY(g3,g3) = 40
    c: Coincident(g2,g-1)
FEATURE [PartDesign::Pad] Pad121
  AlongSketchNormal = false
  BaseFeature = -> Pad120
  Direction = (0,0,1)
  Length = 18
  Length2 = 100
  Profile = -> Sketch246
  Suppressed = false
  Type = 0
FEATURE [Sketcher::SketchObject] Sketch247
  ArcFitTolerance = 0
  AttachmentSupport = -> [Pad121]
  ExternalGeometry = -> [Pad121]
  FullyConstrained = true
  MakeInternals = false
  MapMode = 5
  Placement = pos=(0,0,20) rot=(0,0,1;0rad)
  sketch-geometry (7):
    g0: LineSegment [constr] StartX=25 StartY=40 StartZ=0 EndX=25 EndY=0 EndZ=0
    g1: LineSegment [constr] StartX=0 StartY=20 StartZ=0 EndX=50 EndY=20 EndZ=0
    g2: Circle CenterX=4 CenterY=36 CenterZ=0 NormalX=0 NormalY=0 NormalZ=1 AngleXU=0 Radius=1.75
    g3: Circle CenterX=46 CenterY=36 CenterZ=0 NormalX=0 NormalY=0 NormalZ=1 AngleXU=0 Radius=1.75
    g4: Circle CenterX=4 CenterY=4 CenterZ=0 NormalX=0 NormalY=0 NormalZ=1 AngleXU=0 Radius=1.75
    g5: Circle CenterX=46 CenterY=4 CenterZ=0 NormalX=0 NormalY=0 NormalZ=1 AngleXU=0 Radius=1.75
    g6: LineSegment [constr] StartX=4 StartY=36 StartZ=0 EndX=4 EndY=4 EndZ=0
  constraints (17):
    c: PointOnObject(g0,g-4)
    c: PointOnObject(g0,g-5)
    c: PointOnObject(g1,g-7)
    c: PointOnObject(g1,g-8)
    c: Symmetric(g-3,g-4,g0)
    c: Symmetric(g-5,g-4,g1)
    c: Symmetric(g4,g2,g1)
    c: Symmetric(g3,g2,g0)
    c: Symmetric(g5,g3,g1)
    c: Equal(g2,g4)
    c: Equal(g2,g3)
    c: Equal(g2,g5)
    c: Radius(g2) = 1.75
    c: Coincident(g6,g4)
    c: Coincident(g6,g2)
    c: Symmetric(g-7,g-5,g6)
    c: DistanceY(g-5,g4) = 4
FEATURE [PartDesign::Pocket] Pocket100
  BaseFeature = -> Pad121
  Direction = (0,0,-1)
  Length = 5
  Length2 = 100
  Profile = -> Sketch247
  Suppressed = false
  Type = 1
FEATURE [Sketcher::SketchObject] Sketch248
  ArcFitTolerance = 0
  AttachmentSupport = -> [Pocket100]
  ExternalGeometry = -> [Pocket100]
  FullyConstrained = true
  MakeInternals = false
  MapMode = 5
  Placement = pos=(50,0,0) rot=(0.57735,0.57735,0.57735;2.0944rad)
  sketch-geometry (7):
    g0: LineSegment [constr] StartX=0 StartY=20 StartZ=0 EndX=40 EndY=0 EndZ=0
    g1: LineSegment [constr] StartX=0 StartY=0 StartZ=0 EndX=40 EndY=20 EndZ=0
    g2: Circle CenterX=12 CenterY=17 CenterZ=0 NormalX=0 NormalY=0 NormalZ=1 AngleXU=0 Radius=1.75
    g3: Circle CenterX=12 CenterY=3 CenterZ=0 NormalX=0 NormalY=0 NormalZ=1 AngleXU=0 Radius=1.75
    g4: Circle CenterX=28 CenterY=3 CenterZ=0 NormalX=0 NormalY=0 NormalZ=1 AngleXU=0 Radius=1.75
    g5: Circle CenterX=28 CenterY=17 CenterZ=0 NormalX=0 NormalY=0 NormalZ=1 AngleXU=0 Radius=1.75
    g6: GeomPoint X=20 Y=10 Z=0
  constraints (19):
    c: Equal(g3,g2)
    c: Equal(g3,g5)
    c: Equal(g3,g4)
    c: Coincident(g0,g-5)
    c: Coincident(g1,g-4)
    c: DistanceX(g-3,g-3) = 40
    c: Horizontal(g2,g5)
    c: Horizontal(g3,g4)
    c: Diameter(g3) = 3.5
    c: Vertical(g3,g2)
    c: Vertical(g5,g4)
    c: PointOnObject(g6,g0)
    c: PointOnObject(g6,g1)
    c: DistanceX(g2,g6) = 8
    c: DistanceY(g6,g2) = 7
    c: Symmetric(g2,g4,g6)
    c: Coincident(g1,g-1)
    c: PointOnObject(g0,g-1)
    c: Vertical(g-4,g0)
FEATURE [PartDesign::Pocket] Pocket101
  BaseFeature = -> Pocket100
  Direction = (-1,0,0)
  Length = 5
  Length2 = 100
  Profile = -> Sketch248
  ReferenceAxis = -> Sketch248 [N_Axis]
  Suppressed = false
  Type = 1
FEATURE [Sketcher::SketchObject] Sketch249
  ArcFitTolerance = 1e-06
  AttachmentSupport = -> [Pocket101]
  ExternalGeometry = -> [Pocket101]
  FullyConstrained = true
  MakeInternals = false
  MapMode = 5
  Placement = pos=(50,0,0) rot=(0.57735,0.57735,0.57735;2.0944rad)
  sketch-geometry (4):
    g0: Circle CenterX=12 CenterY=17 CenterZ=0 NormalX=0 NormalY=0 NormalZ=1 AngleXU=0 Radius=2.125
    g1: Circle CenterX=28 CenterY=17 CenterZ=0 NormalX=0 NormalY=0 NormalZ=1 AngleXU=0 Radius=2.125
    g2: Circle CenterX=28 CenterY=3 CenterZ=0 NormalX=0 NormalY=0 NormalZ=1 AngleXU=0 Radius=2.125
    g3: Circle CenterX=12 CenterY=3 CenterZ=0 NormalX=0 NormalY=0 NormalZ=1 AngleXU=0 Radius=2.125
  constraints (8):
    c: Equal(g0,g1)
    c: Equal(g1,g3)
    c: Equal(g3,g2)
    c: Diameter(g0) = 4.25
    c: Coincident(g0,g-3)
    c: Coincident(g-4,g1)
    c: Coincident(g-5,g2)
    c: Coincident(g-6,g3)
FEATURE [PartDesign::Pocket] Pocket102
  BaseFeature = -> Pocket101
  Direction = (-1,0,0)
  Length = 1.5
  Length2 = 5
  Profile = -> Sketch249
  ReferenceAxis = -> Sketch249 [N_Axis]
  Refine = true
  Suppressed = false
  Type = 0
FEATURE [Sketcher::SketchObject] Sketch250
  ArcFitTolerance = 1e-06
  AttachmentSupport = -> [Pocket102]
  ExternalGeometry = -> [Pocket102]
  FullyConstrained = true
  MakeInternals = false
  MapMode = 5
  Placement = pos=(0,0,0) rot=(0.57735,-0.57735,-0.57735;2.0944rad)
  sketch-geometry (4):
    g0: Circle CenterX=-28 CenterY=17 CenterZ=0 NormalX=0 NormalY=0 NormalZ=1 AngleXU=0 Radius=2.1
    g1: Circle CenterX=-12 CenterY=17 CenterZ=0 NormalX=0 NormalY=0 NormalZ=1 AngleXU=0 Radius=2.1
    g2: Circle CenterX=-12 CenterY=3 CenterZ=0 NormalX=0 NormalY=0 NormalZ=1 AngleXU=0 Radius=2.1
    g3: Circle CenterX=-28 CenterY=3 CenterZ=0 NormalX=0 NormalY=0 NormalZ=1 AngleXU=0 Radius=2.1
  constraints (8):
    c: Equal(g0,g1)
    c: Equal(g1,g3)
    c: Equal(g3,g2)
    c: Diameter(g0) = 4.2
    c: Coincident(g0,g-3)
    c: Coincident(g-4,g1)
    c: Coincident(g-5,g2)
    c: Coincident(g3,g-6)
FEATURE [PartDesign::Pocket] Pocket103
  BaseFeature = -> Pocket102
  Direction = (1,0,0)
  Length = 1.5
  Length2 = 5
  Profile = -> Sketch250
  ReferenceAxis = -> Sketch250 [N_Axis]
  Refine = true
  Suppressed = false
  Type = 0
FEATURE [Sketcher::SketchObject] Sketch251
  ArcFitTolerance = 1e-06
  AttachmentSupport = -> [Pocket103]
  ExternalGeometry = -> [Pocket103]
  FullyConstrained = true
  MakeInternals = false
  MapMode = 5
  Placement = pos=(0,0,20) rot=(0,0,1;0rad)
  sketch-geometry (4):
    g0: Circle CenterX=4 CenterY=36 CenterZ=0 NormalX=0 NormalY=0 NormalZ=1 AngleXU=0 Radius=2.1
    g1: Circle CenterX=46 CenterY=36 CenterZ=0 NormalX=0 NormalY=0 NormalZ=1 AngleXU=0 Radius=2.1
    g2: Circle CenterX=4 CenterY=4 CenterZ=0 NormalX=0 NormalY=0 NormalZ=1 AngleXU=0 Radius=2.1
    g3: Circle CenterX=46 CenterY=4 CenterZ=0 NormalX=0 NormalY=0 NormalZ=1 AngleXU=0 Radius=2.1
  constraints (8):
    c: Coincident(g0,g-3)
    c: Coincident(g1,g-6)
    c: Coincident(g2,g-4)
    c: Coincident(g3,g-5)
    c: Equal(g0,g2)
    c: Equal(g2,g1)
    c: Equal(g1,g3)
    c: Diameter(g0) = 4.2
FEATURE [PartDesign::Pocket] Pocket104
  BaseFeature = -> Pocket103
  Direction = (0,0,-1)
  Length = 1.5
  Length2 = 5
  Profile = -> Sketch251
  ReferenceAxis = -> Sketch251 [N_Axis]
  Refine = true
  Suppressed = false
  Type = 0
FEATURE [Sketcher::SketchObject] Sketch252
  ArcFitTolerance = 1e-06
  AttachmentSupport = -> [Pocket104]
  ExternalGeometry = -> [Pocket104]
  FullyConstrained = true
  MakeInternals = false
  MapMode = 5
  Placement = pos=(0,0,-2) rot=(1,0,0;3.14159rad)
  sketch-geometry (4):
    g0: Circle CenterX=4 CenterY=-4 CenterZ=0 NormalX=0 NormalY=0 NormalZ=1 AngleXU=0 Radius=2.1
    g1: Circle CenterX=46 CenterY=-4 CenterZ=0 NormalX=0 NormalY=0 NormalZ=1 AngleXU=0 Radius=2.1
    g2: Circle CenterX=46 CenterY=-36 CenterZ=0 NormalX=0 NormalY=0 NormalZ=1 AngleXU=0 Radius=2.1
    g3: Circle CenterX=4 CenterY=-36 CenterZ=0 NormalX=0 NormalY=0 NormalZ=1 AngleXU=0 Radius=2.1
  constraints (8):
    c: Coincident(g0,g-3)
    c: Coincident(g1,g-5)
    c: Coincident(g2,g-6)
    c: Coincident(g3,g-4)
    c: Equal(g0,g1)
    c: Equal(g1,g2)
    c: Equal(g2,g3)
    c: Diameter(g0) = 4.2
FEATURE [PartDesign::Pocket] Pocket105
  BaseFeature = -> Pocket104
  Direction = (0,0,1)
  Length = 1.5
  Length2 = 5
  Profile = -> Sketch252
  ReferenceAxis = -> Sketch252 [N_Axis]
  Refine = true
  Suppressed = false
  Type = 0
FEATURE [PartDesign::Body] Body085  label="pince_support_servo001"
  AllowCompound = false
  Group = -> [Sketch245,Pad120,Sketch246,Pad121,Sketch247,Pocket100,Sketch248,Pocket101,Sketch249,Pocket102,Sketch250,Pocket103,Sketch251,Pocket104,Sketch252,Pocket105]
  Origin = -> Origin286
  Tip = -> Pocket105
FEATURE [App::FeaturePython] GroundedJoint001  # Assembly grounded joint (typed FeaturePython)
  ObjectToGround = -> Body085
FEATURE [Assembly::JointGroup] Joints002
  Group = -> [GroundedJoint001,Joint001,Joint002,Joint003,Joint004,Joint005,Joint006,Joint007,Joint008,Joint009,Joint010]
FEATURE [Sketcher::SketchObject] Sketch253
  ArcFitTolerance = 0
  FullyConstrained = true
  MakeInternals = false
  MapMode = 5
  Placement = pos=(0,0,5.5) rot=(0,0,1;0rad)
  sketch-geometry (8):
    g0: Circle [constr] CenterX=0 CenterY=0 CenterZ=0 NormalX=0 NormalY=0 NormalZ=1 AngleXU=0 Radius=7
    g1: Circle CenterX=0 CenterY=7 CenterZ=0 NormalX=0 NormalY=0 NormalZ=1 AngleXU=0 Radius=1.65
    g2: Circle CenterX=-7 CenterY=0 CenterZ=0 NormalX=0 NormalY=0 NormalZ=1 AngleXU=0 Radius=1.65
    g3: Circle CenterX=7 CenterY=0 CenterZ=0 NormalX=0 NormalY=0 NormalZ=1 AngleXU=0 Radius=1.65
    g4: Circle CenterX=0 CenterY=-7 CenterZ=0 NormalX=0 NormalY=0 NormalZ=1 AngleXU=0 Radius=1.65
    g5: Circle CenterX=0 CenterY=0 CenterZ=0 NormalX=0 NormalY=0 NormalZ=1 AngleXU=0 Radius=3
    g6: LineSegment [constr] StartX=-7 StartY=0 StartZ=0 EndX=7 EndY=0 EndZ=0
    g7: LineSegment [constr] StartX=0 StartY=7 StartZ=0 EndX=0 EndY=-7 EndZ=0
  constraints (20):
    c: Coincident(g5,g0)
    c: Coincident(g5,g-1)
    c: PointOnObject(g2,g0)
    c: PointOnObject(g1,g0)
    c: PointOnObject(g3,g0)
    c: PointOnObject(g4,g0)
    c: Coincident(g2,g6)
    c: Coincident(g1,g7)
    c: Coincident(g6,g3)
    c: Coincident(g7,g4)
    c: PointOnObject(g5,g7)
    c: PointOnObject(g5,g6)
    c: Perpendicular(g7,g6)
    c: Equal(g1,g3)
    c: Equal(g1,g2)
    c: Equal(g1,g4)
    c: Diameter(g1) = 3.3
    c: Diameter(g5) = 6
    c: Diameter(g0) = 14
    c: PointOnObject(g2,g-1)
FEATURE [PartDesign::Pocket] Pocket106
  BaseFeature = -> BaseFeature003
  Direction = (0,0,-1)
  Length = 5
  Length2 = 100
  Profile = -> Sketch253
  Suppressed = false
  Type = 1
FEATURE [Sketcher::SketchObject] Sketch254
  ArcFitTolerance = 0
  AttachmentSupport = -> [Pocket106]
  ExternalGeometry = -> [Pocket106]
  FullyConstrained = true
  MakeInternals = false
  MapMode = 5
  Placement = pos=(0,0,0) rot=(1,0,0;3.14159rad)
  sketch-geometry (4):
    g0: Circle CenterX=0 CenterY=-7 CenterZ=0 NormalX=0 NormalY=0 NormalZ=1 AngleXU=0 Radius=3.25
    g1: Circle CenterX=-7 CenterY=0 CenterZ=0 NormalX=0 NormalY=0 NormalZ=1 AngleXU=0 Radius=3.25
    g2: Circle CenterX=7 CenterY=0 CenterZ=0 NormalX=0 NormalY=0 NormalZ=1 AngleXU=0 Radius=3.25
    g3: Circle CenterX=0 CenterY=7 CenterZ=0 NormalX=0 NormalY=0 NormalZ=1 AngleXU=0 Radius=3.25
  constraints (8):
    c: Coincident(g1,g-5)
    c: Coincident(g0,g-3)
    c: Coincident(g2,g-4)
    c: Coincident(g3,g-6)
    c: Equal(g2,g0)
    c: Equal(g2,g1)
    c: Equal(g2,g3)
    c: Diameter(g2) = 6.5
FEATURE [PartDesign::Pocket] Pocket107
  BaseFeature = -> Pocket106
  Direction = (0,0,1)
  Length = 3.5
  Length2 = 100
  Profile = -> Sketch254
  Suppressed = false
  Type = 0
FEATURE [PartDesign::Body] Body086  label="pince_cremaillere_pignon001"
  AllowCompound = false
  BaseFeature = -> InvoluteGear001
  Group = -> [BaseFeature003,Sketch253,Pocket106,Sketch254,Pocket107]
  Origin = -> Origin287
  Placement = pos=(25,20,27.098) rot=(0.715163,-0.698958,0;3.14159rad)
  Tip = -> Pocket107
FEATURE [Sketcher::SketchObject] Sketch255
  ArcFitTolerance = 0
  FullyConstrained = true
  MakeInternals = false
  MapMode = 2
  sketch-geometry (25):
    g0: LineSegment StartX=0 StartY=50 StartZ=0 EndX=100 EndY=50 EndZ=0
    g1: LineSegment StartX=100 StartY=50 StartZ=0 EndX=100 EndY=0 EndZ=0
    g2: LineSegment StartX=100 StartY=0 StartZ=0 EndX=0 EndY=0 EndZ=0
    g3: LineSegment StartX=0 StartY=0 StartZ=0 EndX=0 EndY=50 EndZ=0
    g4: Circle CenterX=50 CenterY=25 CenterZ=0 NormalX=0 NormalY=0 NormalZ=1 AngleXU=0 Radius=14
    g5: LineSegment [constr] StartX=0 StartY=50 StartZ=0 EndX=100 EndY=0 EndZ=0
    g6: LineSegment [constr] StartX=0 StartY=0 StartZ=0 EndX=100 EndY=50 EndZ=0
    g7: LineSegment [constr] StartX=29 StartY=41 StartZ=0 EndX=71 EndY=41 EndZ=0
    g8: LineSegment [constr] StartX=71 StartY=41 StartZ=0 EndX=71 EndY=9 EndZ=0
    g9: LineSegment [constr] StartX=71 StartY=9 StartZ=0 EndX=29 EndY=9 EndZ=0
    g10: LineSegment [constr] StartX=29 StartY=9 StartZ=0 EndX=29 EndY=41 EndZ=0
    g11: Circle CenterX=29 CenterY=41 CenterZ=0 NormalX=0 NormalY=0 NormalZ=1 AngleXU=0 Radius=1.75
    g12: Circle CenterX=71 CenterY=41 CenterZ=0 NormalX=0 NormalY=0 NormalZ=1 AngleXU=0 Radius=1.75
    g13: Circle CenterX=71 CenterY=9 CenterZ=0 NormalX=0 NormalY=0 NormalZ=1 AngleXU=0 Radius=1.75
    g14: Circle CenterX=29 CenterY=9 CenterZ=0 NormalX=0 NormalY=0 NormalZ=1 AngleXU=0 Radius=1.75
    g15: LineSegment [constr] StartX=0 StartY=25 StartZ=0 EndX=100 EndY=25 EndZ=0
    g16: LineSegment [constr] StartX=50 StartY=50 StartZ=0 EndX=50 EndY=0 EndZ=0
    g17: LineSegment [constr] StartX=3.5 StartY=33.25 StartZ=0 EndX=96.5 EndY=33.25 EndZ=0
    g18: LineSegment [constr] StartX=96.5 StartY=33.25 StartZ=0 EndX=96.5 EndY=16.75 EndZ=0
    g19: LineSegment [constr] StartX=96.5 StartY=16.75 StartZ=0 EndX=3.5 EndY=16.75 EndZ=0
    g20: LineSegment [constr] StartX=3.5 StartY=16.75 StartZ=0 EndX=3.5 EndY=33.25 EndZ=0
    g21: Circle CenterX=96.5 CenterY=33.25 CenterZ=0 NormalX=0 NormalY=0 NormalZ=1 AngleXU=0 Radius=1.65
    g22: Circle CenterX=3.5 CenterY=33.25 CenterZ=0 NormalX=0 NormalY=0 NormalZ=1 AngleXU=0 Radius=1.65
    g23: Circle CenterX=3.5 CenterY=16.75 CenterZ=0 NormalX=0 NormalY=0 NormalZ=1 AngleXU=0 Radius=1.65
    g24: Circle CenterX=96.5 CenterY=16.75 CenterZ=0 NormalX=0 NormalY=0 NormalZ=1 AngleXU=0 Radius=1.65
  constraints (60):
    c: Coincident(g0,g1)
    c: Coincident(g1,g2)
    c: Coincident(g2,g3)
    c: Coincident(g3,g0)
    c: Horizontal(g0)
    c: Horizontal(g2)
    c: Vertical(g1)
    c: Vertical(g3)
    c: Coincident(g2,g-1)
    c: Coincident(g5,g0)
    c: Coincident(g2,g6)
    c: Coincident(g0,g6)
    c: Coincident(g1,g5)
    c: PointOnObject(g4,g6)
    c: PointOnObject(g4,g5)
    c: Diameter(g4) = 28
    c: DistanceY(g3,g3) = 50
    c: DistanceX(g2,g2) = 100
    c: Coincident(g7,g8)
    c: Coincident(g8,g9)
    c: Coincident(g9,g10)
    c: Coincident(g10,g7)
    c: Horizontal(g7)
    c: Vertical(g10)
    c: Coincident(g11,g7)
    c: Coincident(g7,g12)
    c: Coincident(g9,g14)
    c: Coincident(g8,g13)
    c: Equal(g11,g12)
    c: Equal(g11,g14)
    c: Equal(g11,g13)
    c: Radius(g11) = 1.75
    c: DistanceY(g10,g10) = 32
    c: DistanceX(g7,g7) = 42
    c: PointOnObject(g16,g0)
    c: PointOnObject(g15,g1)
    c: PointOnObject(g15,g3)
    c: PointOnObject(g16,g2)
    c: Symmetric(g0,g0,g16)
    c: Symmetric(g0,g2,g15)
    c: Symmetric(g14,g13,g16)
    c: Symmetric(g12,g13,g15)
    c: Coincident(g17,g18)
    c: Coincident(g18,g19)
    c: Coincident(g19,g20)
    c: Coincident(g20,g17)
    c: Horizontal(g19)
    c: Vertical(g20)
    c: Symmetric(g17,g18,g15)
    c: Symmetric(g17,g17,g16)
    c: Distance(g20) = 16.5
    c: DistanceX(g0,g17) = 3.5
    c: Coincident(g24,g18)
    c: Coincident(g21,g17)
    c: Coincident(g17,g22)
    c: Coincident(g19,g23)
    c: Equal(g22,g23)
    c: Equal(g22,g21)
    c: Equal(g22,g24)
    c: Diameter(g22) = 3.3
FEATURE [PartDesign::Pad] Pad122
  AlongSketchNormal = false
  Direction = (0,0,1)
  Length = 8
  Length2 = 100
  Profile = -> Sketch255
  Suppressed = false
  Type = 0
FEATURE [Sketcher::SketchObject] Sketch256
  ArcFitTolerance = 0
  AttachmentSupport = -> [Pad122]
  ExternalGeometry = -> [Pad122]
  FullyConstrained = true
  MakeInternals = false
  MapMode = 5
  Placement = pos=(0,0,8) rot=(0,0,1;0rad)
  sketch-geometry (9):
    g0: LineSegment StartX=0 StartY=48 StartZ=0 EndX=100 EndY=48 EndZ=0
    g1: LineSegment StartX=100 StartY=48 StartZ=0 EndX=100 EndY=35.75 EndZ=0
    g2: LineSegment StartX=100 StartY=35.75 StartZ=0 EndX=0 EndY=35.75 EndZ=0
    g3: LineSegment StartX=0 StartY=35.75 StartZ=0 EndX=0 EndY=48 EndZ=0
    g4: LineSegment StartX=0 StartY=2 StartZ=0 EndX=100 EndY=2 EndZ=0
    g5: LineSegment StartX=100 StartY=2 StartZ=0 EndX=100 EndY=14.25 EndZ=0
    g6: LineSegment StartX=100 StartY=14.25 StartZ=0 EndX=0 EndY=14.25 EndZ=0
    g7: LineSegment StartX=0 StartY=14.25 StartZ=0 EndX=0 EndY=2 EndZ=0
    g8: Circle [constr] CenterX=50 CenterY=25 CenterZ=0 NormalX=0 NormalY=0 NormalZ=1 AngleXU=0 Radius=10.75
  constraints (26):
    c: Coincident(g0,g1)
    c: Coincident(g1,g2)
    c: Coincident(g2,g3)
    c: Coincident(g3,g0)
    c: Horizontal(g0)
    c: Horizontal(g2)
    c: Vertical(g1)
    c: Vertical(g3)
    c: Coincident(g4,g5)
    c: Coincident(g5,g6)
    c: Coincident(g6,g7)
    c: Coincident(g7,g4)
    c: Horizontal(g4)
    c: Horizontal(g6)
    c: Vertical(g5)
    c: Vertical(g7)
    c: PointOnObject(g6,g-6)
    c: PointOnObject(g2,g-6)
    c: PointOnObject(g1,g-5)
    c: PointOnObject(g5,g-5)
    c: Coincident(g8,g-7)
    c: Diameter(g8) = 21.5
    c: Tangent(g8,g2)
    c: Tangent(g6,g8)
    c: Equal(g7,g3)
    c: DistanceY(g0,g-6) = 2
FEATURE [PartDesign::Pocket] Pocket108
  BaseFeature = -> Pad122
  Direction = (0,0,-1)
  Length = 4
  Length2 = 100
  Profile = -> Sketch256
  Suppressed = false
  Type = 0
FEATURE [Sketcher::SketchObject] Sketch257
  ArcFitTolerance = 0
  AttachmentSupport = -> [Pocket108]
  ExternalGeometry = -> [Pocket108]
  FullyConstrained = true
  MakeInternals = false
  MapMode = 5
  Placement = pos=(0,0,8) rot=(0,0,1;0rad)
  sketch-geometry (10):
    g0: ArcOfCircle CenterX=11 CenterY=25 CenterZ=0 NormalX=0 NormalY=0 NormalZ=1 AngleXU=0 Radius=8 StartAngle=1.5708 EndAngle=4.71239
    g1: ArcOfCircle CenterX=26 CenterY=25 CenterZ=0 NormalX=0 NormalY=0 NormalZ=1 AngleXU=0 Radius=8 StartAngle=4.71239 EndAngle=7.85398
    g2: LineSegment StartX=11 StartY=17 StartZ=0 EndX=26 EndY=17 EndZ=0
    g3: LineSegment StartX=26 StartY=33 StartZ=0 EndX=11 EndY=33 EndZ=0
    g4: ArcOfCircle CenterX=74 CenterY=25 CenterZ=0 NormalX=0 NormalY=0 NormalZ=1 AngleXU=0 Radius=8 StartAngle=1.5708 EndAngle=4.71239
    g5: ArcOfCircle CenterX=89 CenterY=25 CenterZ=0 NormalX=0 NormalY=0 NormalZ=1 AngleXU=0 Radius=8 StartAngle=4.71239 EndAngle=7.85398
    g6: LineSegment StartX=74 StartY=17 StartZ=0 EndX=89 EndY=17 EndZ=0
    g7: LineSegment StartX=89 StartY=33 StartZ=0 EndX=74 EndY=33 EndZ=0
    g8: LineSegment [constr] StartX=50 StartY=50 StartZ=0 EndX=50 EndY=0 EndZ=0
    g9: LineSegment [constr] StartX=0 StartY=25 StartZ=0 EndX=100 EndY=25 EndZ=0
  constraints (26):
    c: Tangent(g0,g2) = -1.5708
    c: Tangent(g2,g1) = -1.5708
    c: Tangent(g1,g3) = -1.5708
    c: Tangent(g3,g0) = -1.5708
    c: Equal(g0,g1)
    c: Tangent(g4,g6) = -1.5708
    c: Tangent(g6,g5) = -1.5708
    c: Tangent(g5,g7) = -1.5708
    c: Tangent(g7,g4) = -1.5708
    c: Equal(g4,g5)
    c: PointOnObject(g-7,g9)
    c: PointOnObject(g-7,g8)
    c: PointOnObject(g8,g-6)
    c: PointOnObject(g8,g-5)
    c: PointOnObject(g9,g-3)
    c: PointOnObject(g9,g-4)
    c: Horizontal(g9)
    c: Vertical(g8)
    c: PointOnObject(g0,g9)
    c: PointOnObject(g1,g9)
    c: Symmetric(g1,g4,g8)
    c: Symmetric(g5,g0,g8)
    c: Equal(g1,g4)
    c: DistanceX(g-3,g0) = 11
    c: DistanceX(g1,g8) = 24
    c: DistanceY(g-7,g1) = 8
FEATURE [PartDesign::Pocket] Pocket109
  BaseFeature = -> Pocket108
  Direction = (0,0,-1)
  Length = 5
  Length2 = 100
  Profile = -> Sketch257
  Suppressed = false
  Type = 1
FEATURE [Sketcher::SketchObject] Sketch258
  ArcFitTolerance = 0
  AttachmentSupport = -> [Pocket109]
  ExternalGeometry = -> [Pocket109]
  FullyConstrained = true
  MakeInternals = false
  MapMode = 5
  Placement = pos=(0,0,4) rot=(0,0,1;0rad)
  sketch-geometry (4):
    g0: Circle CenterX=29 CenterY=41 CenterZ=0 NormalX=0 NormalY=0 NormalZ=1 AngleXU=0 Radius=3.5
    g1: Circle CenterX=71 CenterY=41 CenterZ=0 NormalX=0 NormalY=0 NormalZ=1 AngleXU=0 Radius=3.5
    g2: Circle CenterX=29 CenterY=9 CenterZ=0 NormalX=0 NormalY=0 NormalZ=1 AngleXU=0 Radius=3.5
    g3: Circle CenterX=71 CenterY=9 CenterZ=0 NormalX=0 NormalY=0 NormalZ=1 AngleXU=0 Radius=3.5
  constraints (8):
    c: Coincident(g-3,g0)
    c: Coincident(g1,g-4)
    c: Coincident(g2,g-5)
    c: Coincident(g3,g-6)
    c: Equal(g0,g1)
    c: Equal(g0,g2)
    c: Equal(g0,g3)
    c: Diameter(g0) = 7
FEATURE [PartDesign::Pocket] Pocket110
  BaseFeature = -> Pocket109
  Direction = (0,0,-1)
  Length = 2
  Length2 = 100
  Profile = -> Sketch258
  Suppressed = false
  Type = 0
FEATURE [PartDesign::Body] Body087  label="pince_support_cremaillere001"
  AllowCompound = false
  Group = -> [Sketch255,Pad122,Sketch256,Pocket108,Sketch257,Pocket109,Sketch258,Pocket110]
  Origin = -> Origin288
  Placement = pos=(-25,-5,20) rot=(0,0,1;0rad)
  Tip = -> Pocket110
FEATURE [Sketcher::SketchObject] Sketch259
  ArcFitTolerance = 1e-06
  AttachmentSupport = -> [XZ_Plane286]
  FullyConstrained = true
  MakeInternals = false
  MapMode = 5
  Placement = pos=(0,0,0) rot=(1,0,0;1.5708rad)
  sketch-geometry (4):
    g0: LineSegment StartX=-4.5 StartY=0 StartZ=0 EndX=4.5 EndY=0 EndZ=0
    g1: LineSegment StartX=4.5 StartY=0 StartZ=0 EndX=4.5 EndY=3 EndZ=0
    g2: LineSegment StartX=4.5 StartY=3 StartZ=0 EndX=-4.5 EndY=3 EndZ=0
    g3: LineSegment StartX=-4.5 StartY=3 StartZ=0 EndX=-4.5 EndY=0 EndZ=0
  constraints (11):
    c: Coincident(g0,g1)
    c: Coincident(g1,g2)
    c: Coincident(g2,g3)
    c: Coincident(g3,g0)
    c: Horizontal(g0)
    c: Vertical(g1)
    c: Vertical(g3)
    c: PointOnObject(g0,g-1)
    c: Symmetric(g1,g2,g-2)
    c: Distance(g2,g2) = 9
    c: DistanceY(g3,g3) = 3
FEATURE [PartDesign::Pad] Pad123
  Direction = (0,-1,2e-16)
  Length = 40
  Length2 = 10
  Midplane = true
  Placement = pos=(0,0,0) rot=(1,0,0;1.5708rad)
  Profile = -> Sketch259
  ReferenceAxis = -> Sketch259 [N_Axis]
  Suppressed = false
  Type = 0
FEATURE [PartDesign::Body] Body088  label="mousse002"
  AllowCompound = false
  Group = -> [Sketch259,Pad123]
  Origin = -> Origin289
  Placement = pos=(71.5056,23,59.5) rot=(0.707107,0,0.707107;3.14159rad)
  Tip = -> Pad123
FEATURE [Sketcher::SketchObject] Sketch260
  ArcFitTolerance = 0
  AttachmentSupport = -> [XZ_Plane288]
  FullyConstrained = true
  MakeInternals = false
  MapMode = 5
  Placement = pos=(0,0,0) rot=(1,0,0;1.5708rad)
  expr: Constraints[19] = 19.8 / 2
  sketch-geometry (8):
    g0: LineSegment StartX=2.5 StartY=3.4 StartZ=0 EndX=2.5 EndY=0 EndZ=0
    g1: LineSegment StartX=2.5 StartY=0 StartZ=0 EndX=4.2 EndY=0 EndZ=0
    g2: LineSegment StartX=4.2 StartY=0 StartZ=0 EndX=4.2 EndY=2 EndZ=0
    g3: LineSegment StartX=4.2 StartY=2 StartZ=0 EndX=9.9 EndY=2 EndZ=0
    g4: LineSegment StartX=9.9 StartY=2 StartZ=0 EndX=9.9 EndY=4.4 EndZ=0
    g5: LineSegment StartX=9.9 StartY=4.4 StartZ=0 EndX=1.5 EndY=4.4 EndZ=0
    g6: LineSegment StartX=1.5 StartY=4.4 StartZ=0 EndX=1.5 EndY=3.4 EndZ=0
    g7: LineSegment StartX=1.5 StartY=3.4 StartZ=0 EndX=2.5 EndY=3.4 EndZ=0
  constraints (24):
    c: PointOnObject(g0,g-1)
    c: Vertical(g0)
    c: Coincident(g1,g0)
    c: PointOnObject(g1,g-1)
    c: Coincident(g2,g1)
    c: Vertical(g2)
    c: Coincident(g3,g2)
    c: Horizontal(g3)
    c: Coincident(g4,g3)
    c: Vertical(g4)
    c: Coincident(g5,g4)
    c: Horizontal(g5)
    c: Coincident(g6,g5)
    c: Coincident(g7,g6)
    c: Coincident(g7,g0)
    c: Horizontal(g7)
    c: Vertical(g6)
    c: DistanceY(g4,g4) = 2.4
    c: DistanceY(g2,g2) = 2
    c: DistanceX(g-1,g4) = 9.9
    c: DistanceX(g-1,g6) = 1.5
    c: DistanceY(g0,g0) = 3.4
    c: DistanceX(g-1,g0) = 2.5
    c: DistanceX(g1,g1) = 1.7
FEATURE [PartDesign::Revolution] Revolution002
  Angle = 360
  Angle2 = 60
  Axis = (0,2e-16,1)
  Base = (0,0,0)
  Placement = pos=(0,0,0) rot=(1,0,0;1.5708rad)
  Profile = -> Sketch260
  ReferenceAxis = -> Sketch260 [V_Axis]
  Reversed = true
  Suppressed = false
  Type = 0
FEATURE [Sketcher::SketchObject] Sketch261
  ArcFitTolerance = 0
  AttachmentSupport = -> [XY_Plane288]
  FullyConstrained = true
  MakeInternals = false
  MapMode = 5
  sketch-geometry (1):
    g0: Circle CenterX=-7 CenterY=0 CenterZ=0 NormalX=0 NormalY=0 NormalZ=1 AngleXU=0 Radius=1.2
  constraints (3):
    c: PointOnObject(g0,g-1)
    c: Diameter(g0) = 2.4
    c: DistanceX(g0,g-1) = 7
FEATURE [PartDesign::Pocket] Pocket111
  BaseFeature = -> Revolution002
  Direction = (0,0,-1)
  Length = 5
  Length2 = 5
  Midplane = true
  Placement = pos=(0,0,0) rot=(1,0,0;1.5708rad)
  Profile = -> Sketch261
  ReferenceAxis = -> Sketch261 [N_Axis]
  Suppressed = false
  Type = 1
FEATURE [PartDesign::PolarPattern] PolarPattern006
  Angle = 360
  Axis = -> Sketch261 [N_Axis]
  BaseFeature = -> Pocket111
  Mode = 0
  Occurrences = 4
  Offset = 120
  Originals = -> [Pocket111]
  Placement = pos=(0,0,0) rot=(1,0,0;1.5708rad)
  Suppressed = false
  TransformMode = 0
FEATURE [PartDesign::Body] Body010  label="Corps002"
  AllowCompound = false
  Group = -> [Sketch260,Revolution002,Sketch261,Pocket111,PolarPattern006]
  Origin = -> Origin291
  Placement = pos=(0,0,0.4) rot=(0,0,1;0rad)
  Tip = -> PolarPattern006
FEATURE [App::Part] Part002004  label="servo_DS3218MG003"
  Group = -> [Part__Feature003,Part__Feature004,Part__Feature005,Body010,Screw005]
  Origin = -> Origin290
  Placement = pos=(25,20,15.9) rot=(0,0,-1;1.5708rad)
FEATURE [Sketcher::SketchObject] Sketch262
  ArcFitTolerance = 1e-06
  AttachmentOffset = pos=(0,0,-10.75) rot=(0,0,1;0rad)
  AttachmentSupport = -> [YZ_Plane282]
  ExternalGeometry = -> [Pad119]
  FullyConstrained = true
  MakeInternals = false
  MapMode = 5
  Placement = pos=(-10.75,0,0) rot=(0.57735,0.57735,0.57735;2.0944rad)
  sketch-geometry (3):
    g0: LineSegment StartX=67.677 StartY=3 StartZ=0 EndX=92.677 EndY=9 EndZ=0
    g1: LineSegment StartX=67.677 StartY=3 StartZ=0 EndX=92.677 EndY=3 EndZ=0
    g2: LineSegment StartX=92.677 StartY=9 StartZ=0 EndX=92.677 EndY=3 EndZ=0
  constraints (8):
    c: PointOnObject(g0,g-4)
    c: Coincident(g1,g0)
    c: Coincident(g1,g-4)
    c: Coincident(g2,g0)
    c: Coincident(g2,g1)
    c: DistanceX(g1,g1) = 25
    c: Vertical(g2)
    c: DistanceY(g2,g2) = 6
FEATURE [PartDesign::Pad] Pad124
  BaseFeature = -> Pad119
  Direction = (1,0,0)
  Length = 5
  Length2 = 10
  Profile = -> Sketch262
  ReferenceAxis = -> Sketch262 [N_Axis]
  Suppressed = false
  Type = 0
FEATURE [PartDesign::Body] Body084  label="pince_cremaillere_bras002"
  AllowCompound = false
  BaseFeature = -> InvoluteRack001
  Group = -> [BaseFeature002,Sketch244,Pad119,Sketch262,Pad124]
  Origin = -> Origin285
  Placement = pos=(-18.1714,32.25,24) rot=(0,0,-1;1.5708rad)
  Tip = -> Pad124
FEATURE [Sketcher::SketchObject] Sketch263
  ArcFitTolerance = 1e-06
  AttachmentSupport = -> [YZ_Plane289]
  FullyConstrained = true
  MakeInternals = false
  MapMode = 5
  Placement = pos=(0,0,0) rot=(0.57735,0.57735,0.57735;2.0944rad)
  sketch-geometry (20):
    g0: LineSegment StartX=-16.6 StartY=41.5 StartZ=0 EndX=-16.6 EndY=39.5 EndZ=0
    g1: LineSegment StartX=-14.6 StartY=37.5 StartZ=0 EndX=-8.6 EndY=37.5 EndZ=0
    g2: LineSegment StartX=-6.6 StartY=35.5 StartZ=0 EndX=-6.6 EndY=-4.1 EndZ=0
    g3: LineSegment StartX=-4.6 StartY=-6.1 StartZ=0 EndX=0 EndY=-6.1 EndZ=0
    g4: LineSegment StartX=0 StartY=-6.1 StartZ=0 EndX=0 EndY=-0.1 EndZ=0
    g5: LineSegment StartX=0 StartY=-0.1 StartZ=0 EndX=-4.6 EndY=-0.1 EndZ=0
    g6: LineSegment StartX=-4.6 StartY=-0.1 StartZ=0 EndX=-4.6 EndY=6.6 EndZ=0
    g7: LineSegment StartX=-4.6 StartY=6.6 StartZ=0 EndX=0 EndY=6.6 EndZ=0
    g8: LineSegment StartX=0 StartY=6.6 StartZ=0 EndX=0 EndY=41.5 EndZ=0
    g9: LineSegment StartX=0 StartY=41.5 StartZ=0 EndX=-16.6 EndY=41.5 EndZ=0
    g10: ArcOfCircle CenterX=-8.6 CenterY=35.5 CenterZ=0 NormalX=0 NormalY=0 NormalZ=1 AngleXU=0 Radius=2 StartAngle=0 EndAngle=1.5708
    g11: GeomPoint [constr] X=-6.6 Y=37.5 Z=0
    g12: ArcOfCircle CenterX=-4.6 CenterY=-4.1 CenterZ=0 NormalX=0 NormalY=0 NormalZ=1 AngleXU=0 Radius=2 StartAngle=3.14159 EndAngle=4.71239
    g13: GeomPoint [constr] X=-6.6 Y=-6.1 Z=0
    g14: ArcOfCircle CenterX=-14.6 CenterY=39.5 CenterZ=0 NormalX=0 NormalY=0 NormalZ=1 AngleXU=0 Radius=2 StartAngle=3.14159 EndAngle=4.71239
    g15: GeomPoint [constr] X=-16.6 Y=37.5 Z=0
    g16: LineSegment [constr] StartX=-4.5 StartY=6.5 StartZ=0 EndX=-4.5 EndY=0 EndZ=0
    g17: LineSegment [constr] StartX=-4.5 StartY=0 StartZ=0 EndX=0 EndY=0 EndZ=0
    g18: LineSegment [constr] StartX=0 StartY=0 StartZ=0 EndX=0 EndY=6.5 EndZ=0
    g19: LineSegment [constr] StartX=0 StartY=6.5 StartZ=0 EndX=-4.5 EndY=6.5 EndZ=0
  constraints (53):
    c: Vertical(g0)
    c: Horizontal(g1)
    c: Vertical(g2)
    c: PointOnObject(g3,g-2)
    c: Horizontal(g3)
    c: Coincident(g3,g4)
    c: PointOnObject(g4,g-2)
    c: Coincident(g4,g5)
    c: Horizontal(g5)
    c: Vertical(g6)
    c: Coincident(g6,g7)
    c: Horizontal(g7)
    c: Coincident(g7,g8)
    c: Vertical(g8)
    c: Coincident(g8,g9)
    c: Coincident(g9,g0)
    c: Horizontal(g9)
    c: PointOnObject(g7,g-2)
    c: PointOnObject(g11,g1)
    c: PointOnObject(g11,g2)
    c: Tangent(g1,g10) = 1.5708
    c: Tangent(g2,g10) = 1.5708
    c: PointOnObject(g13,g3)
    c: PointOnObject(g13,g2)
    c: Tangent(g3,g12) = -1.5708
    c: Tangent(g2,g12) = -1.5708
    c: PointOnObject(g15,g1)
    c: PointOnObject(g15,g0)
    c: Tangent(g1,g14) = -1.5708
    c: Tangent(g0,g14) = -1.5708
    c: DistanceY(g1,g0) = 4
    c: DistanceX(g0,g2) = 10
    c: Equal(g14,g10)
    c: Radius(g14) = 2
    c: Coincident(g16,g17)
    c: Coincident(g17,g18)
    c: Coincident(g18,g19)
    c: Coincident(g19,g16)
    c: Vertical(g16)
    c: Vertical(g18)
    c: Horizontal(g17)
    c: Horizontal(g19)
    c: Coincident(g17,g-1)
    c: DistanceX(g6,g16) = 0.1
    c: DistanceY(g18,g7) = 0.1
    c: DistanceX(g17,g17) = 4.5
    c: DistanceY(g18,g18) = 6.5
    c: DistanceY(g-1,g8) = 41.5
    c: DistanceY(g4,g4) = 6
    c: DistanceY(g4,g17) = 0.1
    c: Coincident(g5,g6)
    c: Vertical(g12,g5)
    c: Radius(g12) = 2
FEATURE [PartDesign::Pad] Pad125
  Direction = (1,0,0)
  Length = 20
  Length2 = 10
  Midplane = true
  Placement = pos=(0,0,0) rot=(1,1,1;2.0944rad)
  Profile = -> Sketch263
  ReferenceAxis = -> Sketch263 [N_Axis]
  Suppressed = false
  Type = 0
FEATURE [Sketcher::SketchObject] Sketch264
  ArcFitTolerance = 1e-06
  AttachmentSupport = -> [XY_Plane289]
  ExternalGeometry = -> [Pad125]
  FullyConstrained = true
  MakeInternals = false
  MapMode = 5
  Placement = pos=(0,0,0) rot=(0,1,0;3.14159rad)
  sketch-geometry (8):
    g0: Circle CenterX=0 CenterY=-11.6 CenterZ=0 NormalX=0 NormalY=0 NormalZ=1 AngleXU=0 Radius=2.75
    g1: LineSegment [constr] StartX=-5e-16 StartY=-8.6 StartZ=0 EndX=5e-16 EndY=-14.6 EndZ=0
    g2: LineSegment [constr] StartX=4 StartY=-9.6 StartZ=0 EndX=4 EndY=-16.6 EndZ=0
    g3: LineSegment [constr] StartX=4 StartY=-16.6 StartZ=0 EndX=10 EndY=-16.6 EndZ=0
    g4: LineSegment [constr] StartX=10 StartY=-16.6 StartZ=0 EndX=10 EndY=-8.6 EndZ=0
    g5: LineSegment [constr] StartX=10 StartY=-8.6 StartZ=0 EndX=5 EndY=-8.6 EndZ=0
    g6: ArcOfCircle [constr] CenterX=5 CenterY=-9.6 CenterZ=0 NormalX=0 NormalY=0 NormalZ=1 AngleXU=0 Radius=1 StartAngle=1.5708 EndAngle=3.14159
    g7: GeomPoint [constr] X=4 Y=-8.6 Z=0
  constraints (21):
    c: PointOnObject(g1,g-3)
    c: PointOnObject(g1,g-4)
    c: Perpendicular(g-3,g1)
    c: Symmetric(g1,g1,g0)
    c: Diameter(g0) = 5.5
    c: Coincident(g2,g3)
    c: Coincident(g3,g4)
    c: Coincident(g4,g5)
    c: Vertical(g2)
    c: Vertical(g4)
    c: Horizontal(g3)
    c: Horizontal(g5)
    c: Coincident(g3,g-5)
    c: PointOnObject(g7,g5)
    c: PointOnObject(g7,g2)
    c: Tangent(g5,g6) = -1.5708
    c: Tangent(g2,g6) = -1.5708
    c: PointOnObject(g7,g-3)
    c: Radius(g6) = 1
    c: DistanceX(g0,g2) = 4
    c: PointOnObject(g0,g-2)
FEATURE [PartDesign::Pocket] Pocket112
  BaseFeature = -> Pad125
  Direction = (0,0,1)
  Length = 5
  Length2 = 5
  Placement = pos=(0,0,0) rot=(1,1,1;2.0944rad)
  Profile = -> Sketch264
  ReferenceAxis = -> Sketch264 [N_Axis]
  Suppressed = false
  Type = 1
FEATURE [Sketcher::SketchObject] Sketch265
  ArcFitTolerance = 1e-06
  AttachmentOffset = pos=(0,0,-6) rot=(0,0,1;0rad)
  AttachmentSupport = -> [Pocket112]
  FullyConstrained = true
  MakeInternals = false
  MapMode = 5
  Placement = pos=(0,-1.3e-15,-0.1) rot=(0.707107,0.707107,0;3.14159rad)
  sketch-geometry (1):
    g0: Circle CenterX=0 CenterY=-3.5 CenterZ=0 NormalX=0 NormalY=0 NormalZ=1 AngleXU=0 Radius=2.1
  constraints (3):
    c: Diameter(g0) = 4.2
    c: PointOnObject(g0,g-2)
    c: DistanceY(g0,g-1) = 3.5
FEATURE [PartDesign::Pocket] Pocket113
  BaseFeature = -> Pocket112
  Direction = (0,0,1)
  Length = 16
  Length2 = 5
  Placement = pos=(0,0,0) rot=(1,1,1;2.0944rad)
  Profile = -> Sketch265
  ReferenceAxis = -> Sketch265 [N_Axis]
  Reversed = true
  Suppressed = false
  Type = 0
FEATURE [Sketcher::SketchObject] Sketch266
  ArcFitTolerance = 1e-06
  AttachmentSupport = -> [XZ_Plane289]
  ExternalGeometry = -> [Pocket113]
  FullyConstrained = true
  MakeInternals = false
  MapMode = 5
  Placement = pos=(0,0,0) rot=(1,0,0;1.5708rad)
  sketch-geometry (6):
    g0: LineSegment StartX=10 StartY=-6.1 StartZ=0 EndX=10 EndY=35.5 EndZ=0
    g1: LineSegment StartX=10 StartY=35.5 StartZ=0 EndX=2 EndY=-6.1 EndZ=0
    g2: LineSegment StartX=2 StartY=-6.1 StartZ=0 EndX=10 EndY=-6.1 EndZ=0
    g3: LineSegment StartX=-8 StartY=35 StartZ=0 EndX=4.5 EndY=22.5 EndZ=0
    g4: LineSegment StartX=4.5 StartY=22.5 StartZ=0 EndX=-8 EndY=10 EndZ=0
    g5: LineSegment StartX=-8 StartY=35 StartZ=0 EndX=-8 EndY=10 EndZ=0
  constraints (16):
    c: Coincident(g1,g2)
    c: Coincident(g2,g0)
    c: Horizontal(g2)
    c: Coincident(g0,g-4)
    c: Coincident(g0,g-3)
    c: Coincident(g0,g1)
    c: DistanceX(g2,g2) = 8
    c: Coincident(g4,g3)
    c: Coincident(g5,g3)
    c: Coincident(g5,g4)
    c: Vertical(g5)
    c: Angle(g5,g3) = 0.785398
    c: Equal(g3,g4)
    c: DistanceX(g3,g-1) = 8
    c: DistanceY(g-1,g3) = 35
    c: DistanceY(g5,g5) = 25
FEATURE [PartDesign::Pocket] Pocket114
  BaseFeature = -> Pocket113
  Direction = (0,1,-2e-16)
  Length = 5
  Length2 = 5
  Midplane = true
  Placement = pos=(0,0,0) rot=(1,1,1;2.0944rad)
  Profile = -> Sketch266
  ReferenceAxis = -> Sketch266 [N_Axis]
  Suppressed = false
  Type = 1
FEATURE [PartDesign::Mirrored] Mirrored011
  BaseFeature = -> Pocket114
  MirrorPlane = -> XZ_Plane289
  Originals = -> [Pocket114]
  Placement = pos=(0,0,0) rot=(1,1,1;2.0944rad)
  Refine = true
  Suppressed = false
  TransformMode = 1
FEATURE [Sketcher::SketchObject] Sketch
  ArcFitTolerance = 1e-06
  AttachmentSupport = -> [Mirrored011]
  FullyConstrained = true
  MakeInternals = false
  MapMode = 5
  Placement = pos=(0,-5.3e-15,6.6) rot=(0.707107,0.707107,0;3.14159rad)
  sketch-geometry (1):
    g0: Circle CenterX=0 CenterY=-3.5 CenterZ=0 NormalX=0 NormalY=0 NormalZ=1 AngleXU=0 Radius=3.25
  constraints (3):
    c: Diameter(g0) = 6.5
    c: PointOnObject(g0,g-2)
    c: DistanceY(g0,g-1) = 3.5
FEATURE [PartDesign::Pocket] Pocket
  BaseFeature = -> Mirrored011
  Direction = (0,0,1)
  Length = 5
  Length2 = 5
  Placement = pos=(0,0,0) rot=(1,1,1;2.0944rad)
  Profile = -> Sketch
  ReferenceAxis = -> Sketch [N_Axis]
  Suppressed = false
  Type = 1
FEATURE [PartDesign::Body] Body089  label="support_rail_haut001"
  AllowCompound = false
  Group = -> [Sketch263,Pad125,Sketch264,Pocket112,Sketch265,Pocket113,Sketch266,Pocket114,Mirrored011,Sketch,Pocket]
  Origin = -> Origin292
  Placement = pos=(0,-2e-15,218) rot=(-0.707107,0,-0.707107;3.14159rad)
  Tip = -> Pocket
FEATURE [Sketcher::SketchObject] Sketch267
  ArcFitTolerance = 1e-06
  AttachmentSupport = -> [XZ_Plane290]
  FullyConstrained = true
  MakeInternals = false
  MapMode = 5
  Placement = pos=(0,0,0) rot=(1,0,0;1.5708rad)
  sketch-geometry (4):
    g0: LineSegment StartX=-4.5 StartY=0 StartZ=0 EndX=4.5 EndY=0 EndZ=0
    g1: LineSegment StartX=4.5 StartY=0 StartZ=0 EndX=4.5 EndY=2 EndZ=0
    g2: LineSegment StartX=4.5 StartY=2 StartZ=0 EndX=-4.5 EndY=2 EndZ=0
    g3: LineSegment StartX=-4.5 StartY=2 StartZ=0 EndX=-4.5 EndY=0 EndZ=0
  constraints (11):
    c: Coincident(g0,g1)
    c: Coincident(g1,g2)
    c: Coincident(g2,g3)
    c: Coincident(g3,g0)
    c: Horizontal(g0)
    c: Vertical(g1)
    c: Vertical(g3)
    c: PointOnObject(g0,g-1)
    c: Symmetric(g1,g2,g-2)
    c: Distance(g2,g2) = 9
    c: DistanceY(g3,g3) = 2
FEATURE [PartDesign::Pad] Pad126
  Direction = (0,-1,2e-16)
  Length = 40
  Length2 = 10
  Midplane = true
  Placement = pos=(0,0,0) rot=(1,0,0;1.5708rad)
  Profile = -> Sketch267
  ReferenceAxis = -> Sketch267 [N_Axis]
  Suppressed = false
  Type = 0
FEATURE [PartDesign::Body] Body090  label="cale"
  AllowCompound = false
  Group = -> [Sketch267,Pad126]
  Origin = -> Origin293
  Placement = pos=(71.5056,23,59.5) rot=(0.707107,0,0.707107;3.14159rad)
  Tip = -> Pad126
FEATURE [Sketcher::SketchObject] Sketch215
  ArcFitTolerance = 1e-06
  AttachmentSupport = -> [XY_Plane291]
  FullyConstrained = true
  MakeInternals = false
  MapMode = 5
  expr: Constraints[2] = 16.5 mm / 2
  sketch-geometry (5):
    g0: Circle CenterX=-8.25 CenterY=0 CenterZ=0 NormalX=0 NormalY=0 NormalZ=1 AngleXU=0 Radius=2.1
    g1: ArcOfCircle CenterX=-8.25 CenterY=0 CenterZ=0 NormalX=0 NormalY=0 NormalZ=1 AngleXU=0 Radius=3 StartAngle=1.5708 EndAngle=4.71239
    g2: LineSegment StartX=0 StartY=-3 StartZ=0 EndX=-8.25 EndY=-3 EndZ=0
    g3: LineSegment StartX=0 StartY=3 StartZ=0 EndX=-8.25 EndY=3 EndZ=0
    g4: LineSegment StartX=0 StartY=3 StartZ=0 EndX=0 EndY=-3 EndZ=0
  constraints (13):
    c: Diameter(g0) = 4.2
    c: PointOnObject(g0,g-1)
    c: DistanceX(g0,g-1) = 8.25
    c: Tangent(g1,g2) = 1.5708
    c: Tangent(g1,g3) = -1.5708
    c: Horizontal(g3)
    c: Coincident(g1,g0)
    c: PointOnObject(g3,g-2)
    c: PointOnObject(g2,g-2)
    c: Coincident(g4,g3)
    c: Coincident(g4,g2)
    c: Horizontal(g2)
    c: Radius(g1) = 3
FEATURE [PartDesign::Pad] Pad110
  Direction = (0,0,1)
  Length = 15
  Length2 = 10
  Profile = -> Sketch215
  ReferenceAxis = -> Sketch215 [N_Axis]
  Suppressed = false
  Type = 0
FEATURE [Sketcher::SketchObject] Sketch216
  ArcFitTolerance = 1e-06
  AttachmentSupport = -> [XZ_Plane291]
  FullyConstrained = true
  MakeInternals = false
  MapMode = 5
  Placement = pos=(0,0,0) rot=(1,0,0;1.5708rad)
  sketch-geometry (6):
    g0: LineSegment StartX=-3.2536 StartY=15 StartZ=0 EndX=-3.11715 EndY=7.18255 EndZ=0
    g1: LineSegment StartX=0 StartY=6.2 StartZ=0 EndX=-2.1173 EndY=6.2 EndZ=0
    g2: LineSegment StartX=0 StartY=6.2 StartZ=0 EndX=0 EndY=15 EndZ=0
    g3: LineSegment StartX=-3.2536 StartY=15 StartZ=0 EndX=0 EndY=15 EndZ=0
    g4: ArcOfCircle CenterX=-2.1173 CenterY=7.2 CenterZ=0 NormalX=0 NormalY=0 NormalZ=1 AngleXU=0 Radius=1 StartAngle=3.15905 EndAngle=4.71239
    g5: GeomPoint [constr] X=-3.1 Y=6.2 Z=0
  constraints (16):
    c: PointOnObject(g1,g-2)
    c: Coincident(g2,g1)
    c: Vertical(g2)
    c: Coincident(g3,g0)
    c: Coincident(g3,g2)
    c: DistanceY(g-1,g1) = 6.2
    c: Horizontal(g3)
    c: DistanceY(g-1,g0) = 15
    c: Horizontal(g1)
    c: DistanceX(g5,g1) = 3.1
    c: PointOnObject(g5,g0)
    c: PointOnObject(g5,g1)
    c: Tangent(g0,g4) = -1.5708
    c: Tangent(g1,g4) = 1.5708
    c: Angle(g1,g0) = 1.58825
    c: Radius(g4) = 1
FEATURE [PartDesign::Pocket] Pocket079
  BaseFeature = -> Pad110
  Direction = (0,1,-2e-16)
  Length = 5
  Length2 = 5
  Midplane = true
  Profile = -> Sketch216
  ReferenceAxis = -> Sketch216 [N_Axis]
  Suppressed = false
  Type = 1
FEATURE [Sketcher::SketchObject] Sketch268
  ArcFitTolerance = 1e-06
  AttachmentSupport = -> [XZ_Plane291]
  ExternalGeometry = -> [Pocket079]
  FullyConstrained = true
  MakeInternals = false
  MapMode = 5
  Placement = pos=(0,0,0) rot=(1,0,0;1.5708rad)
  sketch-geometry (3):
    g0: LineSegment StartX=-12 StartY=8 StartZ=0 EndX=-5 EndY=15 EndZ=0
    g1: LineSegment StartX=-12 StartY=15 StartZ=0 EndX=-12 EndY=8 EndZ=0
    g2: LineSegment StartX=-5 StartY=15 StartZ=0 EndX=-12 EndY=15 EndZ=0
  constraints (9):
    c: Vertical(g1)
    c: Coincident(g1,g2)
    c: Coincident(g0,g2)
    c: Coincident(g0,g1)
    c: Horizontal(g2)
    c: Horizontal(g2,g-3)
    c: DistanceX(g1,g-1) = 12
    c: Angle(g0,g1) = 0.785398
    c: DistanceX(g2,g2) = 7
FEATURE [PartDesign::Pocket] Pocket115
  BaseFeature = -> Pocket079
  Direction = (0,1,-2e-16)
  Length = 5
  Length2 = 5
  Midplane = true
  Profile = -> Sketch268
  ReferenceAxis = -> Sketch268 [N_Axis]
  Suppressed = false
  Type = 1
FEATURE [PartDesign::Mirrored] Mirrored046
  BaseFeature = -> Pocket115
  MirrorPlane = -> Sketch216 [V_Axis]
  Originals = -> [Pocket079]
  Suppressed = false
  TransformMode = 1
FEATURE [PartDesign::Body] Body091  label="porte_cale"
  AllowCompound = false
  Group = -> [Sketch215,Pad110,Sketch216,Pocket079,Sketch268,Pocket115,Mirrored046]
  Origin = -> Origin294
  Placement = pos=(71.5,19.83,20) rot=(-0.707107,-0.707107,0;3.14159rad)
  Tip = -> Mirrored046
FEATURE [Assembly::AssemblyObject] Assembly002  label="Assembly_pince"
  Group = -> [Joints002,Part002004,Body083,InvoluteRack001,Body084,Body085,InvoluteGear001,Body086,Body087,Body088,Link004,Link005,GroundedJoint001,Joint001,Joint002,Joint003,Joint004,Joint005,Joint006,Joint007,Joint008,Joint009,Joint010,Body090,Body091]
  Origin = -> Origin283
  Placement = pos=(89,81,49.5) rot=(-1,0,0;3.14159rad)
  Type = Assembly
FEATURE [App::Part] Part002003  label="Partie mobile_Z"
  Group = -> [Part,Assembly002]
  Origin = -> Origin282
  Placement = pos=(0,0,56) rot=(0,0,1;0rad)
  expr: .Placement.Base.z = VarSet.Position_verrin + 6 mm
FEATURE [Sketcher::SketchObject] Sketch063
  ArcFitTolerance = 1e-06
  AttachmentSupport = -> [XY_Plane024]
  FullyConstrained = true
  MakeInternals = false
  MapMode = 5
  sketch-geometry (11):
    g0: LineSegment StartX=-3.15 StartY=4.65 StartZ=0 EndX=-3.15 EndY=-4.65 EndZ=0
    g1: LineSegment StartX=-3.15 StartY=-4.65 StartZ=0 EndX=3.15 EndY=-4.65 EndZ=0
    g2: LineSegment StartX=3.15 StartY=-4.65 StartZ=0 EndX=3.15 EndY=4.65 EndZ=0
    g3: LineSegment StartX=3.15 StartY=4.65 StartZ=0 EndX=-3.15 EndY=4.65 EndZ=0
    g4: LineSegment StartX=-6.15 StartY=4.65 StartZ=0 EndX=-6.15 EndY=-4.65 EndZ=0
    g5: LineSegment StartX=-3.15 StartY=-7.65 StartZ=0 EndX=38.5 EndY=-7.65 EndZ=0
    g6: LineSegment StartX=38.5 StartY=-7.65 StartZ=0 EndX=38.5 EndY=7.65 EndZ=0
    g7: LineSegment StartX=38.5 StartY=7.65 StartZ=0 EndX=-3.15 EndY=7.65 EndZ=0
    g8: ArcOfCircle CenterX=-3.15 CenterY=4.65 CenterZ=0 NormalX=0 NormalY=0 NormalZ=1 AngleXU=0 Radius=3 StartAngle=1.5708 EndAngle=3.14159
    g9: ArcOfCircle CenterX=-3.15 CenterY=-4.65 CenterZ=0 NormalX=0 NormalY=0 NormalZ=1 AngleXU=0 Radius=3 StartAngle=3.14159 EndAngle=4.71239
    g10: GeomPoint [constr] X=-6.15 Y=7.65 Z=0
  constraints (27):
    c: Coincident(g0,g1)
    c: Coincident(g1,g2)
    c: Coincident(g2,g3)
    c: Coincident(g3,g0)
    c: Vertical(g0)
    c: Vertical(g2)
    c: Horizontal(g1)
    c: Horizontal(g3)
    c: Tangent(g4,g8) = -1.5708
    c: Tangent(g4,g9) = -1.5708
    c: Tangent(g5,g9) = -1.5708
    c: Tangent(g7,g8) = -1.5708
    c: Vertical(g4)
    c: Horizontal(g5)
    c: Horizontal(g7)
    c: Equal(g8,g9)
    c: PointOnObject(g10,g4)
    c: PointOnObject(g10,g7)
    c: Radius(g9) = 3
    c: Coincident(g6,g7)
    c: Coincident(g5,g6)
    c: Symmetric(g6,g5,g-1)
    c: Symmetric(g2,g0,g-1)
    c: DistanceY(g0,g0) = 9.3
    c: DistanceX(g3,g3) = 6.3
    c: Coincident(g0,g8)
    c: DistanceX(g-1,g6) = 38.5
FEATURE [PartDesign::Pad] Pad029
  Direction = (0,0,1)
  Length = 5
  Length2 = 10
  Profile = -> Sketch063
  ReferenceAxis = -> Sketch063 [N_Axis]
  Suppressed = false
  Type = 0
FEATURE [Sketcher::SketchObject] Sketch064
  ArcFitTolerance = 1e-06
  AttachmentSupport = -> [Pad029]
  ExternalGeometry = -> [Pad029]
  FullyConstrained = true
  MakeInternals = false
  MapMode = 5
  Placement = pos=(38.5,0,0) rot=(0.57735,0.57735,0.57735;2.0944rad)
  sketch-geometry (8):
    g0: Circle CenterX=0 CenterY=16 CenterZ=0 NormalX=0 NormalY=0 NormalZ=1 AngleXU=0 Radius=2.75
    g1: LineSegment StartX=-7.65 StartY=19 StartZ=0 EndX=-7.65 EndY=5 EndZ=0
    g2: LineSegment StartX=7.65 StartY=5 StartZ=0 EndX=7.65 EndY=19 EndZ=0
    g3: LineSegment StartX=4.65 StartY=22 StartZ=0 EndX=-4.65 EndY=22 EndZ=0
    g4: ArcOfCircle CenterX=-4.65 CenterY=19 CenterZ=0 NormalX=0 NormalY=0 NormalZ=1 AngleXU=0 Radius=3 StartAngle=1.5708 EndAngle=3.14159
    g5: ArcOfCircle CenterX=4.65 CenterY=19 CenterZ=0 NormalX=0 NormalY=0 NormalZ=1 AngleXU=0 Radius=3 StartAngle=-9e-16 EndAngle=1.5708
    g6: GeomPoint [constr] X=-7.65 Y=22 Z=0
    g7: LineSegment StartX=-7.65 StartY=5 StartZ=0 EndX=7.65 EndY=5 EndZ=0
  constraints (19):
    c: Diameter(g0) = 5.5
    c: PointOnObject(g0,g-2)
    c: Tangent(g1,g4) = -1.5708
    c: Tangent(g2,g5) = -1.5708
    c: Tangent(g3,g5) = -1.5708
    c: Tangent(g3,g4) = -1.5708
    c: Vertical(g1)
    c: Vertical(g2)
    c: Horizontal(g3)
    c: PointOnObject(g6,g1)
    c: PointOnObject(g6,g3)
    c: Coincident(g1,g-3)
    c: Coincident(g2,g-3)
    c: Equal(g5,g4)
    c: Radius(g4) = 3
    c: DistanceY(g2,g0) = 11
    c: Coincident(g7,g1)
    c: Coincident(g7,g2)
    c: DistanceY(g0,g3) = 6
FEATURE [PartDesign::Pad] Pad030
  BaseFeature = -> Pad029
  Direction = (1,0,0)
  Length = 3
  Length2 = 10
  Profile = -> Sketch064
  ReferenceAxis = -> Sketch064 [N_Axis]
  Reversed = true
  Suppressed = false
  Type = 0
FEATURE [PartDesign::Chamfer] Chamfer  label="Chamfer001"
  Angle = 45
  Base = -> Pad030 [Edge19]
  BaseFeature = -> Pad030
  ChamferType = 1
  FlipDirection = false
  Size = 15
  Size2 = 5
  SupportTransform = false
  Suppressed = false
  UseAllEdges = false
FEATURE [PartDesign::Body] Body017  label="support_pince_planche_haut"
  AllowCompound = false
  Group = -> [Sketch063,Pad029,Sketch064,Pad030,Chamfer]
  Origin = -> Origin024
  Placement = pos=(3,-2.563e-05,214) rot=(0,0,1;0rad)
  Tip = -> Chamfer
FEATURE [Assembly::AssemblyObject] Assembly001
  Group = -> [Joints001,L16_50MM_SW_ASM,Part002002,Body013,Body017,Body089,Part002003]
  Origin = -> Origin015
  Type = Assembly
FEATURE [Part::Feature] Part__Feature  label="Profile_alu_20x20_33cm"
  Placement = pos=(150,-88,0) rot=(0,0,1;0rad)
  shape: bbox 20 x 20 x 330 mm, 71 faces (baked)
FEATURE [Part::Feature] Part__Feature008002002006403  label="Profile_alu_20x20_33cm001"
  Placement = pos=(-150,83,0) rot=(0,0,1;0rad)
  shape: bbox 20 x 20 x 330 mm, 71 faces (baked)
FEATURE [Part::Feature] Part__Feature008002002006404  label="Profile_alu_20x20_33cm002"
  Placement = pos=(150,83,0) rot=(0,0,1;0rad)
  shape: bbox 20 x 20 x 330 mm, 71 faces (baked)
FEATURE [Part::Feature] Part__Feature008002002006405  label="Profile_alu_20x20_33cm003"
  Placement = pos=(-150,-88,0) rot=(0,0,1;0rad)
  shape: bbox 20 x 20 x 330 mm, 71 faces (baked)
FEATURE [App::Part] Profile_alu_20x021
  Group = -> [Part__Feature,Part__Feature008002002006403,Part__Feature008002002006404,Part__Feature008002002006405]
  Origin = -> Origin295
FEATURE [App::Part] cache_profile_alu_2021  label="cache_profile_alu_2022"
  Origin = -> Origin296
  Placement = pos=(0,82.5,320) rot=(0,0,1;0rad)
FEATURE [Part::Feature] Part__Feature008002002006410  label="Profile_alu_20x20_265m001"
  Placement = pos=(220,-87.5,0) rot=(0,0,1;0rad)
  shape: bbox 20 x 20 x 260 mm, 71 faces (baked)
FEATURE [Part::Feature] Part__Feature008002002006411  label="Profile_alu_20x20_265m002"
  Placement = pos=(220,82.5,0) rot=(0,0,1;0rad)
  shape: bbox 20 x 20 x 260 mm, 71 faces (baked)
FEATURE [App::Part] Profile_alu_20x20_265m002  label="Profile_alu_20x20_265m003"
  Group = -> [Part__Feature008002002006410,Part__Feature008002002006411]
  Origin = -> Origin297
  Placement = pos=(2.01166e-07,0,2.38419e-07) rot=(0,-1,0;1.5708rad)
FEATURE [App::Part] Profile_alu
  Group = -> [Profile_alu_20x021,cache_profile_alu_2021,Profile_alu_20x20_265m002]
  Origin = -> Origin298
FEATURE [Part::Feature] Part__Feature008002002006414  label="Plaque_lateral_2025_g"
  Placement = pos=(-160,-2.5,330) rot=(0.57735,-0.57735,-0.57735;2.0944rad)
  shape: bbox 3 x 188 x 330 mm, 26 faces (baked)
FEATURE [Part::Feature] Part__Feature008002002006417  label="Plaque_carte_elec"
  Placement = pos=(0,0,230) rot=(0,0,1;0rad)
  shape: bbox 275 x 180 x 5 mm, 6 faces (baked)
FEATURE [App::Part] Plaques
  Group = -> [Part__Feature008002002006414,Part__Feature008002002006417]
  Origin = -> Origin299
FEATURE [Part::Feature] Part__Feature008002002006866  label="BlocInf_2"
  Placement = pos=(-12.4772,-12.7311,-67) rot=(0,0,1;0rad)
  shape: bbox 60 x 20 x 134 mm, 104 faces (baked)
FEATURE [Part::Feature] Part__Feature008002002006867  label="MotoReducteur_Faulhaber_2657_26.1_12V.23"
  Placement = pos=(-12.4772,7.26895,-1.47) rot=(0,1,0;1.5708rad)
  shape: bbox 26.1 x 26.1 x 119.5 mm, 47 faces (baked)
FEATURE [Part::Feature] Part__Feature008002002006868  label="MotoReducteur_Faulhaber_2657_26.1_12V.024"
  Placement = pos=(-12.4772,7.26895,1.47) rot=(0,-1,0;1.5708rad)
  shape: bbox 26.1 x 26.1 x 119.5 mm, 47 faces (baked)
FEATURE [Part::Feature] Part__Feature008002002006869  label="ClocheReducteur"
  Placement = pos=(-12.4772,7.26895,-107.7) rot=(0.57735,-0.57735,0.57735;2.0944rad)
  shape: bbox 52 x 40 x 40.7 mm, 46 faces (baked)
FEATURE [Part::Feature] Part__Feature008002002006870  label="ClocheReducteur001"
  Placement = pos=(-12.4772,7.26895,107.7) rot=(-0.57735,0.57735,0.57735;2.0944rad)
  shape: bbox 52 x 40 x 40.7 mm, 46 faces (baked)
FEATURE [Part::Feature] Part__Feature008002002006871  label="Jante_1.10"
  Placement = pos=(-12.4772,7.26895,-122) rot=(0,-1,0;1.5708rad)
  shape: bbox 51.2 x 51.2 x 32 mm, 31 faces (baked)
FEATURE [Part::Feature] Part__Feature008002002006872  label="Jante_1.011"
  Placement = pos=(-12.4772,7.26895,122) rot=(0,1,0;1.5708rad)
  shape: bbox 51.2 x 51.2 x 32 mm, 31 faces (baked)
FEATURE [Part::Feature] Part__Feature008002002006873  label="BlocSup_2"
  Placement = pos=(-12.4772,27.2689,-67) rot=(0,0,1;3.14159rad)
  shape: bbox 60 x 20.3 x 52 mm, 84 faces (baked)
FEATURE [Part::Feature] Part__Feature008002002006874  label="BlocSup_003"
  Placement = pos=(-12.4772,27.2689,67) rot=(1,0,0;3.14159rad)
  shape: bbox 60 x 20.3 x 52 mm, 84 faces (baked)
FEATURE [Part::Feature] Part__Feature008002002006875  label="Codeur_GI320"
  Placement = pos=(-12.5772,-3.23105,-123) rot=(-0.694747,0.186157,0.694747;2.77349rad)
  shape: bbox 24 x 24 x 31 mm, 28 faces (baked)
FEATURE [Part::Feature] Part__Feature008002002006876  label="Codeur_GI321"
  Placement = pos=(-12.3772,-3.23105,123) rot=(0.643476,0.414582,0.643476;3.92762rad)
  shape: bbox 24 x 24 x 31 mm, 28 faces (baked)
FEATURE [Part::Feature] Part__Feature008002002006877  label="RoueCodeuse"
  Placement = pos=(-12.3772,-3.23105,155) rot=(0.206869,0.956248,-0.206869;1.61552rad)
  shape: bbox 40.4 x 40.4 x 9 mm, 26 faces (baked)
FEATURE [Part::Feature] Part__Feature008002002006878  label="RoueCodeuse001"
  Placement = pos=(-12.5772,-3.23105,-155) rot=(-0.561833,-0.607196,-0.561833;2.05021rad)
  shape: bbox 40.4 x 40.4 x 9 mm, 26 faces (baked)
FEATURE [Part::Feature] Part__Feature008002002006879  label="suspension_codeur_01"
  Placement = pos=(-32.4772,31.2689,67) rot=(0.57735,0.57735,-0.57735;2.0944rad)
  shape: bbox 64 x 5 x 132 mm, 70 faces (baked)
FEATURE [Part::Feature] Part__Feature008002002006880  label="suspension_codeur_02"
  Placement = pos=(-0.377162,-18.2311,146) rot=(0,1,0;3.14159rad)
  shape: bbox 28 x 50 x 10 mm, 55 faces (baked)
FEATURE [Part::Feature] Part__Feature008002002006881  label="suspension_codeur_03"
  Placement = pos=(7.52284,-17.7311,67) rot=(0.57735,-0.57735,-0.57735;4.18879rad)
  shape: bbox 64 x 17 x 74 mm, 63 faces (baked)
FEATURE [Part::Feature] Part__Feature008002002006882  label="suspension_codeur_004"
  Placement = pos=(7.52284,31.2689,-67) rot=(0.57735,-0.57735,0.57735;2.0944rad)
  shape: bbox 64 x 5 x 132 mm, 70 faces (baked)
FEATURE [Part::Feature] Part__Feature008002002006883  label="suspension_codeur_005"
  Placement = pos=(-24.5772,-18.2311,-146) rot=(0,0,1;0rad)
  shape: bbox 28 x 50 x 10 mm, 55 faces (baked)
FEATURE [Part::Feature] Part__Feature008002002006884  label="suspension_codeur_006"
  Placement = pos=(-32.4772,-17.7311,-67) rot=(0.57735,0.57735,0.57735;4.18879rad)
  shape: bbox 64 x 17 x 74 mm, 63 faces (baked)
FEATURE [Part::Feature] Part__Feature008002002006885  label="Pneu_2025"
  Placement = pos=(-12.48,7.27,103) rot=(0,0,1;0rad)
  shape: bbox 69.27 x 69.27 x 26 mm, 16 faces (baked)
FEATURE [Part::Feature] Part__Feature008002002006886  label="Pneu_2026"
  Placement = pos=(-12.48,7.27,-103) rot=(0,0,1;0rad)
  shape: bbox 69.27 x 69.27 x 26 mm, 16 faces (baked)
FEATURE [App::Part] Bloc_moteur_2017
  Group = -> [Part__Feature008002002006866,Part__Feature008002002006867,Part__Feature008002002006868,Part__Feature008002002006869,Part__Feature008002002006870,Part__Feature008002002006871,Part__Feature008002002006872,Part__Feature008002002006873,Part__Feature008002002006874,Part__Feature008002002006875,Part__Feature008002002006876,Part__Feature008002002006877,Part__Feature008002002006878,+8 more]
  Origin = -> Origin334
  Placement = pos=(2.9e-15,11.3,12.7) rot=(0.57735,0.57735,0.57735;2.0944rad)
FEATURE [Part::Feature] Part__Feature008002002006887  label="Plaque_AV_chassis001"
  Placement = pos=(0,-55,0) rot=(0,0,1;0rad)
  shape: bbox 277.9 x 68.03 x 2 mm, 32 faces (baked)
FEATURE [Part::Feature] Part__Feature008002002006888  label="Plaque_AR_chassis"
  Placement = pos=(0,31,0) rot=(0,0,1;0rad)
  shape: bbox 244.5 x 75.93 x 2 mm, 62 faces (baked)
FEATURE [Part::Feature] Part__Feature008002002006889  label="Chassis_Grobot_ALU_2025"
  Placement = pos=(0,6,-5) rot=(0,0,1;0rad)
  shape: bbox 320 x 205 x 5 mm, 338 faces (baked)
FEATURE [App::Part] Base_roulante
  Group = -> [Bloc_moteur_2017,Part__Feature008002002006887,Part__Feature008002002006888,Part__Feature008002002006889]
  Origin = -> Origin335
  Placement = pos=(0,-5,0) rot=(0,0,1;3.14159rad)
FEATURE [App::Part] Structure
  Group = -> [Profile_alu,Plaques,Base_roulante]
  Origin = -> Origin336
FEATURE [Part::Feature] Part__Feature008002002006890  label="base"
  shape: bbox 58 x 28.4 x 30.48 mm, 43 faces (baked)
FEATURE [Part::Feature] Part__Feature008002002006891  label="avant"
  shape: bbox 58 x 15.3 x 26.82 mm, 133 faces (baked)
FEATURE [Part::Feature] Part__Feature008002002006892  label="arriere"
  shape: bbox 58 x 13.47 x 26.02 mm, 122 faces (baked)
FEATURE [Part::Feature] Part__Feature008002002006893  label="anneau"
  Placement = pos=(24,0,0) rot=(0,0,1;0rad)
  shape: bbox 5 x 21.32 x 21.32 mm, 5 faces (baked)
FEATURE [Part::Feature] Part__Feature008002002006894  label="anneau001"
  Placement = pos=(-24,7.62876e-07,0) rot=(0,0,1;3.14159rad)
  shape: bbox 5 x 21.32 x 21.32 mm, 5 faces (baked)
FEATURE [Part::Feature] Part__Feature008002002006895  label="PCB"
  shape: bbox 43 x 20 x 1.524 mm, 13 faces (baked)
FEATURE [Part::Feature] Part__Feature008002002006896  label="ultrason_module"
  Placement = pos=(-11.38,0,1.524) rot=(0,0,1;0rad)
  shape: bbox 17.6 x 17.6 x 12.7 mm, 4 faces (baked)
FEATURE [Part::Feature] Part__Feature008002002006897  label="diode"
  Placement = pos=(0,7.3,1.52) rot=(0,0,1;0rad)
  shape: bbox 5.7 x 5.25 x 5.7 mm, 7 faces (baked)
FEATURE [Part::Feature] Part__Feature008002002006898  label="ultrason_module001"
  Placement = pos=(11.38,0,1.52) rot=(0,0,1;0rad)
  shape: bbox 17.6 x 17.6 x 12.7 mm, 4 faces (baked)
FEATURE [App::Part] SRF08
  Group = -> [Part__Feature008002002006895,Part__Feature008002002006896,Part__Feature008002002006897,Part__Feature008002002006898]
  Origin = -> Origin337
  Placement = pos=(0,-2,0) rot=(0,0.707107,-0.707107;3.14159rad)
FEATURE [App::Part] partie_mobile
  Group = -> [Part__Feature008002002006891,Part__Feature008002002006892,Part__Feature008002002006893,Part__Feature008002002006894,SRF08]
  Origin = -> Origin338
FEATURE [App::Part] support_2_axes_SRF08
  Group = -> [Part__Feature008002002006890,partie_mobile]
  Origin = -> Origin339
  Placement = pos=(111,7.6294e-06,-0.000100851) rot=(0,0,1;0rad)
FEATURE [Part::Feature] Part__Feature008002002006899  label="base001"
  shape: bbox 58 x 28.4 x 30.48 mm, 43 faces (baked)
FEATURE [Part::Feature] Part__Feature008002002006900  label="avant001"
  shape: bbox 58 x 15.3 x 26.82 mm, 133 faces (baked)
FEATURE [Part::Feature] Part__Feature008002002006901  label="arriere001"
  shape: bbox 58 x 13.47 x 26.02 mm, 122 faces (baked)
FEATURE [Part::Feature] Part__Feature008002002006902  label="anneau002"
  Placement = pos=(24,0,0) rot=(0,0,1;0rad)
  shape: bbox 5 x 21.32 x 21.32 mm, 5 faces (baked)
FEATURE [Part::Feature] Part__Feature008002002006903  label="anneau003"
  Placement = pos=(-24,7.62876e-07,0) rot=(0,0,1;3.14159rad)
  shape: bbox 5 x 21.32 x 21.32 mm, 5 faces (baked)
FEATURE [Part::Feature] Part__Feature008002002006904  label="PCB001"
  shape: bbox 43 x 20 x 1.524 mm, 13 faces (baked)
FEATURE [Part::Feature] Part__Feature008002002006905  label="ultrason_module002"
  Placement = pos=(-11.38,0,1.524) rot=(0,0,1;0rad)
  shape: bbox 17.6 x 17.6 x 12.7 mm, 4 faces (baked)
FEATURE [Part::Feature] Part__Feature008002002006906  label="diode001"
  Placement = pos=(0,7.3,1.52) rot=(0,0,1;0rad)
  shape: bbox 5.7 x 5.25 x 5.7 mm, 7 faces (baked)
FEATURE [Part::Feature] Part__Feature008002002006907  label="ultrason_module003"
  Placement = pos=(11.38,0,1.52) rot=(0,0,1;0rad)
  shape: bbox 17.6 x 17.6 x 12.7 mm, 4 faces (baked)
FEATURE [App::Part] SRF009
  Group = -> [Part__Feature008002002006904,Part__Feature008002002006905,Part__Feature008002002006906,Part__Feature008002002006907]
  Origin = -> Origin340
  Placement = pos=(0,-2,0) rot=(0,0.707107,-0.707107;3.14159rad)
FEATURE [App::Part] partie_mobile001
  Group = -> [Part__Feature008002002006900,Part__Feature008002002006901,Part__Feature008002002006902,Part__Feature008002002006903,SRF009]
  Origin = -> Origin341
FEATURE [App::Part] support_2_axes_SRF009
  Group = -> [Part__Feature008002002006899,partie_mobile001]
  Origin = -> Origin342
  Placement = pos=(-111,-7.6294e-06,0.000100851) rot=(0,0,1;0rad)
FEATURE [App::Part] support_2_axes_SRF010
  Group = -> [support_2_axes_SRF08,support_2_axes_SRF009]
  Origin = -> Origin343
  Placement = pos=(1.492e-13,-0.5,0) rot=(0,0.707107,-0.707107;3.14159rad)
FEATURE [App::Part] Capteurs_US_AR
  Group = -> [support_2_axes_SRF010]
  Origin = -> Origin351
  Placement = pos=(0,-87.5,190) rot=(1,0,0;1.5708rad)
FEATURE [Part::Feature] Part__Feature008002002006920  label="base004"
  shape: bbox 58 x 28.4 x 30.48 mm, 43 faces (baked)
FEATURE [Part::Feature] Part__Feature008002002006921  label="avant004"
  shape: bbox 58 x 15.3 x 26.82 mm, 133 faces (baked)
FEATURE [Part::Feature] Part__Feature008002002006922  label="arriere004"
  shape: bbox 58 x 13.47 x 26.02 mm, 122 faces (baked)
FEATURE [Part::Feature] Part__Feature008002002006923  label="anneau008"
  Placement = pos=(24,0,0) rot=(0,0,1;0rad)
  shape: bbox 5 x 21.32 x 21.32 mm, 5 faces (baked)
FEATURE [Part::Feature] Part__Feature008002002006924  label="anneau009"
  Placement = pos=(-24,7.62876e-07,0) rot=(0,0,1;3.14159rad)
  shape: bbox 5 x 21.32 x 21.32 mm, 5 faces (baked)
FEATURE [Part::Feature] Part__Feature008002002006925  label="PCB002"
  shape: bbox 43 x 20 x 1.524 mm, 13 faces (baked)
FEATURE [Part::Feature] Part__Feature008002002006926  label="ultrason_module004"
  Placement = pos=(-11.38,0,1.524) rot=(0,0,1;0rad)
  shape: bbox 17.6 x 17.6 x 12.7 mm, 4 faces (baked)
FEATURE [Part::Feature] Part__Feature008002002006927  label="diode002"
  Placement = pos=(0,7.3,1.52) rot=(0,0,1;0rad)
  shape: bbox 5.7 x 5.25 x 5.7 mm, 7 faces (baked)
FEATURE [Part::Feature] Part__Feature008002002006928  label="ultrason_module005"
  Placement = pos=(11.38,0,1.52) rot=(0,0,1;0rad)
  shape: bbox 17.6 x 17.6 x 12.7 mm, 4 faces (baked)
FEATURE [App::Part] SRF010
  Group = -> [Part__Feature008002002006925,Part__Feature008002002006926,Part__Feature008002002006927,Part__Feature008002002006928]
  Origin = -> Origin352
  Placement = pos=(0,-2,0) rot=(0,0.707107,-0.707107;3.14159rad)
FEATURE [App::Part] partie_mobile004
  Group = -> [Part__Feature008002002006921,Part__Feature008002002006922,Part__Feature008002002006923,Part__Feature008002002006924,SRF010]
  Origin = -> Origin353
FEATURE [App::Part] support_2_axes_SRF011
  Group = -> [Part__Feature008002002006920,partie_mobile004]
  Origin = -> Origin354
  Placement = pos=(80,0,0) rot=(0,0,1;0.261799rad)
FEATURE [Part::Feature] Part__Feature008002002006929  label="base005"
  shape: bbox 58 x 28.4 x 30.48 mm, 43 faces (baked)
FEATURE [Part::Feature] Part__Feature008002002006930  label="avant005"
  shape: bbox 58 x 15.3 x 26.82 mm, 133 faces (baked)
FEATURE [Part::Feature] Part__Feature008002002006931  label="arriere005"
  shape: bbox 58 x 13.47 x 26.02 mm, 122 faces (baked)
FEATURE [Part::Feature] Part__Feature008002002006932  label="anneau010"
  Placement = pos=(24,0,0) rot=(0,0,1;0rad)
  shape: bbox 5 x 21.32 x 21.32 mm, 5 faces (baked)
FEATURE [Part::Feature] Part__Feature008002002006933  label="anneau011"
  Placement = pos=(-24,7.62876e-07,0) rot=(0,0,1;3.14159rad)
  shape: bbox 5 x 21.32 x 21.32 mm, 5 faces (baked)
FEATURE [Part::Feature] Part__Feature008002002006934  label="PCB003"
  shape: bbox 43 x 20 x 1.524 mm, 13 faces (baked)
FEATURE [Part::Feature] Part__Feature008002002006935  label="ultrason_module006"
  Placement = pos=(-11.38,0,1.524) rot=(0,0,1;0rad)
  shape: bbox 17.6 x 17.6 x 12.7 mm, 4 faces (baked)
FEATURE [Part::Feature] Part__Feature008002002006936  label="diode003"
  Placement = pos=(0,7.3,1.52) rot=(0,0,1;0rad)
  shape: bbox 5.7 x 5.25 x 5.7 mm, 7 faces (baked)
FEATURE [Part::Feature] Part__Feature008002002006937  label="ultrason_module007"
  Placement = pos=(11.38,0,1.52) rot=(0,0,1;0rad)
  shape: bbox 17.6 x 17.6 x 12.7 mm, 4 faces (baked)
FEATURE [App::Part] SRF011
  Group = -> [Part__Feature008002002006934,Part__Feature008002002006935,Part__Feature008002002006936,Part__Feature008002002006937]
  Origin = -> Origin355
  Placement = pos=(0,-2,0) rot=(0,0.707107,-0.707107;3.14159rad)
FEATURE [App::Part] partie_mobile005
  Group = -> [Part__Feature008002002006930,Part__Feature008002002006931,Part__Feature008002002006932,Part__Feature008002002006933,SRF011]
  Origin = -> Origin356
FEATURE [App::Part] support_2_axes_SRF012
  Group = -> [Part__Feature008002002006929,partie_mobile005]
  Origin = -> Origin357
  Placement = pos=(-80,0,0) rot=(0,0,-1;0.261799rad)
FEATURE [App::Part] support_2_axes_SRF013
  Group = -> [support_2_axes_SRF011,support_2_axes_SRF012]
  Origin = -> Origin358
  Placement = pos=(0,2.13e-14,0) rot=(1,0,0;3.14159rad)
FEATURE [App::Part] Capteurs_US_AV
  Group = -> [support_2_axes_SRF013]
  Origin = -> Origin359
  Placement = pos=(0,82.5,189.5) rot=(0,0,1;0rad)
FEATURE [App::Part] Capteurs_US_2024
  Group = -> [Capteurs_US_AR,Capteurs_US_AV]
  Origin = -> Origin360
FEATURE [App::Part] Capteurs
  Group = -> [Capteurs_US_2024]
  Origin = -> Origin361
FEATURE [App::Part] Robot_CRLG  label="Robot_CRLG_base"
  Group = -> [Structure,Capteurs]
  Origin = -> Origin362
FEATURE [Sketcher::SketchObject] Sketch269
  ArcFitTolerance = 1e-06
  AttachmentSupport = -> [XY_Plane]
  FullyConstrained = true
  MakeInternals = false
  MapMode = 5
  expr: Constraints[18] = 14 / 2
  sketch-geometry (12):
    g0: ArcOfCircle CenterX=0 CenterY=0 CenterZ=0 NormalX=0 NormalY=0 NormalZ=1 AngleXU=0 Radius=10 StartAngle=1.5708 EndAngle=4.71239
    g1: ArcOfCircle CenterX=85 CenterY=5e-16 CenterZ=0 NormalX=0 NormalY=0 NormalZ=1 AngleXU=0 Radius=10 StartAngle=4.71239 EndAngle=7.85398
    g2: LineSegment StartX=-1.6e-15 StartY=10 StartZ=0 EndX=85 EndY=10 EndZ=0
    g3: LineSegment StartX=-1.8e-15 StartY=-10 StartZ=0 EndX=85 EndY=-10 EndZ=0
    g4: Circle CenterX=85 CenterY=5e-16 CenterZ=0 NormalX=0 NormalY=0 NormalZ=1 AngleXU=0 Radius=4
    g5: Circle CenterX=0 CenterY=7 CenterZ=0 NormalX=0 NormalY=0 NormalZ=1 AngleXU=0 Radius=1.5
    g6: Circle CenterX=7 CenterY=0 CenterZ=0 NormalX=0 NormalY=0 NormalZ=1 AngleXU=0 Radius=1.5
    g7: Circle CenterX=-7 CenterY=0 CenterZ=0 NormalX=0 NormalY=0 NormalZ=1 AngleXU=0 Radius=1.5
    g8: Circle CenterX=0 CenterY=-7 CenterZ=0 NormalX=0 NormalY=0 NormalZ=1 AngleXU=0 Radius=1.5
    g9: LineSegment [constr] StartX=0 StartY=7 StartZ=0 EndX=0 EndY=0 EndZ=0
    g10: LineSegment [constr] StartX=0 StartY=0 StartZ=0 EndX=7 EndY=0 EndZ=0
    g11: Circle CenterX=0 CenterY=0 CenterZ=0 NormalX=0 NormalY=0 NormalZ=1 AngleXU=0 Radius=2
  constraints (28):
    c: Tangent(g0,g2) = 1.5708
    c: Tangent(g0,g3) = -1.5708
    c: Tangent(g1,g2) = 1.5708
    c: Tangent(g1,g3) = -1.5708
    c: Equal(g0,g1)
    c: Horizontal(g3)
    c: Coincident(g4,g1)
    c: Diameter(g1) = 20
    c: PointOnObject(g5,g-2)
    c: PointOnObject(g6,g-1)
    c: PointOnObject(g7,g-1)
    c: PointOnObject(g8,g-2)
    c: Symmetric(g6,g7,g0)
    c: Symmetric(g5,g8,g0)
    c: Equal(g5,g7)
    c: Equal(g7,g8)
    c: Equal(g8,g6)
    c: Diameter(g5) = 3  'd_vis'
    c: DistanceY(g0,g5) = 7
    c: Coincident(g9,g5)
    c: Coincident(g9,g0)
    c: Coincident(g10,g0)
    c: Coincident(g10,g6)
    c: Equal(g10,g9)
    c: DistanceX(g0,g1) = 85
    c: Diameter(g4) = 8
    c: Coincident(g11,g0)
    c: Diameter(g11) = 4
FEATURE [PartDesign::Pad] Pad
  Direction = (0,0,1)
  Length = 4
  Length2 = 10
  Profile = -> Sketch269
  ReferenceAxis = -> Sketch269 [N_Axis]
  Suppressed = false
  Type = 0
FEATURE [PartDesign::Body] Body  label="bras_1"
  AllowCompound = false
  Group = -> [Sketch269,Pad]
  Origin = -> Origin
  Tip = -> Pad
FEATURE [App::Link] servo_DS3218MG002  label="servo_DS3218MG004"
  LinkPlacement = pos=(-124.339,-55.425,32.4028) rot=(-0.702674,-1.9e-05,0.711512;3.1296rad)
  LinkedObject = -> Part007
  Placement = pos=(-124.339,-55.425,32.4028) rot=(-0.702674,-1.9e-05,0.711512;3.1296rad)
FEATURE [Sketcher::SketchObject] Sketch275
  ArcFitTolerance = 1e-06
  AttachmentSupport = -> [XY_Plane366]
  FullyConstrained = false
  MakeInternals = false
  MapMode = 5
  sketch-geometry (1):
    g0: Circle CenterX=0 CenterY=0 CenterZ=0 NormalX=0 NormalY=0 NormalZ=1 AngleXU=0 Radius=4.16676
  constraints (1):
    c: Coincident(g0,g-1)
FEATURE [PartDesign::Pad] Pad132
  Direction = (0,0,1)
  Length = 4
  Length2 = 10
  Profile = -> Sketch275
  ReferenceAxis = -> Sketch275 [N_Axis]
  Suppressed = false
  Type = 0
FEATURE [PartDesign::Body] Body096  label="Corps"
  AllowCompound = false
  Group = -> [Sketch275,Pad132]
  Origin = -> Origin369
  Tip = -> Pad132
FEATURE [Sketcher::SketchObject] Sketch276
  ArcFitTolerance = 1e-06
  AttachmentSupport = -> [XY_Plane367]
  FullyConstrained = false
  MakeInternals = false
  MapMode = 5
  sketch-geometry (6):
    g0: LineSegment StartX=-28.5 StartY=30 StartZ=0 EndX=-28.5 EndY=-30 EndZ=0
    g1: LineSegment StartX=-28.5 StartY=-30 StartZ=0 EndX=28.5 EndY=-30 EndZ=0
    g2: LineSegment StartX=28.5 StartY=-30 StartZ=0 EndX=28.5 EndY=30 EndZ=0
    g3: LineSegment StartX=28.5 StartY=30 StartZ=0 EndX=-28.5 EndY=30 EndZ=0
    g4: Circle CenterX=0 CenterY=5 CenterZ=0 NormalX=0 NormalY=0 NormalZ=1 AngleXU=0 Radius=3.31169
    g5: Circle CenterX=0 CenterY=-5 CenterZ=0 NormalX=0 NormalY=0 NormalZ=1 AngleXU=0 Radius=3.31169
  constraints (15):
    c: Coincident(g0,g1)
    c: Coincident(g1,g2)
    c: Coincident(g2,g3)
    c: Coincident(g3,g0)
    c: Vertical(g0)
    c: Vertical(g2)
    c: Horizontal(g1)
    c: Horizontal(g3)
    c: PointOnObject(g4,g-2)
    c: Symmetric(g2,g0,g-1)
    c: Symmetric(g4,g5,g-1)
    c: Equal(g4,g5)
    c: DistanceY(g0,g0) = 60
    c: DistanceX(g3,g3) = 57
    c: DistanceY(g5,g4) = 10
FEATURE [PartDesign::Pad] Pad133
  Direction = (0,0,1)
  Length = 30
  Length2 = 10
  Midplane = true
  Profile = -> Sketch276
  ReferenceAxis = -> Sketch276 [N_Axis]
  Suppressed = false
  Type = 0
FEATURE [PartDesign::Body] Body097  label="Corps004"
  AllowCompound = false
  Group = -> [Sketch276,Pad133]
  Origin = -> Origin370
  Tip = -> Pad133
FEATURE [App::Link] bras_1  label="bras_002"
  LinkPlacement = pos=(-129.138,-55.3847,32.463) rot=(0.521894,-0.66509,-0.534118;1.96234rad)
  LinkedObject = -> Body
  Placement = pos=(-129.138,-55.3847,32.463) rot=(0.521894,-0.66509,-0.534118;1.96234rad)
FEATURE [App::FeaturePython] Joint  label="Revolute"  # Assembly joint (typed FeaturePython)
  Activated = true
  AngleMax = 0
  AngleMin = 0
  Detach1 = false
  Detach2 = false
  Distance = 0
  Distance2 = 0
  EnableAngleMax = false
  EnableAngleMin = false
  EnableLengthMax = false
  EnableLengthMin = false
  JointType = 1 (Revolute)
  LengthMax = 0
  LengthMin = 0
  Placement2 = pos=(0,1e-15,4.4) rot=(1,0,0;3.14159rad)
  Reference1 = -> Assembly [bras_1.Edge3,bras_1.Edge3]
  Reference2 = -> Assembly [servo_DS3218MG002.Body014.Edge10,servo_DS3218MG002.Body014.Edge10]
FEATURE [Part::FeaturePython] InvoluteGear002  label="InvoluteGear_11_078"  # WARN: FeaturePython — macro-defined, semantics opaque (R4)
  AttacherType = Attacher::AttachEngine3D
  addendum_diameter = 26
  angular_backlash = 0
  axle_hole = false
  axle_holesize = 10
  backlash = 0
  clearance = 0.25
  double_helix = false
  head = 0
  head_fillet = 0
  height = 5.5
  helix_angle = 0
  module = 1
  num_teeth = 24
  numpoints = 20
  offset_hole = false
  offset_holeoffset = 10
  offset_holesize = 10
  pitch_diameter = 24
  pressure_angle = 20
  properties_from_tool = false
  reversed_backlash = false
  root_diameter = 21.5
  root_fillet = 0
  shift = 0
  simple = false
  transverse_pitch = 3.14159
  traverse_module = 1
  undercut = false
  version = 1.3.0
  expr: angular_backlash = backlash / pitch_diameter * 360 ° / pi
FEATURE [PartDesign::FeatureBase] BaseFeature005
  BaseFeature = -> InvoluteGear002
  Suppressed = false
FEATURE [Part::FeaturePython] InvoluteRack002  label="InvoluteRack_11_078"  # WARN: FeaturePython — macro-defined, semantics opaque (R4)
  AttacherType = Attacher::AttachEngine3D
  add_endings = true
  clearance = 0.25
  double_helix = false
  head = 0
  head_fillet = 0
  height = 3
  helix_angle = 0
  module = 1
  num_teeth = 30
  pressure_angle = 20
  properties_from_tool = false
  root_fillet = 0
  simplified = false
  thickness = 9.5
  transverse_pitch = 3.14159
  version = 1.3.0
FEATURE [PartDesign::FeatureBase] BaseFeature004
  BaseFeature = -> InvoluteRack002
  Suppressed = false
FEATURE [App::FeaturePython] Joint011  label="Fixe006"  # Assembly joint (typed FeaturePython)
  Activated = true
  AngleMax = 0
  AngleMin = 0
  Detach1 = false
  Detach2 = false
  Distance = 0
  Distance2 = 0
  EnableAngleMax = false
  EnableAngleMin = false
  EnableLengthMax = false
  EnableLengthMin = false
  JointType = 0 (Fixed)
  LengthMax = 0
  LengthMin = 0
  Placement1 = pos=(4,36,20) rot=(0,0,1;0rad)
  Placement2 = pos=(29,41,0) rot=(0,0,1;0rad)
  Reference1 = -> Assembly003 [Body101.Edge130,Body101.Edge130]
  Reference2 = -> Assembly003 [Body103.Edge42,Body103.Edge42]
FEATURE [App::FeaturePython] Joint012  label="Fixe007"  # Assembly joint (typed FeaturePython)
  Activated = true
  AngleMax = 0
  AngleMin = 0
  Detach1 = false
  Detach2 = false
  Distance = 0
  Distance2 = 0
  EnableAngleMax = false
  EnableAngleMin = false
  EnableLengthMax = false
  EnableLengthMin = false
  JointType = 0 (Fixed)
  LengthMax = 0
  LengthMin = 0
  Placement1 = pos=(3.5,16.75,0) rot=(0,0,1;0rad)
  Placement2 = pos=(3.5,16.75,8) rot=(0,0,1;0rad)
  Reference1 = -> Assembly003 [Body099.Edge25,Body099.Edge25]
  Reference2 = -> Assembly003 [Body103.Edge56,Body103.Edge56]
FEATURE [App::FeaturePython] Joint013  label="Fixe008"  # Assembly joint (typed FeaturePython)
  Activated = true
  AngleMax = 0
  AngleMin = 0
  Detach1 = false
  Detach2 = false
  Distance = 0
  Distance2 = 0
  EnableAngleMax = false
  EnableAngleMin = false
  EnableLengthMax = false
  EnableLengthMin = false
  JointType = 0 (Fixed)
  LengthMax = 0
  LengthMin = 0
  Placement1 = pos=(-34.5,13.9,6) rot=(0.57735,0.57735,0.57735;4.18879rad)
  Placement2 = pos=(31,54.5,2) rot=(0,0,1;0rad)
  Reference1 = -> Assembly003 [Part002006.Part__Feature008002002006940.Edge1102,Part002006.Part__Feature008002002006940.Edge1102]
  Reference2 = -> Assembly003 [Body101.Edge46,Body101.Edge46]
FEATURE [App::FeaturePython] Joint014  label="Glissière002"  # Assembly joint (typed FeaturePython)
  Activated = true
  AngleMax = 0
  AngleMin = 0
  Detach1 = false
  Detach2 = false
  Distance = 0
  Distance2 = 0
  EnableAngleMax = false
  EnableAngleMin = false
  EnableLengthMax = false
  EnableLengthMin = false
  JointType = 3 (Slider)
  LengthMax = 0
  LengthMin = 0
  Placement1 = pos=(0,2,4) rot=(0.707107,0,0.707107;3.14159rad)
  Placement2 = pos=(-10.75,48.0531,0) rot=(0.57735,0.57735,0.57735;4.18879rad)
  Reference1 = -> Assembly003 [Body103.Edge64,Body103.Vertex12]
  Reference2 = -> Assembly003 [Link006.Edge14,Link006.Edge14]
FEATURE [App::FeaturePython] Joint015  label="Pivot001"  # Assembly joint (typed FeaturePython)
  Activated = true
  AngleMax = 0
  AngleMin = -71
  Detach1 = false
  Detach2 = false
  Distance = 0
  Distance2 = 0
  EnableAngleMax = false
  EnableAngleMin = false
  EnableLengthMax = false
  EnableLengthMin = false
  JointType = 1 (Revolute)
  LengthMax = 0
  LengthMin = 0
  Placement1 = pos=(0,0,5.5) rot=(0,0,1;0rad)
  Placement2 = pos=(0,0,0.897999) rot=(0,0,1;0rad)
  Reference1 = -> Assembly003 [Body102.Edge300,Body102.Edge300]
  Reference2 = -> Assembly003 [Part002006.Screw006.Edge22,Part002006.Screw006.Edge22]
FEATURE [App::FeaturePython] Joint016  label="Glissière003"  # Assembly joint (typed FeaturePython)
  Activated = true
  AngleMax = 0
  AngleMin = 0
  Detach1 = false
  Detach2 = false
  Distance = 0
  Distance2 = 0
  EnableAngleMax = false
  EnableAngleMin = false
  EnableLengthMax = false
  EnableLengthMin = false
  JointType = 3 (Slider)
  LengthMax = 0
  LengthMin = 0
  Placement1 = pos=(-10.75,48.0531,0) rot=(0.57735,0.57735,0.57735;4.18879rad)
  Placement2 = pos=(50,48,4) rot=(0.707107,0,0.707107;3.14159rad)
  Reference1 = -> Assembly003 [Body100.Edge14,Body100.Edge14]
  Reference2 = -> Assembly003 [Body103.Edge46,Body103.Edge46]
FEATURE [App::FeaturePython] Joint017  label="Fixe009"  # Assembly joint (typed FeaturePython)
  Activated = true
  AngleMax = 0
  AngleMin = 0
  Detach1 = false
  Detach2 = false
  Distance = 0
  Distance2 = 0
  EnableAngleMax = false
  EnableAngleMin = false
  EnableLengthMax = false
  EnableLengthMin = false
  JointType = 0 (Fixed)
  LengthMax = 0
  LengthMin = 0
  Offset2 = pos=(0,0,0) rot=(0,0,1;1.5708rad)
  Placement1 = pos=(9.25,92.677,40) rot=(0.707107,0,0.707107;3.14159rad)
  Placement2 = pos=(4.5,0,3) rot=(-1,0,0;4.71239rad)
  Reference1 = -> Assembly003 [Body100.Edge263,Body100.Edge263]
  Reference2 = -> Assembly003 [Body104.Edge5,Body104.Edge5]
FEATURE [App::FeaturePython] Joint018  label="Fixe010"  # Assembly joint (typed FeaturePython)
  Activated = true
  AngleMax = 0
  AngleMin = 0
  Detach1 = false
  Detach2 = false
  Distance = 0
  Distance2 = 0
  EnableAngleMax = false
  EnableAngleMin = false
  EnableLengthMax = false
  EnableLengthMin = false
  JointType = 0 (Fixed)
  LengthMax = 0
  LengthMin = 0
  Offset2 = pos=(0,0,0) rot=(0,0,1;1.5708rad)
  Placement1 = pos=(4.5,0,3) rot=(-0.57735,-0.57735,0.57735;4.18879rad)
  Placement2 = pos=(9.25,92.677,40) rot=(0.57735,-0.57735,0.57735;4.18879rad)
  Reference1 = -> Assembly003 [Link007.Edge5,Link007.Edge5]
  Reference2 = -> Assembly003 [Link006.Edge263,Link006.Edge263]
FEATURE [App::FeaturePython] Joint019  label="Crémaillère002"  # Assembly joint (typed FeaturePython)
  Activated = true
  AngleMax = 0
  AngleMin = 0
  Detach1 = false
  Detach2 = false
  Distance = 11.77
  Distance2 = 0
  EnableAngleMax = false
  EnableAngleMin = false
  EnableLengthMax = false
  EnableLengthMin = false
  JointType = 9 (RackPinion)
  LengthMax = 0
  LengthMin = 0
  Placement1 = pos=(-10.75,33.0531,3) rot=(0.57735,0.57735,0.57735;4.18879rad)
  Reference1 = -> Assembly003 [Body100.Edge8,Body100.Edge8]
  Reference2 = -> Assembly003 [Body102.Edge154,Body102.Edge154]
FEATURE [App::FeaturePython] Joint020  label="Crémaillère003"  # Assembly joint (typed FeaturePython)
  Activated = true
  AngleMax = 0
  AngleMin = 0
  Detach1 = false
  Detach2 = false
  Distance = 11.77
  Distance2 = 0
  EnableAngleMax = false
  EnableAngleMin = false
  EnableLengthMax = false
  EnableLengthMin = false
  JointType = 9 (RackPinion)
  LengthMax = 0
  LengthMin = 0
  Placement1 = pos=(-10.75,33.0531,3) rot=(0.57735,0.57735,0.57735;4.18879rad)
  Reference1 = -> Assembly003 [Link006.Edge8,Link006.Edge8]
  Reference2 = -> Assembly003 [Body102.Edge154,Body102.Edge154]
FEATURE [App::Link] Link006  label="pince_cremaillere_bras005"
  LinkPlacement = pos=(67.1598,7.75,24) rot=(0,0,1;1.5708rad)
  LinkedObject = -> Body100
  Placement = pos=(67.1598,7.75,24) rot=(0,0,1;1.5708rad)
FEATURE [App::Link] Link007  label="mousse005"
  LinkPlacement = pos=(-22.5171,17,59.5) rot=(0,-1,0;1.5708rad)
  LinkedObject = -> Body104
  Placement = pos=(-22.5171,17,59.5) rot=(0,-1,0;1.5708rad)
FEATURE [Part::Feature] Part__Feature008002002006938  label="Lever 25T003"
  Placement = pos=(0,0,0) rot=(-1,0,0;1.5708rad)
  shape: bbox 18.84 x 33.03 x 6.019 mm, 125 faces (baked)
FEATURE [Part::Feature] Part__Feature008002002006939  label="Axis Servo003"
  Placement = pos=(0,0,0) rot=(-1,0,0;1.5708rad)
  shape: bbox 5 x 5 x 8 mm, 5 faces (baked)
FEATURE [Part::Feature] Part__Feature008002002006940  label="Servo DS3218MG003"
  Placement = pos=(0,0,0) rot=(-1,0,0;1.5708rad)
  shape: bbox 55 x 20 x 41 mm, 772 faces (baked)
FEATURE [Part::FeaturePython] Screw006  label="M2x5-Vis002"  # WARN: FeaturePython — macro-defined, semantics opaque (R4)
  BaseObject = -> Body098 [Edge6]
  Diameter = 2
  Invert = true
  LeftHanded = false
  Length = 10
  LengthCustom = 5
  MatchOuter = false
  OffsetAngle = 0
  Placement = pos=(0,1e-15,4.8) rot=(0,0,1;0rad)
  Thread = false
  Type = 76
FEATURE [Sketcher::SketchObject] Sketch279
  ArcFitTolerance = 0
  AttachmentSupport = -> [XY_Plane369]
  FullyConstrained = true
  MakeInternals = false
  MapMode = 2
  sketch-geometry (31):
    g0: LineSegment StartX=0 StartY=50 StartZ=0 EndX=100 EndY=50 EndZ=0
    g1: LineSegment StartX=100 StartY=50 StartZ=0 EndX=100 EndY=48 EndZ=0
    g2: LineSegment StartX=100 StartY=0 StartZ=0 EndX=0 EndY=0 EndZ=0
    g3: LineSegment StartX=0 StartY=0 StartZ=0 EndX=0 EndY=2 EndZ=0
    g4: Circle CenterX=50 CenterY=25 CenterZ=0 NormalX=0 NormalY=0 NormalZ=1 AngleXU=0 Radius=14
    g5: LineSegment [constr] StartX=0 StartY=50 StartZ=0 EndX=100 EndY=0 EndZ=0
    g6: LineSegment [constr] StartX=0 StartY=0 StartZ=0 EndX=100 EndY=50 EndZ=0
    g7: LineSegment [constr] StartX=0 StartY=25 StartZ=0 EndX=100 EndY=25 EndZ=0
    g8: LineSegment [constr] StartX=50 StartY=50 StartZ=0 EndX=50 EndY=0 EndZ=0
    g9: LineSegment [constr] StartX=3.5 StartY=33.25 StartZ=0 EndX=96.5 EndY=33.25 EndZ=0
    g10: LineSegment [constr] StartX=96.5 StartY=33.25 StartZ=0 EndX=96.5 EndY=16.75 EndZ=0
    g11: LineSegment [constr] StartX=96.5 StartY=16.75 StartZ=0 EndX=3.5 EndY=16.75 EndZ=0
    g12: LineSegment [constr] StartX=3.5 StartY=16.75 StartZ=0 EndX=3.5 EndY=33.25 EndZ=0
    g13: Circle CenterX=96.5 CenterY=33.25 CenterZ=0 NormalX=0 NormalY=0 NormalZ=1 AngleXU=0 Radius=1.65
    g14: Circle CenterX=3.5 CenterY=33.25 CenterZ=0 NormalX=0 NormalY=0 NormalZ=1 AngleXU=0 Radius=1.65
    g15: Circle CenterX=3.5 CenterY=16.75 CenterZ=0 NormalX=0 NormalY=0 NormalZ=1 AngleXU=0 Radius=1.65
    g16: Circle CenterX=96.5 CenterY=16.75 CenterZ=0 NormalX=0 NormalY=0 NormalZ=1 AngleXU=0 Radius=1.65
    g17: LineSegment StartX=0 StartY=2 StartZ=0 EndX=30 EndY=2 EndZ=0
    g18: LineSegment StartX=30 StartY=2 StartZ=0 EndX=30 EndY=7.5 EndZ=0
    g19: LineSegment StartX=30 StartY=7.5 StartZ=0 EndX=2.5 EndY=7.5 EndZ=0
    g20: LineSegment StartX=0 StartY=10 StartZ=0 EndX=0 EndY=50 EndZ=0
    g21: LineSegment StartX=100 StartY=48 StartZ=0 EndX=67.5 EndY=48 EndZ=0
    g22: LineSegment StartX=67.5 StartY=48 StartZ=0 EndX=67.5 EndY=42.5 EndZ=0
    g23: LineSegment StartX=67.5 StartY=42.5 StartZ=0 EndX=97.5 EndY=42.5 EndZ=0
    g24: LineSegment StartX=100 StartY=40 StartZ=0 EndX=100 EndY=0 EndZ=0
    g25: ArcOfCircle [constr] CenterX=97.5 CenterY=40 CenterZ=0 NormalX=0 NormalY=0 NormalZ=1 AngleXU=0 Radius=2.5 StartAngle=0 EndAngle=1.5708
    g26: GeomPoint [constr] X=100 Y=42.5 Z=0
    g27: LineSegment StartX=100 StartY=40 StartZ=0 EndX=97.5 EndY=42.5 EndZ=0
    g28: ArcOfCircle [constr] CenterX=2.5 CenterY=10 CenterZ=0 NormalX=0 NormalY=0 NormalZ=1 AngleXU=0 Radius=2.5 StartAngle=3.14159 EndAngle=4.71239
    g29: GeomPoint [constr] X=0 Y=7.5 Z=0
    g30: LineSegment StartX=0 StartY=10 StartZ=0 EndX=2.5 EndY=7.5 EndZ=0
  constraints (78):
    c: Coincident(g0,g1)
    c: Coincident(g24,g2)
    c: Coincident(g2,g3)
    c: Coincident(g20,g0)
    c: Horizontal(g0)
    c: Horizontal(g2)
    c: Vertical(g1)
    c: Vertical(g3)
    c: Coincident(g2,g-1)
    c: Coincident(g5,g0)
    c: Coincident(g2,g6)
    c: Coincident(g0,g6)
    c: Coincident(g24,g5)
    c: PointOnObject(g4,g6)
    c: PointOnObject(g4,g5)
    c: Diameter(g4) = 28
    c: DistanceY(g3,g20) = 50
    c: DistanceX(g2,g2) = 100
    c: PointOnObject(g8,g0)
    c: PointOnObject(g7,g24)
    c: PointOnObject(g7,g20)
    c: PointOnObject(g8,g2)
    c: Symmetric(g0,g0,g8)
    c: Symmetric(g0,g2,g7)
    c: Coincident(g9,g10)
    c: Coincident(g10,g11)
    c: Coincident(g11,g12)
    c: Coincident(g12,g9)
    c: Horizontal(g11)
    c: Vertical(g12)
    c: Symmetric(g9,g10,g7)
    c: Symmetric(g9,g9,g8)
    c: Distance(g12) = 16.5
    c: DistanceX(g0,g9) = 3.5
    c: Coincident(g16,g10)
    c: Coincident(g13,g9)
    c: Coincident(g9,g14)
    c: Coincident(g11,g15)
    c: Equal(g14,g15)
    c: Equal(g14,g13)
    c: Equal(g14,g16)
    c: Diameter(g14) = 3.3
    c: Coincident(g17,g18)
    c: Coincident(g18,g19)
    c: Horizontal(g17)
    c: Horizontal(g19)
    c: Vertical(g18)
    c: Vertical(g20)
    c: DistanceX(g29,g19) = 30
    c: Coincident(g21,g22)
    c: Coincident(g22,g23)
    c: Horizontal(g21)
    c: Horizontal(g23)
    c: Vertical(g22)
    c: Vertical(g24)
    c: Equal(g18,g22)
    c: PointOnObject(g26,g23)
    c: PointOnObject(g26,g24)
    c: Tangent(g23,g25) = 1.5708
    c: Tangent(g24,g25) = 1.5708
    c: Coincident(g27,g23)
    c: Coincident(g27,g24)
    c: PointOnObject(g29,g20)
    c: PointOnObject(g29,g19)
    c: Tangent(g20,g28) = 1.5708
    c: Tangent(g19,g28) = 1.5708
    c: Coincident(g30,g20)
    c: Coincident(g30,g19)
    c: Equal(g1,g3)
    c: Equal(g23,g17)
    c: Coincident(g3,g17)
    c: DistanceY(g3,g3) = 2
    c: Coincident(g1,g21)
    c: Vertical(g1,g24)
    c: Vertical(g29,g3)
    c: DistanceY(g18,g18) = 5.5
    c: Radius(g28) = 2.5
    c: Equal(g25,g28)
FEATURE [PartDesign::Pad] Pad135
  AlongSketchNormal = false
  Direction = (0,0,1)
  Length = 4
  Length2 = 100
  Profile = -> Sketch279
  ReferenceAxis = -> Sketch279 [N_Axis]
  Suppressed = false
  Type = 0
FEATURE [Sketcher::SketchObject] Sketch280
  ArcFitTolerance = 1e-06
  AttachmentOffset = pos=(0,0,4) rot=(0,0,1;0rad)
  AttachmentSupport = -> [XY_Plane369]
  ExternalGeometry = -> [Pad135]
  FullyConstrained = true
  MakeInternals = false
  MapMode = 5
  Placement = pos=(0,0,4) rot=(0,0,1;0rad)
  sketch-geometry (4):
    g0: Circle CenterX=3.5 CenterY=33.25 CenterZ=0 NormalX=0 NormalY=0 NormalZ=1 AngleXU=0 Radius=3.25
    g1: Circle CenterX=3.5 CenterY=16.75 CenterZ=0 NormalX=0 NormalY=0 NormalZ=1 AngleXU=0 Radius=3.25
    g2: Circle CenterX=96.5 CenterY=33.25 CenterZ=0 NormalX=0 NormalY=0 NormalZ=1 AngleXU=0 Radius=3.25
    g3: Circle CenterX=96.5 CenterY=16.75 CenterZ=0 NormalX=0 NormalY=0 NormalZ=1 AngleXU=0 Radius=3.25
  constraints (10):
    c: Coincident(g0,g-3)
    c: Coincident(g1,g-4)
    c: Equal(g0,g1)
    c: Equal(g1,g2)
    c: Equal(g2,g3)
    c: Diameter(g0) = 6.5
    c: Horizontal(g3,g1)
    c: Horizontal(g2,g0)
    c: Vertical(g2,g3)
    c: DistanceX(g1,g3) = 93
FEATURE [PartDesign::Pocket] Pocket117
  BaseFeature = -> Pad135
  Direction = (0,0,-1)
  Length = 2
  Length2 = 5
  Profile = -> Sketch280
  ReferenceAxis = -> Sketch280 [N_Axis]
  Refine = true
  Suppressed = false
  Type = 0
FEATURE [PartDesign::Body] Body099  label="pince_capot002"
  AllowCompound = false
  Group = -> [Sketch279,Pad135,Sketch280,Pocket117]
  Origin = -> Origin372
  Placement = pos=(-25,-5,28) rot=(0,0,1;0rad)
  Tip = -> Pocket117
FEATURE [Sketcher::SketchObject] Sketch281
  ArcFitTolerance = 1e-06
  AttachmentSupport = -> [BaseFeature004]
  FullyConstrained = true
  MakeInternals = false
  MapMode = 5
  Placement = pos=(0,92.677,0) rot=(0,0.707107,0.707107;3.14159rad)
  sketch-geometry (4):
    g0: LineSegment StartX=-29.25 StartY=0 StartZ=0 EndX=10.75 EndY=0 EndZ=0
    g1: LineSegment StartX=10.75 StartY=0 StartZ=0 EndX=10.75 EndY=40 EndZ=0
    g2: LineSegment StartX=10.75 StartY=40 StartZ=0 EndX=-29.25 EndY=40 EndZ=0
    g3: LineSegment StartX=-29.25 StartY=40 StartZ=0 EndX=-29.25 EndY=0 EndZ=0
  constraints (12):
    c: Coincident(g0,g1)
    c: Coincident(g1,g2)
    c: Coincident(g2,g3)
    c: Coincident(g3,g0)
    c: Horizontal(g0)
    c: Horizontal(g2)
    c: Vertical(g1)
    c: Vertical(g3)
    c: DistanceY(g3,g3) = 40
    c: DistanceX(g2,g2) = 40
    c: PointOnObject(g0,g-1)
    c: DistanceX(g-1,g0) = 10.75
FEATURE [PartDesign::Pad] Pad136
  BaseFeature = -> BaseFeature004
  Direction = (0,1,-2e-16)
  Length = 5
  Length2 = 10
  Profile = -> Sketch281
  ReferenceAxis = -> Sketch281 [N_Axis]
  Refine = true
  Suppressed = false
  Type = 0
FEATURE [Sketcher::SketchObject] Sketch282
  ArcFitTolerance = 0
  AttachmentOffset = pos=(0,0,-2) rot=(0,0,1;0rad)
  AttachmentSupport = -> [XY_Plane371]
  FullyConstrained = true
  MakeInternals = false
  MapMode = 2
  Placement = pos=(0,0,-2) rot=(0,0,1;0rad)
  sketch-geometry (18):
    g0: LineSegment StartX=14.5 StartY=50 StartZ=0 EndX=35.5 EndY=50 EndZ=0
    g1: LineSegment StartX=35.5 StartY=50 StartZ=0 EndX=35.5 EndY=9 EndZ=0
    g2: LineSegment StartX=35.5 StartY=9 StartZ=0 EndX=14.5 EndY=9 EndZ=0
    g3: LineSegment StartX=14.5 StartY=9 StartZ=0 EndX=14.5 EndY=50 EndZ=0
    g4: LineSegment StartX=0 StartY=59 StartZ=0 EndX=50 EndY=59 EndZ=0
    g5: LineSegment StartX=50 StartY=59 StartZ=0 EndX=50 EndY=0 EndZ=0
    g6: LineSegment StartX=50 StartY=0 StartZ=0 EndX=0 EndY=0 EndZ=0
    g7: LineSegment StartX=0 StartY=0 StartZ=0 EndX=0 EndY=59 EndZ=0
    g8: Circle CenterX=19 CenterY=54.5 CenterZ=0 NormalX=0 NormalY=0 NormalZ=1 AngleXU=0 Radius=1.65
    g9: Circle CenterX=31 CenterY=54.5 CenterZ=0 NormalX=0 NormalY=0 NormalZ=1 AngleXU=0 Radius=1.65
    g10: Circle CenterX=19 CenterY=4.5 CenterZ=0 NormalX=0 NormalY=0 NormalZ=1 AngleXU=0 Radius=1.65
    g11: Circle CenterX=31 CenterY=4.5 CenterZ=0 NormalX=0 NormalY=0 NormalZ=1 AngleXU=0 Radius=1.65
    g12: LineSegment [constr] StartX=19 StartY=54.5 StartZ=0 EndX=31 EndY=54.5 EndZ=0
    g13: LineSegment [constr] StartX=31 StartY=54.5 StartZ=0 EndX=31 EndY=4.5 EndZ=0
    g14: LineSegment [constr] StartX=31 StartY=4.5 StartZ=0 EndX=19 EndY=4.5 EndZ=0
    g15: LineSegment [constr] StartX=19 StartY=4.5 StartZ=0 EndX=19 EndY=54.5 EndZ=0
    g16: LineSegment [constr] StartX=14.5 StartY=29.5 StartZ=0 EndX=35.5 EndY=29.5 EndZ=0
    g17: LineSegment [constr] StartX=25 StartY=50 StartZ=0 EndX=25 EndY=9 EndZ=0
  constraints (46):
    c: Coincident(g0,g1)
    c: Coincident(g1,g2)
    c: Coincident(g2,g3)
    c: Coincident(g3,g0)
    c: Horizontal(g0)
    c: Horizontal(g2)
    c: Vertical(g1)
    c: Vertical(g3)
    c: Coincident(g4,g5)
    c: Coincident(g5,g6)
    c: Coincident(g6,g7)
    c: Coincident(g7,g4)
    c: Horizontal(g6)
    c: Vertical(g5)
    c: Coincident(g12,g13)
    c: Coincident(g13,g14)
    c: Coincident(g14,g15)
    c: Coincident(g15,g12)
    c: Horizontal(g14)
    c: Vertical(g15)
    c: Coincident(g10,g14)
    c: Coincident(g11,g13)
    c: Coincident(g8,g12)
    c: Coincident(g9,g12)
    c: PointOnObject(g17,g0)
    c: PointOnObject(g17,g2)
    c: PointOnObject(g16,g3)
    c: PointOnObject(g16,g1)
    c: Symmetric(g0,g0,g17)
    c: Symmetric(g2,g0,g16)
    c: Symmetric(g9,g8,g17)
    c: DistanceX(g2,g2) = 21
    c: DistanceY(g3,g3) = 41
    c: DistanceX(g14,g14) = 12
    c: DistanceY(g13,g13) = 50
    c: Equal(g9,g8)
    c: Equal(g9,g11)
    c: Equal(g9,g10)
    c: Diameter(g9) = 3.3
    c: Symmetric(g9,g11,g16)
    c: Coincident(g-1,g6)
    c: Symmetric(g4,g4,g17)
    c: DistanceX(g6,g2) = 14.5
    c: Vertical(g7)
    c: DistanceY(g5,g5) = 59
    c: DistanceY(g-1,g2) = 9
FEATURE [PartDesign::Pad] Pad137
  AlongSketchNormal = false
  Direction = (0,0,1)
  Length = 4
  Length2 = 100
  Profile = -> Sketch282
  ReferenceAxis = -> Sketch282 [N_Axis]
  Suppressed = false
  Type = 0
FEATURE [Sketcher::SketchObject] Sketch283
  ArcFitTolerance = 0
  AttachmentSupport = -> [Pad137]
  ExternalGeometry = -> [Pad137]
  FullyConstrained = true
  MakeInternals = false
  MapMode = 5
  Placement = pos=(0,0,2) rot=(0,0,1;0rad)
  sketch-geometry (10):
    g0: LineSegment StartX=0 StartY=40 StartZ=0 EndX=8 EndY=40 EndZ=0
    g1: LineSegment StartX=8 StartY=40 StartZ=0 EndX=8 EndY=0 EndZ=0
    g2: LineSegment StartX=8 StartY=0 StartZ=0 EndX=0 EndY=0 EndZ=0
    g3: LineSegment StartX=0 StartY=0 StartZ=0 EndX=0 EndY=40 EndZ=0
    g4: LineSegment StartX=42 StartY=40 StartZ=0 EndX=50 EndY=40 EndZ=0
    g5: LineSegment StartX=50 StartY=40 StartZ=0 EndX=50 EndY=0 EndZ=0
    g6: LineSegment StartX=50 StartY=0 StartZ=0 EndX=42 EndY=0 EndZ=0
    g7: LineSegment StartX=42 StartY=0 StartZ=0 EndX=42 EndY=40 EndZ=0
    g8: LineSegment [constr] StartX=25 StartY=59 StartZ=0 EndX=25 EndY=0 EndZ=0
    g9: LineSegment [constr] StartX=0 StartY=20 StartZ=0 EndX=50 EndY=20 EndZ=0
  constraints (28):
    c: Coincident(g0,g1)
    c: Coincident(g1,g2)
    c: Coincident(g2,g3)
    c: Coincident(g3,g0)
    c: Horizontal(g0)
    c: Horizontal(g2)
    c: Vertical(g3)
    c: Coincident(g4,g5)
    c: Coincident(g5,g6)
    c: Coincident(g6,g7)
    c: Coincident(g7,g4)
    c: Horizontal(g4)
    c: Horizontal(g6)
    c: Vertical(g5)
    c: PointOnObject(g4,g-4)
    c: PointOnObject(g8,g-5)
    c: PointOnObject(g8,g-6)
    c: Symmetric(g-5,g-5,g8)
    c: Symmetric(g0,g4,g8)
    c: DistanceX(g0,g0) = 8
    c: Vertical(g1)
    c: PointOnObject(g9,g3)
    c: PointOnObject(g9,g5)
    c: Symmetric(g0,g1,g9)
    c: Vertical(g7)
    c: PointOnObject(g5,g-1)
    c: DistanceY(g3,g3) = 40
    c: Coincident(g2,g-1)
FEATURE [PartDesign::Pad] Pad138
  AlongSketchNormal = false
  BaseFeature = -> Pad137
  Direction = (0,0,1)
  Length = 18
  Length2 = 100
  Profile = -> Sketch283
  Suppressed = false
  Type = 0
FEATURE [Sketcher::SketchObject] Sketch284
  ArcFitTolerance = 0
  AttachmentSupport = -> [Pad138]
  ExternalGeometry = -> [Pad138]
  FullyConstrained = true
  MakeInternals = false
  MapMode = 5
  Placement = pos=(0,0,20) rot=(0,0,1;0rad)
  sketch-geometry (7):
    g0: LineSegment [constr] StartX=25 StartY=40 StartZ=0 EndX=25 EndY=0 EndZ=0
    g1: LineSegment [constr] StartX=0 StartY=20 StartZ=0 EndX=50 EndY=20 EndZ=0
    g2: Circle CenterX=4 CenterY=36 CenterZ=0 NormalX=0 NormalY=0 NormalZ=1 AngleXU=0 Radius=1.75
    g3: Circle CenterX=46 CenterY=36 CenterZ=0 NormalX=0 NormalY=0 NormalZ=1 AngleXU=0 Radius=1.75
    g4: Circle CenterX=4 CenterY=4 CenterZ=0 NormalX=0 NormalY=0 NormalZ=1 AngleXU=0 Radius=1.75
    g5: Circle CenterX=46 CenterY=4 CenterZ=0 NormalX=0 NormalY=0 NormalZ=1 AngleXU=0 Radius=1.75
    g6: LineSegment [constr] StartX=4 StartY=36 StartZ=0 EndX=4 EndY=4 EndZ=0
  constraints (17):
    c: PointOnObject(g0,g-4)
    c: PointOnObject(g0,g-5)
    c: PointOnObject(g1,g-7)
    c: PointOnObject(g1,g-8)
    c: Symmetric(g-3,g-4,g0)
    c: Symmetric(g-5,g-4,g1)
    c: Symmetric(g4,g2,g1)
    c: Symmetric(g3,g2,g0)
    c: Symmetric(g5,g3,g1)
    c: Equal(g2,g4)
    c: Equal(g2,g3)
    c: Equal(g2,g5)
    c: Radius(g2) = 1.75
    c: Coincident(g6,g4)
    c: Coincident(g6,g2)
    c: Symmetric(g-7,g-5,g6)
    c: DistanceY(g-5,g4) = 4
FEATURE [PartDesign::Pocket] Pocket118
  BaseFeature = -> Pad138
  Direction = (0,0,-1)
  Length = 5
  Length2 = 100
  Profile = -> Sketch284
  Suppressed = false
  Type = 1
FEATURE [Sketcher::SketchObject] Sketch285
  ArcFitTolerance = 0
  AttachmentSupport = -> [Pocket118]
  ExternalGeometry = -> [Pocket118]
  FullyConstrained = true
  MakeInternals = false
  MapMode = 5
  Placement = pos=(50,0,0) rot=(0.57735,0.57735,0.57735;2.0944rad)
  sketch-geometry (7):
    g0: LineSegment [constr] StartX=0 StartY=20 StartZ=0 EndX=40 EndY=0 EndZ=0
    g1: LineSegment [constr] StartX=0 StartY=0 StartZ=0 EndX=40 EndY=20 EndZ=0
    g2: Circle CenterX=12 CenterY=17 CenterZ=0 NormalX=0 NormalY=0 NormalZ=1 AngleXU=0 Radius=1.75
    g3: Circle CenterX=12 CenterY=3 CenterZ=0 NormalX=0 NormalY=0 NormalZ=1 AngleXU=0 Radius=1.75
    g4: Circle CenterX=28 CenterY=3 CenterZ=0 NormalX=0 NormalY=0 NormalZ=1 AngleXU=0 Radius=1.75
    g5: Circle CenterX=28 CenterY=17 CenterZ=0 NormalX=0 NormalY=0 NormalZ=1 AngleXU=0 Radius=1.75
    g6: GeomPoint X=20 Y=10 Z=0
  constraints (19):
    c: Equal(g3,g2)
    c: Equal(g3,g5)
    c: Equal(g3,g4)
    c: Coincident(g0,g-5)
    c: Coincident(g1,g-4)
    c: DistanceX(g-3,g-3) = 40
    c: Horizontal(g2,g5)
    c: Horizontal(g3,g4)
    c: Diameter(g3) = 3.5
    c: Vertical(g3,g2)
    c: Vertical(g5,g4)
    c: PointOnObject(g6,g0)
    c: PointOnObject(g6,g1)
    c: DistanceX(g2,g6) = 8
    c: DistanceY(g6,g2) = 7
    c: Symmetric(g2,g4,g6)
    c: Coincident(g1,g-1)
    c: PointOnObject(g0,g-1)
    c: Vertical(g-4,g0)
FEATURE [PartDesign::Pocket] Pocket119
  BaseFeature = -> Pocket118
  Direction = (-1,0,0)
  Length = 5
  Length2 = 100
  Profile = -> Sketch285
  ReferenceAxis = -> Sketch285 [N_Axis]
  Suppressed = false
  Type = 1
FEATURE [Sketcher::SketchObject] Sketch286
  ArcFitTolerance = 1e-06
  AttachmentSupport = -> [Pocket119]
  ExternalGeometry = -> [Pocket119]
  FullyConstrained = true
  MakeInternals = false
  MapMode = 5
  Placement = pos=(50,0,0) rot=(0.57735,0.57735,0.57735;2.0944rad)
  sketch-geometry (4):
    g0: Circle CenterX=12 CenterY=17 CenterZ=0 NormalX=0 NormalY=0 NormalZ=1 AngleXU=0 Radius=2.125
    g1: Circle CenterX=28 CenterY=17 CenterZ=0 NormalX=0 NormalY=0 NormalZ=1 AngleXU=0 Radius=2.125
    g2: Circle CenterX=28 CenterY=3 CenterZ=0 NormalX=0 NormalY=0 NormalZ=1 AngleXU=0 Radius=2.125
    g3: Circle CenterX=12 CenterY=3 CenterZ=0 NormalX=0 NormalY=0 NormalZ=1 AngleXU=0 Radius=2.125
  constraints (8):
    c: Equal(g0,g1)
    c: Equal(g1,g3)
    c: Equal(g3,g2)
    c: Diameter(g0) = 4.25
    c: Coincident(g0,g-3)
    c: Coincident(g-4,g1)
    c: Coincident(g-5,g2)
    c: Coincident(g-6,g3)
FEATURE [PartDesign::Pocket] Pocket120
  BaseFeature = -> Pocket119
  Direction = (-1,0,0)
  Length = 1.5
  Length2 = 5
  Profile = -> Sketch286
  ReferenceAxis = -> Sketch286 [N_Axis]
  Refine = true
  Suppressed = false
  Type = 0
FEATURE [Sketcher::SketchObject] Sketch287
  ArcFitTolerance = 1e-06
  AttachmentSupport = -> [Pocket120]
  ExternalGeometry = -> [Pocket120]
  FullyConstrained = true
  MakeInternals = false
  MapMode = 5
  Placement = pos=(0,0,0) rot=(0.57735,-0.57735,-0.57735;2.0944rad)
  sketch-geometry (4):
    g0: Circle CenterX=-28 CenterY=17 CenterZ=0 NormalX=0 NormalY=0 NormalZ=1 AngleXU=0 Radius=2.1
    g1: Circle CenterX=-12 CenterY=17 CenterZ=0 NormalX=0 NormalY=0 NormalZ=1 AngleXU=0 Radius=2.1
    g2: Circle CenterX=-12 CenterY=3 CenterZ=0 NormalX=0 NormalY=0 NormalZ=1 AngleXU=0 Radius=2.1
    g3: Circle CenterX=-28 CenterY=3 CenterZ=0 NormalX=0 NormalY=0 NormalZ=1 AngleXU=0 Radius=2.1
  constraints (8):
    c: Equal(g0,g1)
    c: Equal(g1,g3)
    c: Equal(g3,g2)
    c: Diameter(g0) = 4.2
    c: Coincident(g0,g-3)
    c: Coincident(g-4,g1)
    c: Coincident(g-5,g2)
    c: Coincident(g3,g-6)
FEATURE [PartDesign::Pocket] Pocket121
  BaseFeature = -> Pocket120
  Direction = (1,0,0)
  Length = 1.5
  Length2 = 5
  Profile = -> Sketch287
  ReferenceAxis = -> Sketch287 [N_Axis]
  Refine = true
  Suppressed = false
  Type = 0
FEATURE [Sketcher::SketchObject] Sketch288
  ArcFitTolerance = 1e-06
  AttachmentSupport = -> [Pocket121]
  ExternalGeometry = -> [Pocket121]
  FullyConstrained = true
  MakeInternals = false
  MapMode = 5
  Placement = pos=(0,0,20) rot=(0,0,1;0rad)
  sketch-geometry (4):
    g0: Circle CenterX=4 CenterY=36 CenterZ=0 NormalX=0 NormalY=0 NormalZ=1 AngleXU=0 Radius=2.1
    g1: Circle CenterX=46 CenterY=36 CenterZ=0 NormalX=0 NormalY=0 NormalZ=1 AngleXU=0 Radius=2.1
    g2: Circle CenterX=4 CenterY=4 CenterZ=0 NormalX=0 NormalY=0 NormalZ=1 AngleXU=0 Radius=2.1
    g3: Circle CenterX=46 CenterY=4 CenterZ=0 NormalX=0 NormalY=0 NormalZ=1 AngleXU=0 Radius=2.1
  constraints (8):
    c: Coincident(g0,g-3)
    c: Coincident(g1,g-6)
    c: Coincident(g2,g-4)
    c: Coincident(g3,g-5)
    c: Equal(g0,g2)
    c: Equal(g2,g1)
    c: Equal(g1,g3)
    c: Diameter(g0) = 4.2
FEATURE [PartDesign::Pocket] Pocket122
  BaseFeature = -> Pocket121
  Direction = (0,0,-1)
  Length = 1.5
  Length2 = 5
  Profile = -> Sketch288
  ReferenceAxis = -> Sketch288 [N_Axis]
  Refine = true
  Suppressed = false
  Type = 0
FEATURE [Sketcher::SketchObject] Sketch289
  ArcFitTolerance = 1e-06
  AttachmentSupport = -> [Pocket122]
  ExternalGeometry = -> [Pocket122]
  FullyConstrained = true
  MakeInternals = false
  MapMode = 5
  Placement = pos=(0,0,-2) rot=(1,0,0;3.14159rad)
  sketch-geometry (4):
    g0: Circle CenterX=4 CenterY=-4 CenterZ=0 NormalX=0 NormalY=0 NormalZ=1 AngleXU=0 Radius=2.1
    g1: Circle CenterX=46 CenterY=-4 CenterZ=0 NormalX=0 NormalY=0 NormalZ=1 AngleXU=0 Radius=2.1
    g2: Circle CenterX=46 CenterY=-36 CenterZ=0 NormalX=0 NormalY=0 NormalZ=1 AngleXU=0 Radius=2.1
    g3: Circle CenterX=4 CenterY=-36 CenterZ=0 NormalX=0 NormalY=0 NormalZ=1 AngleXU=0 Radius=2.1
  constraints (8):
    c: Coincident(g0,g-3)
    c: Coincident(g1,g-5)
    c: Coincident(g2,g-6)
    c: Coincident(g3,g-4)
    c: Equal(g0,g1)
    c: Equal(g1,g2)
    c: Equal(g2,g3)
    c: Diameter(g0) = 4.2
FEATURE [PartDesign::Pocket] Pocket123
  BaseFeature = -> Pocket122
  Direction = (0,0,1)
  Length = 1.5
  Length2 = 5
  Profile = -> Sketch289
  ReferenceAxis = -> Sketch289 [N_Axis]
  Refine = true
  Suppressed = false
  Type = 0
FEATURE [PartDesign::Body] Body101  label="pince_support_servo002"
  AllowCompound = false
  Group = -> [Sketch282,Pad137,Sketch283,Pad138,Sketch284,Pocket118,Sketch285,Pocket119,Sketch286,Pocket120,Sketch287,Pocket121,Sketch288,Pocket122,Sketch289,Pocket123]
  Origin = -> Origin374
  Tip = -> Pocket123
FEATURE [App::FeaturePython] GroundedJoint002  # Assembly grounded joint (typed FeaturePython)
  ObjectToGround = -> Body101
FEATURE [Assembly::JointGroup] Joints003
  Group = -> [GroundedJoint002,Joint011,Joint012,Joint013,Joint014,Joint015,Joint016,Joint017,Joint018,Joint019,Joint020]
FEATURE [Sketcher::SketchObject] Sketch290
  ArcFitTolerance = 0
  FullyConstrained = true
  MakeInternals = false
  MapMode = 5
  Placement = pos=(0,0,5.5) rot=(0,0,1;0rad)
  sketch-geometry (8):
    g0: Circle [constr] CenterX=0 CenterY=0 CenterZ=0 NormalX=0 NormalY=0 NormalZ=1 AngleXU=0 Radius=7
    g1: Circle CenterX=0 CenterY=7 CenterZ=0 NormalX=0 NormalY=0 NormalZ=1 AngleXU=0 Radius=1.65
    g2: Circle CenterX=-7 CenterY=0 CenterZ=0 NormalX=0 NormalY=0 NormalZ=1 AngleXU=0 Radius=1.65
    g3: Circle CenterX=7 CenterY=0 CenterZ=0 NormalX=0 NormalY=0 NormalZ=1 AngleXU=0 Radius=1.65
    g4: Circle CenterX=0 CenterY=-7 CenterZ=0 NormalX=0 NormalY=0 NormalZ=1 AngleXU=0 Radius=1.65
    g5: Circle CenterX=0 CenterY=0 CenterZ=0 NormalX=0 NormalY=0 NormalZ=1 AngleXU=0 Radius=3
    g6: LineSegment [constr] StartX=-7 StartY=0 StartZ=0 EndX=7 EndY=0 EndZ=0
    g7: LineSegment [constr] StartX=0 StartY=7 StartZ=0 EndX=0 EndY=-7 EndZ=0
  constraints (20):
    c: Coincident(g5,g0)
    c: Coincident(g5,g-1)
    c: PointOnObject(g2,g0)
    c: PointOnObject(g1,g0)
    c: PointOnObject(g3,g0)
    c: PointOnObject(g4,g0)
    c: Coincident(g2,g6)
    c: Coincident(g1,g7)
    c: Coincident(g6,g3)
    c: Coincident(g7,g4)
    c: PointOnObject(g5,g7)
    c: PointOnObject(g5,g6)
    c: Perpendicular(g7,g6)
    c: Equal(g1,g3)
    c: Equal(g1,g2)
    c: Equal(g1,g4)
    c: Diameter(g1) = 3.3
    c: Diameter(g5) = 6
    c: Diameter(g0) = 14
    c: PointOnObject(g2,g-1)
FEATURE [PartDesign::Pocket] Pocket124
  BaseFeature = -> BaseFeature005
  Direction = (0,0,-1)
  Length = 5
  Length2 = 100
  Profile = -> Sketch290
  Suppressed = false
  Type = 1
FEATURE [Sketcher::SketchObject] Sketch291
  ArcFitTolerance = 0
  AttachmentSupport = -> [Pocket124]
  ExternalGeometry = -> [Pocket124]
  FullyConstrained = true
  MakeInternals = false
  MapMode = 5
  Placement = pos=(0,0,0) rot=(1,0,0;3.14159rad)
  sketch-geometry (4):
    g0: Circle CenterX=0 CenterY=-7 CenterZ=0 NormalX=0 NormalY=0 NormalZ=1 AngleXU=0 Radius=3.25
    g1: Circle CenterX=-7 CenterY=0 CenterZ=0 NormalX=0 NormalY=0 NormalZ=1 AngleXU=0 Radius=3.25
    g2: Circle CenterX=7 CenterY=0 CenterZ=0 NormalX=0 NormalY=0 NormalZ=1 AngleXU=0 Radius=3.25
    g3: Circle CenterX=0 CenterY=7 CenterZ=0 NormalX=0 NormalY=0 NormalZ=1 AngleXU=0 Radius=3.25
  constraints (8):
    c: Coincident(g1,g-5)
    c: Coincident(g0,g-3)
    c: Coincident(g2,g-4)
    c: Coincident(g3,g-6)
    c: Equal(g2,g0)
    c: Equal(g2,g1)
    c: Equal(g2,g3)
    c: Diameter(g2) = 6.5
FEATURE [PartDesign::Pocket] Pocket125
  BaseFeature = -> Pocket124
  Direction = (0,0,1)
  Length = 3.5
  Length2 = 100
  Profile = -> Sketch291
  Suppressed = false
  Type = 0
FEATURE [PartDesign::Body] Body102  label="pince_cremaillere_pignon002"
  AllowCompound = false
  BaseFeature = -> InvoluteGear002
  Group = -> [BaseFeature005,Sketch290,Pocket124,Sketch291,Pocket125]
  Origin = -> Origin375
  Placement = pos=(25,20,27.098) rot=(0.715163,-0.698958,0;3.14159rad)
  Tip = -> Pocket125
FEATURE [Sketcher::SketchObject] Sketch292
  ArcFitTolerance = 0
  FullyConstrained = true
  MakeInternals = false
  MapMode = 2
  sketch-geometry (25):
    g0: LineSegment StartX=0 StartY=50 StartZ=0 EndX=100 EndY=50 EndZ=0
    g1: LineSegment StartX=100 StartY=50 StartZ=0 EndX=100 EndY=0 EndZ=0
    g2: LineSegment StartX=100 StartY=0 StartZ=0 EndX=0 EndY=0 EndZ=0
    g3: LineSegment StartX=0 StartY=0 StartZ=0 EndX=0 EndY=50 EndZ=0
    g4: Circle CenterX=50 CenterY=25 CenterZ=0 NormalX=0 NormalY=0 NormalZ=1 AngleXU=0 Radius=14
    g5: LineSegment [constr] StartX=0 StartY=50 StartZ=0 EndX=100 EndY=0 EndZ=0
    g6: LineSegment [constr] StartX=0 StartY=0 StartZ=0 EndX=100 EndY=50 EndZ=0
    g7: LineSegment [constr] StartX=29 StartY=41 StartZ=0 EndX=71 EndY=41 EndZ=0
    g8: LineSegment [constr] StartX=71 StartY=41 StartZ=0 EndX=71 EndY=9 EndZ=0
    g9: LineSegment [constr] StartX=71 StartY=9 StartZ=0 EndX=29 EndY=9 EndZ=0
    g10: LineSegment [constr] StartX=29 StartY=9 StartZ=0 EndX=29 EndY=41 EndZ=0
    g11: Circle CenterX=29 CenterY=41 CenterZ=0 NormalX=0 NormalY=0 NormalZ=1 AngleXU=0 Radius=1.75
    g12: Circle CenterX=71 CenterY=41 CenterZ=0 NormalX=0 NormalY=0 NormalZ=1 AngleXU=0 Radius=1.75
    g13: Circle CenterX=71 CenterY=9 CenterZ=0 NormalX=0 NormalY=0 NormalZ=1 AngleXU=0 Radius=1.75
    g14: Circle CenterX=29 CenterY=9 CenterZ=0 NormalX=0 NormalY=0 NormalZ=1 AngleXU=0 Radius=1.75
    g15: LineSegment [constr] StartX=0 StartY=25 StartZ=0 EndX=100 EndY=25 EndZ=0
    g16: LineSegment [constr] StartX=50 StartY=50 StartZ=0 EndX=50 EndY=0 EndZ=0
    g17: LineSegment [constr] StartX=3.5 StartY=33.25 StartZ=0 EndX=96.5 EndY=33.25 EndZ=0
    g18: LineSegment [constr] StartX=96.5 StartY=33.25 StartZ=0 EndX=96.5 EndY=16.75 EndZ=0
    g19: LineSegment [constr] StartX=96.5 StartY=16.75 StartZ=0 EndX=3.5 EndY=16.75 EndZ=0
    g20: LineSegment [constr] StartX=3.5 StartY=16.75 StartZ=0 EndX=3.5 EndY=33.25 EndZ=0
    g21: Circle CenterX=96.5 CenterY=33.25 CenterZ=0 NormalX=0 NormalY=0 NormalZ=1 AngleXU=0 Radius=1.65
    g22: Circle CenterX=3.5 CenterY=33.25 CenterZ=0 NormalX=0 NormalY=0 NormalZ=1 AngleXU=0 Radius=1.65
    g23: Circle CenterX=3.5 CenterY=16.75 CenterZ=0 NormalX=0 NormalY=0 NormalZ=1 AngleXU=0 Radius=1.65
    g24: Circle CenterX=96.5 CenterY=16.75 CenterZ=0 NormalX=0 NormalY=0 NormalZ=1 AngleXU=0 Radius=1.65
  constraints (60):
    c: Coincident(g0,g1)
    c: Coincident(g1,g2)
    c: Coincident(g2,g3)
    c: Coincident(g3,g0)
    c: Horizontal(g0)
    c: Horizontal(g2)
    c: Vertical(g1)
    c: Vertical(g3)
    c: Coincident(g2,g-1)
    c: Coincident(g5,g0)
    c: Coincident(g2,g6)
    c: Coincident(g0,g6)
    c: Coincident(g1,g5)
    c: PointOnObject(g4,g6)
    c: PointOnObject(g4,g5)
    c: Diameter(g4) = 28
    c: DistanceY(g3,g3) = 50
    c: DistanceX(g2,g2) = 100
    c: Coincident(g7,g8)
    c: Coincident(g8,g9)
    c: Coincident(g9,g10)
    c: Coincident(g10,g7)
    c: Horizontal(g7)
    c: Vertical(g10)
    c: Coincident(g11,g7)
    c: Coincident(g7,g12)
    c: Coincident(g9,g14)
    c: Coincident(g8,g13)
    c: Equal(g11,g12)
    c: Equal(g11,g14)
    c: Equal(g11,g13)
    c: Radius(g11) = 1.75
    c: DistanceY(g10,g10) = 32
    c: DistanceX(g7,g7) = 42
    c: PointOnObject(g16,g0)
    c: PointOnObject(g15,g1)
    c: PointOnObject(g15,g3)
    c: PointOnObject(g16,g2)
    c: Symmetric(g0,g0,g16)
    c: Symmetric(g0,g2,g15)
    c: Symmetric(g14,g13,g16)
    c: Symmetric(g12,g13,g15)
    c: Coincident(g17,g18)
    c: Coincident(g18,g19)
    c: Coincident(g19,g20)
    c: Coincident(g20,g17)
    c: Horizontal(g19)
    c: Vertical(g20)
    c: Symmetric(g17,g18,g15)
    c: Symmetric(g17,g17,g16)
    c: Distance(g20) = 16.5
    c: DistanceX(g0,g17) = 3.5
    c: Coincident(g24,g18)
    c: Coincident(g21,g17)
    c: Coincident(g17,g22)
    c: Coincident(g19,g23)
    c: Equal(g22,g23)
    c: Equal(g22,g21)
    c: Equal(g22,g24)
    c: Diameter(g22) = 3.3
FEATURE [PartDesign::Pad] Pad139
  AlongSketchNormal = false
  Direction = (0,0,1)
  Length = 8
  Length2 = 100
  Profile = -> Sketch292
  Suppressed = false
  Type = 0
FEATURE [Sketcher::SketchObject] Sketch293
  ArcFitTolerance = 0
  AttachmentSupport = -> [Pad139]
  ExternalGeometry = -> [Pad139]
  FullyConstrained = true
  MakeInternals = false
  MapMode = 5
  Placement = pos=(0,0,8) rot=(0,0,1;0rad)
  sketch-geometry (9):
    g0: LineSegment StartX=0 StartY=48 StartZ=0 EndX=100 EndY=48 EndZ=0
    g1: LineSegment StartX=100 StartY=48 StartZ=0 EndX=100 EndY=35.75 EndZ=0
    g2: LineSegment StartX=100 StartY=35.75 StartZ=0 EndX=0 EndY=35.75 EndZ=0
    g3: LineSegment StartX=0 StartY=35.75 StartZ=0 EndX=0 EndY=48 EndZ=0
    g4: LineSegment StartX=0 StartY=2 StartZ=0 EndX=100 EndY=2 EndZ=0
    g5: LineSegment StartX=100 StartY=2 StartZ=0 EndX=100 EndY=14.25 EndZ=0
    g6: LineSegment StartX=100 StartY=14.25 StartZ=0 EndX=0 EndY=14.25 EndZ=0
    g7: LineSegment StartX=0 StartY=14.25 StartZ=0 EndX=0 EndY=2 EndZ=0
    g8: Circle [constr] CenterX=50 CenterY=25 CenterZ=0 NormalX=0 NormalY=0 NormalZ=1 AngleXU=0 Radius=10.75
  constraints (26):
    c: Coincident(g0,g1)
    c: Coincident(g1,g2)
    c: Coincident(g2,g3)
    c: Coincident(g3,g0)
    c: Horizontal(g0)
    c: Horizontal(g2)
    c: Vertical(g1)
    c: Vertical(g3)
    c: Coincident(g4,g5)
    c: Coincident(g5,g6)
    c: Coincident(g6,g7)
    c: Coincident(g7,g4)
    c: Horizontal(g4)
    c: Horizontal(g6)
    c: Vertical(g5)
    c: Vertical(g7)
    c: PointOnObject(g6,g-6)
    c: PointOnObject(g2,g-6)
    c: PointOnObject(g1,g-5)
    c: PointOnObject(g5,g-5)
    c: Coincident(g8,g-7)
    c: Diameter(g8) = 21.5
    c: Tangent(g8,g2)
    c: Tangent(g6,g8)
    c: Equal(g7,g3)
    c: DistanceY(g0,g-6) = 2
FEATURE [PartDesign::Pocket] Pocket126
  BaseFeature = -> Pad139
  Direction = (0,0,-1)
  Length = 4
  Length2 = 100
  Profile = -> Sketch293
  Suppressed = false
  Type = 0
FEATURE [Sketcher::SketchObject] Sketch294
  ArcFitTolerance = 0
  AttachmentSupport = -> [Pocket126]
  ExternalGeometry = -> [Pocket126]
  FullyConstrained = true
  MakeInternals = false
  MapMode = 5
  Placement = pos=(0,0,8) rot=(0,0,1;0rad)
  sketch-geometry (10):
    g0: ArcOfCircle CenterX=11 CenterY=25 CenterZ=0 NormalX=0 NormalY=0 NormalZ=1 AngleXU=0 Radius=8 StartAngle=1.5708 EndAngle=4.71239
    g1: ArcOfCircle CenterX=26 CenterY=25 CenterZ=0 NormalX=0 NormalY=0 NormalZ=1 AngleXU=0 Radius=8 StartAngle=4.71239 EndAngle=7.85398
    g2: LineSegment StartX=11 StartY=17 StartZ=0 EndX=26 EndY=17 EndZ=0
    g3: LineSegment StartX=26 StartY=33 StartZ=0 EndX=11 EndY=33 EndZ=0
    g4: ArcOfCircle CenterX=74 CenterY=25 CenterZ=0 NormalX=0 NormalY=0 NormalZ=1 AngleXU=0 Radius=8 StartAngle=1.5708 EndAngle=4.71239
    g5: ArcOfCircle CenterX=89 CenterY=25 CenterZ=0 NormalX=0 NormalY=0 NormalZ=1 AngleXU=0 Radius=8 StartAngle=4.71239 EndAngle=7.85398
    g6: LineSegment StartX=74 StartY=17 StartZ=0 EndX=89 EndY=17 EndZ=0
    g7: LineSegment StartX=89 StartY=33 StartZ=0 EndX=74 EndY=33 EndZ=0
    g8: LineSegment [constr] StartX=50 StartY=50 StartZ=0 EndX=50 EndY=0 EndZ=0
    g9: LineSegment [constr] StartX=0 StartY=25 StartZ=0 EndX=100 EndY=25 EndZ=0
  constraints (26):
    c: Tangent(g0,g2) = -1.5708
    c: Tangent(g2,g1) = -1.5708
    c: Tangent(g1,g3) = -1.5708
    c: Tangent(g3,g0) = -1.5708
    c: Equal(g0,g1)
    c: Tangent(g4,g6) = -1.5708
    c: Tangent(g6,g5) = -1.5708
    c: Tangent(g5,g7) = -1.5708
    c: Tangent(g7,g4) = -1.5708
    c: Equal(g4,g5)
    c: PointOnObject(g-7,g9)
    c: PointOnObject(g-7,g8)
    c: PointOnObject(g8,g-6)
    c: PointOnObject(g8,g-5)
    c: PointOnObject(g9,g-3)
    c: PointOnObject(g9,g-4)
    c: Horizontal(g9)
    c: Vertical(g8)
    c: PointOnObject(g0,g9)
    c: PointOnObject(g1,g9)
    c: Symmetric(g1,g4,g8)
    c: Symmetric(g5,g0,g8)
    c: Equal(g1,g4)
    c: DistanceX(g-3,g0) = 11
    c: DistanceX(g1,g8) = 24
    c: DistanceY(g-7,g1) = 8
FEATURE [PartDesign::Pocket] Pocket127
  BaseFeature = -> Pocket126
  Direction = (0,0,-1)
  Length = 5
  Length2 = 100
  Profile = -> Sketch294
  Suppressed = false
  Type = 1
FEATURE [Sketcher::SketchObject] Sketch295
  ArcFitTolerance = 0
  AttachmentSupport = -> [Pocket127]
  ExternalGeometry = -> [Pocket127]
  FullyConstrained = true
  MakeInternals = false
  MapMode = 5
  Placement = pos=(0,0,4) rot=(0,0,1;0rad)
  sketch-geometry (4):
    g0: Circle CenterX=29 CenterY=41 CenterZ=0 NormalX=0 NormalY=0 NormalZ=1 AngleXU=0 Radius=3.5
    g1: Circle CenterX=71 CenterY=41 CenterZ=0 NormalX=0 NormalY=0 NormalZ=1 AngleXU=0 Radius=3.5
    g2: Circle CenterX=29 CenterY=9 CenterZ=0 NormalX=0 NormalY=0 NormalZ=1 AngleXU=0 Radius=3.5
    g3: Circle CenterX=71 CenterY=9 CenterZ=0 NormalX=0 NormalY=0 NormalZ=1 AngleXU=0 Radius=3.5
  constraints (8):
    c: Coincident(g-3,g0)
    c: Coincident(g1,g-4)
    c: Coincident(g2,g-5)
    c: Coincident(g3,g-6)
    c: Equal(g0,g1)
    c: Equal(g0,g2)
    c: Equal(g0,g3)
    c: Diameter(g0) = 7
FEATURE [PartDesign::Pocket] Pocket128
  BaseFeature = -> Pocket127
  Direction = (0,0,-1)
  Length = 2
  Length2 = 100
  Profile = -> Sketch295
  Suppressed = false
  Type = 0
FEATURE [PartDesign::Body] Body103  label="pince_support_cremaillere002"
  AllowCompound = false
  Group = -> [Sketch292,Pad139,Sketch293,Pocket126,Sketch294,Pocket127,Sketch295,Pocket128]
  Origin = -> Origin376
  Placement = pos=(-25,-5,20) rot=(0,0,1;0rad)
  Tip = -> Pocket128
FEATURE [Sketcher::SketchObject] Sketch296
  ArcFitTolerance = 1e-06
  AttachmentSupport = -> [XZ_Plane374]
  FullyConstrained = true
  MakeInternals = false
  MapMode = 5
  Placement = pos=(0,0,0) rot=(1,0,0;1.5708rad)
  sketch-geometry (4):
    g0: LineSegment StartX=-4.5 StartY=0 StartZ=0 EndX=4.5 EndY=0 EndZ=0
    g1: LineSegment StartX=4.5 StartY=0 StartZ=0 EndX=4.5 EndY=3 EndZ=0
    g2: LineSegment StartX=4.5 StartY=3 StartZ=0 EndX=-4.5 EndY=3 EndZ=0
    g3: LineSegment StartX=-4.5 StartY=3 StartZ=0 EndX=-4.5 EndY=0 EndZ=0
  constraints (11):
    c: Coincident(g0,g1)
    c: Coincident(g1,g2)
    c: Coincident(g2,g3)
    c: Coincident(g3,g0)
    c: Horizontal(g0)
    c: Vertical(g1)
    c: Vertical(g3)
    c: PointOnObject(g0,g-1)
    c: Symmetric(g1,g2,g-2)
    c: Distance(g2,g2) = 9
    c: DistanceY(g3,g3) = 3
FEATURE [PartDesign::Pad] Pad140
  Direction = (0,-1,2e-16)
  Length = 40
  Length2 = 10
  Midplane = true
  Placement = pos=(0,0,0) rot=(1,0,0;1.5708rad)
  Profile = -> Sketch296
  ReferenceAxis = -> Sketch296 [N_Axis]
  Suppressed = false
  Type = 0
FEATURE [PartDesign::Body] Body104  label="mousse004"
  AllowCompound = false
  Group = -> [Sketch296,Pad140]
  Origin = -> Origin377
  Placement = pos=(71.5056,23,59.5) rot=(0.707107,0,0.707107;3.14159rad)
  Tip = -> Pad140
FEATURE [Sketcher::SketchObject] Sketch297
  ArcFitTolerance = 0
  AttachmentSupport = -> [XZ_Plane376]
  FullyConstrained = true
  MakeInternals = false
  MapMode = 5
  Placement = pos=(0,0,0) rot=(1,0,0;1.5708rad)
  expr: Constraints[19] = 19.8 / 2
  sketch-geometry (8):
    g0: LineSegment StartX=2.5 StartY=3.4 StartZ=0 EndX=2.5 EndY=0 EndZ=0
    g1: LineSegment StartX=2.5 StartY=0 StartZ=0 EndX=4.2 EndY=0 EndZ=0
    g2: LineSegment StartX=4.2 StartY=0 StartZ=0 EndX=4.2 EndY=2 EndZ=0
    g3: LineSegment StartX=4.2 StartY=2 StartZ=0 EndX=9.9 EndY=2 EndZ=0
    g4: LineSegment StartX=9.9 StartY=2 StartZ=0 EndX=9.9 EndY=4.4 EndZ=0
    g5: LineSegment StartX=9.9 StartY=4.4 StartZ=0 EndX=1.5 EndY=4.4 EndZ=0
    g6: LineSegment StartX=1.5 StartY=4.4 StartZ=0 EndX=1.5 EndY=3.4 EndZ=0
    g7: LineSegment StartX=1.5 StartY=3.4 StartZ=0 EndX=2.5 EndY=3.4 EndZ=0
  constraints (24):
    c: PointOnObject(g0,g-1)
    c: Vertical(g0)
    c: Coincident(g1,g0)
    c: PointOnObject(g1,g-1)
    c: Coincident(g2,g1)
    c: Vertical(g2)
    c: Coincident(g3,g2)
    c: Horizontal(g3)
    c: Coincident(g4,g3)
    c: Vertical(g4)
    c: Coincident(g5,g4)
    c: Horizontal(g5)
    c: Coincident(g6,g5)
    c: Coincident(g7,g6)
    c: Coincident(g7,g0)
    c: Horizontal(g7)
    c: Vertical(g6)
    c: DistanceY(g4,g4) = 2.4
    c: DistanceY(g2,g2) = 2
    c: DistanceX(g-1,g4) = 9.9
    c: DistanceX(g-1,g6) = 1.5
    c: DistanceY(g0,g0) = 3.4
    c: DistanceX(g-1,g0) = 2.5
    c: DistanceX(g1,g1) = 1.7
FEATURE [PartDesign::Revolution] Revolution003
  Angle = 360
  Angle2 = 60
  Axis = (0,2e-16,1)
  Base = (0,0,0)
  Placement = pos=(0,0,0) rot=(1,0,0;1.5708rad)
  Profile = -> Sketch297
  ReferenceAxis = -> Sketch297 [V_Axis]
  Reversed = true
  Suppressed = false
  Type = 0
FEATURE [Sketcher::SketchObject] Sketch298
  ArcFitTolerance = 0
  AttachmentSupport = -> [XY_Plane376]
  FullyConstrained = true
  MakeInternals = false
  MapMode = 5
  sketch-geometry (1):
    g0: Circle CenterX=-7 CenterY=0 CenterZ=0 NormalX=0 NormalY=0 NormalZ=1 AngleXU=0 Radius=1.2
  constraints (3):
    c: PointOnObject(g0,g-1)
    c: Diameter(g0) = 2.4
    c: DistanceX(g0,g-1) = 7
FEATURE [PartDesign::Pocket] Pocket129
  BaseFeature = -> Revolution003
  Direction = (0,0,-1)
  Length = 5
  Length2 = 5
  Midplane = true
  Placement = pos=(0,0,0) rot=(1,0,0;1.5708rad)
  Profile = -> Sketch298
  ReferenceAxis = -> Sketch298 [N_Axis]
  Suppressed = false
  Type = 1
FEATURE [PartDesign::PolarPattern] PolarPattern007
  Angle = 360
  Axis = -> Sketch298 [N_Axis]
  BaseFeature = -> Pocket129
  Mode = 0
  Occurrences = 4
  Offset = 120
  Originals = -> [Pocket129]
  Placement = pos=(0,0,0) rot=(1,0,0;1.5708rad)
  Suppressed = false
  TransformMode = 0
FEATURE [PartDesign::Body] Body098  label="Corps005"
  AllowCompound = false
  Group = -> [Sketch297,Revolution003,Sketch298,Pocket129,PolarPattern007]
  Origin = -> Origin379
  Placement = pos=(0,0,0.4) rot=(0,0,1;0rad)
  Tip = -> PolarPattern007
FEATURE [App::Part] Part002006  label="servo_DS3218MG005"
  Group = -> [Part__Feature008002002006938,Part__Feature008002002006939,Part__Feature008002002006940,Body098,Screw006]
  Origin = -> Origin378
  Placement = pos=(25,20,15.9) rot=(0,0,-1;1.5708rad)
FEATURE [Sketcher::SketchObject] Sketch299
  ArcFitTolerance = 1e-06
  AttachmentOffset = pos=(0,0,-10.75) rot=(0,0,1;0rad)
  AttachmentSupport = -> [YZ_Plane370]
  ExternalGeometry = -> [Pad136]
  FullyConstrained = true
  MakeInternals = false
  MapMode = 5
  Placement = pos=(-10.75,0,0) rot=(0.57735,0.57735,0.57735;2.0944rad)
  sketch-geometry (3):
    g0: LineSegment StartX=67.677 StartY=3 StartZ=0 EndX=92.677 EndY=9 EndZ=0
    g1: LineSegment StartX=67.677 StartY=3 StartZ=0 EndX=92.677 EndY=3 EndZ=0
    g2: LineSegment StartX=92.677 StartY=9 StartZ=0 EndX=92.677 EndY=3 EndZ=0
  constraints (8):
    c: PointOnObject(g0,g-4)
    c: Coincident(g1,g0)
    c: Coincident(g1,g-4)
    c: Coincident(g2,g0)
    c: Coincident(g2,g1)
    c: DistanceX(g1,g1) = 25
    c: Vertical(g2)
    c: DistanceY(g2,g2) = 6
FEATURE [PartDesign::Pad] Pad141
  BaseFeature = -> Pad136
  Direction = (1,0,0)
  Length = 5
  Length2 = 10
  Profile = -> Sketch299
  ReferenceAxis = -> Sketch299 [N_Axis]
  Suppressed = false
  Type = 0
FEATURE [PartDesign::Body] Body100  label="pince_cremaillere_bras004"
  AllowCompound = false
  BaseFeature = -> InvoluteRack002
  Group = -> [BaseFeature004,Sketch281,Pad136,Sketch299,Pad141]
  Origin = -> Origin373
  Placement = pos=(-18.1714,32.25,24) rot=(0,0,-1;1.5708rad)
  Tip = -> Pad141
FEATURE [Sketcher::SketchObject] Sketch300
  ArcFitTolerance = 1e-06
  AttachmentSupport = -> [XZ_Plane377]
  FullyConstrained = true
  MakeInternals = false
  MapMode = 5
  Placement = pos=(0,0,0) rot=(1,0,0;1.5708rad)
  sketch-geometry (4):
    g0: LineSegment StartX=-4.5 StartY=0 StartZ=0 EndX=4.5 EndY=0 EndZ=0
    g1: LineSegment StartX=4.5 StartY=0 StartZ=0 EndX=4.5 EndY=2 EndZ=0
    g2: LineSegment StartX=4.5 StartY=2 StartZ=0 EndX=-4.5 EndY=2 EndZ=0
    g3: LineSegment StartX=-4.5 StartY=2 StartZ=0 EndX=-4.5 EndY=0 EndZ=0
  constraints (11):
    c: Coincident(g0,g1)
    c: Coincident(g1,g2)
    c: Coincident(g2,g3)
    c: Coincident(g3,g0)
    c: Horizontal(g0)
    c: Vertical(g1)
    c: Vertical(g3)
    c: PointOnObject(g0,g-1)
    c: Symmetric(g1,g2,g-2)
    c: Distance(g2,g2) = 9
    c: DistanceY(g3,g3) = 2
FEATURE [PartDesign::Pad] Pad142
  Direction = (0,-1,2e-16)
  Length = 40
  Length2 = 10
  Midplane = true
  Placement = pos=(0,0,0) rot=(1,0,0;1.5708rad)
  Profile = -> Sketch300
  ReferenceAxis = -> Sketch300 [N_Axis]
  Suppressed = false
  Type = 0
FEATURE [PartDesign::Body] Body105  label="cale001"
  AllowCompound = false
  Group = -> [Sketch300,Pad142]
  Origin = -> Origin380
  Placement = pos=(71.5056,23,59.5) rot=(0.707107,0,0.707107;3.14159rad)
  Tip = -> Pad142
FEATURE [Assembly::AssemblyObject] Assembly003  label="Assembly_pince001"
  Group = -> [Joints003,Part002006,Body099,InvoluteRack002,Body100,Body101,InvoluteGear002,Body102,Body103,Body104,Link006,Link007,GroundedJoint002,Joint011,Joint012,Joint013,Joint014,Joint015,Joint016,Joint017,Joint018,Joint019,Joint020,Body105]
  Origin = -> Origin371
  Placement = pos=(-24.2459,-118.811,65.4126) rot=(0.999972,-0.004162,-0.006294;3.12914rad)
  Type = Assembly
FEATURE [Sketcher::SketchObject] Sketch305
  ArcFitTolerance = 1e-06
  AttachmentSupport = -> [YZ_Plane378]
  FullyConstrained = true
  MakeInternals = false
  MapMode = 5
  Placement = pos=(0,0,0) rot=(0.57735,0.57735,0.57735;2.0944rad)
  sketch-geometry (8):
    g0: LineSegment StartX=-11 StartY=10 StartZ=0 EndX=-11 EndY=-10 EndZ=0
    g1: LineSegment StartX=-11 StartY=-10 StartZ=0 EndX=11 EndY=-10 EndZ=0
    g2: LineSegment StartX=11 StartY=-10 StartZ=0 EndX=11 EndY=10 EndZ=0
    g3: LineSegment StartX=11 StartY=10 StartZ=0 EndX=-11 EndY=10 EndZ=0
    g4: Circle CenterX=8 CenterY=-7 CenterZ=0 NormalX=0 NormalY=0 NormalZ=1 AngleXU=0 Radius=1.75
    g5: Circle CenterX=-8 CenterY=-7 CenterZ=0 NormalX=0 NormalY=0 NormalZ=1 AngleXU=0 Radius=1.75
    g6: Circle CenterX=8 CenterY=7 CenterZ=0 NormalX=0 NormalY=0 NormalZ=1 AngleXU=0 Radius=1.75
    g7: Circle CenterX=-8 CenterY=7 CenterZ=0 NormalX=0 NormalY=0 NormalZ=1 AngleXU=0 Radius=1.75
  constraints (21):
    c: Coincident(g0,g1)
    c: Coincident(g1,g2)
    c: Coincident(g2,g3)
    c: Coincident(g3,g0)
    c: Vertical(g0)
    c: Vertical(g2)
    c: Horizontal(g1)
    c: Distance(g1,g1) = 22
    c: Symmetric(g0,g1,g-1)
    c: Horizontal(g3)
    c: DistanceY(g2,g2) = 20
    c: Diameter(g4) = 3.5
    c: Diameter(g5) = 3.5
    c: Diameter(g6) = 3.5
    c: Diameter(g7) = 3.5
    c: Symmetric(g7,g4,g-1)
    c: Symmetric(g5,g6,g-1)
    c: Horizontal(g6,g7)
    c: Vertical(g7,g5)
    c: DistanceX(g7,g-1) = 8
    c: DistanceY(g-1,g7) = 7
FEATURE [PartDesign::Pad] Pad144
  Direction = (1,0,0)
  Length = 5
  Length2 = 10
  Placement = pos=(0,0,0) rot=(1,1,1;2.0944rad)
  Profile = -> Sketch305
  ReferenceAxis = -> Sketch305 [N_Axis]
  Suppressed = false
  Type = 0
FEATURE [Sketcher::SketchObject] Sketch306
  ArcFitTolerance = 1e-06
  AttachmentOffset = pos=(0,0,5) rot=(0,0,1;0rad)
  AttachmentSupport = -> [YZ_Plane378]
  FullyConstrained = false
  MakeInternals = false
  MapMode = 5
  Placement = pos=(5,0,0) rot=(0.57735,0.57735,0.57735;2.0944rad)
  sketch-geometry (12):
    g0: LineSegment StartX=-3.23224 StartY=10 StartZ=0 EndX=-3.23224 EndY=3.23224 EndZ=0
    g1: LineSegment StartX=-3.23224 StartY=-10 StartZ=0 EndX=3.23224 EndY=-10 EndZ=0
    g2: LineSegment StartX=3.23224 StartY=-10 StartZ=0 EndX=3.23224 EndY=-3.23224 EndZ=0
    g3: LineSegment StartX=3.23224 StartY=10 StartZ=0 EndX=-3.23224 EndY=10 EndZ=0
    g4: LineSegment StartX=-11 StartY=-3.23224 StartZ=0 EndX=-3.23224 EndY=-3.23224 EndZ=0
    g5: LineSegment StartX=11 StartY=-3.23224 StartZ=0 EndX=11 EndY=3.23224 EndZ=0
    g6: LineSegment StartX=11 StartY=3.23224 StartZ=0 EndX=3.23224 EndY=3.23224 EndZ=0
    g7: LineSegment StartX=-11 StartY=3.23224 StartZ=0 EndX=-11 EndY=-3.23224 EndZ=0
    g8: LineSegment StartX=3.23224 StartY=3.23224 StartZ=0 EndX=3.23224 EndY=10 EndZ=0
    g9: LineSegment StartX=-3.23224 StartY=-3.23224 StartZ=0 EndX=-3.23224 EndY=-10 EndZ=0
    g10: LineSegment StartX=-3.23224 StartY=3.23224 StartZ=0 EndX=-11 EndY=3.23224 EndZ=0
    g11: LineSegment StartX=3.23224 StartY=-3.23224 StartZ=0 EndX=11 EndY=-3.23224 EndZ=0
  constraints (36):
    c: Coincident(g9,g1)
    c: Coincident(g1,g2)
    c: Coincident(g8,g3)
    c: Coincident(g3,g0)
    c: Vertical(g0)
    c: Vertical(g2)
    c: Horizontal(g1)
    c: Horizontal(g3)
    c: Coincident(g11,g5)
    c: Coincident(g5,g6)
    c: Coincident(g10,g7)
    c: Coincident(g7,g4)
    c: Horizontal(g4)
    c: Horizontal(g6)
    c: Vertical(g5)
    c: Vertical(g7)
    c: PointOnObject(g2,g11)
    c: PointOnObject(g0,g10)
    c: Coincident(g6,g8)
    c: PointOnObject(g10,g0)
    c: Coincident(g4,g9)
    c: PointOnObject(g11,g2)
    c: Equal(g0,g8)
    c: Equal(g2,g9)
    c: Equal(g7,g5)
    c: Equal(g5,g3)
    c: Equal(g3,g1)
    c: Symmetric(g2,g0,g-1)
    c: Horizontal(g10)
    c: Vertical(g9)
    c: Vertical(g4,g0)
    c: Vertical(g8)
    c: DistanceY(g-1,g0) = 10
    c: Equal(g10,g6)
    c: DistanceX(g7,g-1) = 11
    c: Equal(g2,g8)
FEATURE [PartDesign::Pad] Pad145
  BaseFeature = -> Pad144
  Direction = (1,0,0)
  Length = 100
  Length2 = 10
  Placement = pos=(0,0,0) rot=(1,1,1;2.0944rad)
  Profile = -> Sketch306
  ReferenceAxis = -> Sketch306 [N_Axis]
  Suppressed = false
  Type = 0
FEATURE [Sketcher::SketchObject] Sketch307
  ArcFitTolerance = 1e-06
  AttachmentSupport = -> [Pad145]
  FullyConstrained = true
  MakeInternals = false
  MapMode = 5
  Placement = pos=(105,0,0) rot=(0.57735,0.57735,0.57735;2.0944rad)
  sketch-geometry (2):
    g0: Circle CenterX=0 CenterY=5 CenterZ=0 NormalX=0 NormalY=0 NormalZ=1 AngleXU=0 Radius=2
    g1: Circle CenterX=0 CenterY=-5 CenterZ=0 NormalX=0 NormalY=0 NormalZ=1 AngleXU=0 Radius=2
  constraints (5):
    c: PointOnObject(g0,g-2)
    c: Symmetric(g0,g1,g-1)
    c: Equal(g1,g0)
    c: DistanceY(g1,g0) = 10
    c: Diameter(g0) = 4
FEATURE [PartDesign::Pocket] Pocket130
  BaseFeature = -> Pad145
  Direction = (-1,0,0)
  Length = 5
  Length2 = 5
  Placement = pos=(0,0,0) rot=(1,1,1;2.0944rad)
  Profile = -> Sketch307
  ReferenceAxis = -> Sketch307 [N_Axis]
  Suppressed = false
  Type = 0
FEATURE [PartDesign::Body] Body106  label="jonction_rail_pince001"
  AllowCompound = false
  Group = -> [Sketch305,Pad144,Sketch306,Pad145,Sketch307,Pocket130]
  Origin = -> Origin381
  Placement = pos=(-24.5372,-138.932,55.6643) rot=(0.004162,0.999972,-0.006227;3.15418rad)
  Tip = -> Pocket130
FEATURE [App::Link] Link  label="jonction_rail_pince002"
  LinkedObject = -> Body106
FEATURE [App::FeaturePython] Joint021  label="Revolute001"  # Assembly joint (typed FeaturePython)
  Activated = true
  AngleMax = 0
  AngleMin = 0
  Detach1 = false
  Detach2 = false
  Distance = 0
  Distance2 = 0
  EnableAngleMax = false
  EnableAngleMin = false
  EnableLengthMax = false
  EnableLengthMin = false
  JointType = 1 (Revolute)
  LengthMax = 0
  LengthMin = 0
  Placement1 = pos=(105,-5.68e-14,5) rot=(-0.57735,-0.57735,-0.57735;4.18879rad)
  Placement2 = pos=(85,7.1e-15,5.68e-14) rot=(0,0,1;0rad)
  Reference1 = -> Assembly [Body106.Edge62,Body106.Edge62]
  Reference2 = -> Assembly [bras_1.Edge14,bras_1.Edge14]
FEATURE [App::FeaturePython] Joint022  label="Revolute002"  # Assembly joint (typed FeaturePython)
  Activated = true
  AngleMax = 0
  AngleMin = 0
  Detach1 = false
  Detach2 = false
  Distance = 0
  Distance2 = 0
  EnableAngleMax = false
  EnableAngleMin = false
  EnableLengthMax = false
  EnableLengthMin = false
  JointType = 1 (Revolute)
  LengthMax = 0
  LengthMin = 0
  Placement1 = pos=(0,12,3) rot=(-0.57735,0.57735,0.57735;4.18879rad)
  Placement2 = pos=(1.07e-14,8,-7) rot=(-0.57735,-0.57735,-0.57735;4.18879rad)
  Reference1 = -> Assembly [Assembly003.Body101.Edge71,Assembly003.Body101.Edge71]
  Reference2 = -> Assembly [Body106.Edge20,Body106.Edge20]
FEATURE [App::FeaturePython] Joint023  label="Revolute003"  # Assembly joint (typed FeaturePython)
  Activated = true
  AngleMax = 0
  AngleMin = 0
  Detach1 = false
  Detach2 = false
  Distance = 0
  Distance2 = 0
  EnableAngleMax = false
  EnableAngleMin = false
  EnableLengthMax = false
  EnableLengthMin = false
  JointType = 1 (Revolute)
  LengthMax = 0
  LengthMin = 0
  Placement1 = pos=(2.13e-14,-8,-7) rot=(-0.57735,-0.57735,-0.57735;4.18879rad)
  Placement2 = pos=(0,28,3) rot=(-0.57735,0.57735,0.57735;4.18879rad)
  Reference1 = -> Assembly [Body106.Edge21,Body106.Edge21]
  Reference2 = -> Assembly [Assembly003.Body101.Edge69,Assembly003.Body101.Edge69]
FEATURE [App::FeaturePython] GroundedJoint  # Assembly grounded joint (typed FeaturePython)
  ObjectToGround = -> Body106
  Placement = pos=(-24.5372,-138.932,55.6643) rot=(0.004162,0.999972,-0.006227;3.15418rad)
FEATURE [Assembly::JointGroup] Joints
  Group = -> [Joint,Joint021,Joint022,Joint023,GroundedJoint]
FEATURE [Assembly::AssemblyObject] Assembly
  Group = -> [Joints,servo_DS3218MG002,bras_1,Joint,Assembly003,Body106,Link,Joint021,Joint022,Joint023,GroundedJoint]
  Origin = -> Origin368
  Type = Assembly
